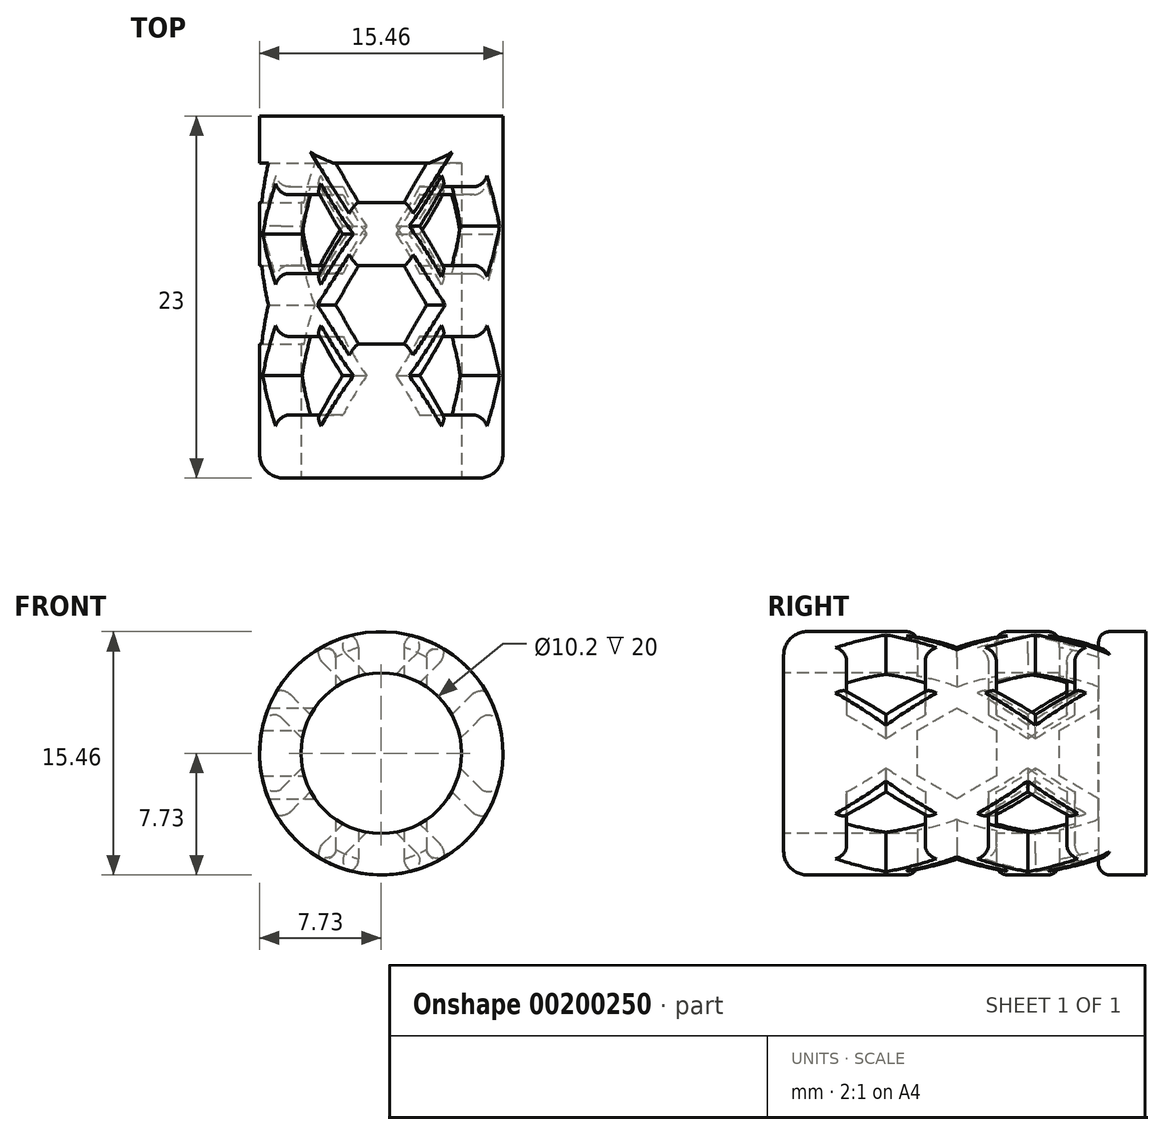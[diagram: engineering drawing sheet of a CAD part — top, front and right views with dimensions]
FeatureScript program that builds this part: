
annotation { "Feature Type Name" : "Feature", "Feature Type Description" : "" }
export const myFeature = defineFeature(function(context is Context, id is Id, definition is map)
    precondition{}
    {
        {
            var Q0;
            Q0=qCreatedBy(makeId("Front.planeOp"),FACE);
            var sketch = newSketch(context, id + "F0", { "sketchPlane" : qUnion([Q0])});
            skCircle(sketch, "E0", {"center": v(0, 0) * mm, "radius": 7.73 * mm});
            skSolve(sketch);
        }
        {
            var Q0;
            Q0=makeQuery(id+"F0.imprint","IMPRINT",FACE,{"disambiguationData":[TD([[makeQuery(id+"F0.imprint","IMPRINT",EDGE,{"derivedFrom":sQuery(id+"F0.wireOp",EDGE,"E0")}),1.0]])]});
            extrude(context, id + "F1", {"entities" : qUnion([Q0]), "oppositeDirection" : true, "depth" : 23 * mm, "offsetDistance" : 25 * mm});
        }
        {
            var Q0;
            Q0=makeQuery(id+"F1.opExtrude","CAP_FACE",FACE,{"disambiguationData":[OSD([sQuery(id+"F0.wireOp",EDGE,"E0")])],"isStart":true});
            var sketch = newSketch(context, id + "F2", { "sketchPlane" : qUnion([Q0])});
            skCircle(sketch, "E1", {"center": v(0, 0) * mm, "radius": 5.1 * mm});
            skSolve(sketch);
        }
        {
            var Q0;
            Q0=qSketchRegion(id+"F2",true);
            extrude(context, id + "F3", {"entities" : qUnion([Q0]), "operationType" : NewBodyOperationType.REMOVE, "oppositeDirection" : true, "depth" : 20 * mm, "offsetDistance" : 25 * mm});
        }
        {
            var Q0;
            Q0=qCreatedBy(makeId("Top.planeOp"),FACE);
            var sketch = newSketch(context, id + "F4", { "sketchPlane" : qUnion([Q0])});
            skLineSegment(sketch, "E2", {"start": v(0, 0) * mm, "end": v(0, 6.5) * mm, "construction": true});
            skLineSegment(sketch, "E3", {"start": v(0, 6.5) * mm, "end": v(0, 9) * mm, "construction": true});
            skCircle(sketch, "E4.cCircle", {"center": v(0, 6.5) * mm, "radius": 2.5 * mm, "construction": true});
            skLineSegment(sketch, "E4.0", {"start": v(-1.44, 9) * mm, "end": v(1.44, 9) * mm});
            skLineSegment(sketch, "E4.1", {"start": v(1.44, 9) * mm, "end": v(2.89, 6.5) * mm});
            skLineSegment(sketch, "E4.2", {"start": v(2.89, 6.5) * mm, "end": v(1.44, 4) * mm});
            skLineSegment(sketch, "E4.3", {"start": v(1.44, 4) * mm, "end": v(-1.44, 4) * mm});
            skLineSegment(sketch, "E4.4", {"start": v(-1.44, 4) * mm, "end": v(-2.89, 6.5) * mm});
            skLineSegment(sketch, "E4.5", {"start": v(-2.89, 6.5) * mm, "end": v(-1.44, 9) * mm});
            skPoint(sketch, "E4.0.midPoint", {"position": v(0, 9) * mm});
            skLineSegment(sketch, "E5.0.1.0", {"start": v(-2.89, 15.5) * mm, "end": v(-1.44, 18) * mm});
            skLineSegment(sketch, "E5.0.1.1", {"start": v(1.44, 13) * mm, "end": v(-1.44, 13) * mm});
            skLineSegment(sketch, "E5.0.1.2", {"start": v(2.89, 15.5) * mm, "end": v(1.44, 13) * mm});
            skLineSegment(sketch, "E5.0.1.3", {"start": v(1.44, 18) * mm, "end": v(2.89, 15.5) * mm});
            skLineSegment(sketch, "E5.0.1.4", {"start": v(-1.44, 18) * mm, "end": v(1.44, 18) * mm});
            skLineSegment(sketch, "E5.0.1.5", {"start": v(0, 15.5) * mm, "end": v(0, 18) * mm, "construction": true});
            skPoint(sketch, "E5.0.1.6", {"position": v(0, 18) * mm});
            skLineSegment(sketch, "E5.0.1.7", {"start": v(-1.44, 13) * mm, "end": v(-2.89, 15.5) * mm});
            skCircle(sketch, "E5.0.1.8", {"center": v(0, 15.5) * mm, "radius": 2.5 * mm, "construction": true});
            skLineSegment(sketch, "E5.direction1", {"start": v(-1.44, 4) * mm, "end": v(23.56, 4) * mm, "construction": true});
            skLineSegment(sketch, "E5.direction2", {"start": v(-1.44, 4) * mm, "end": v(-1.44, 13) * mm, "construction": true});
            skSolve(sketch);
        }
        {
            var Q0;
            Q0=qSketchRegion(id+"F4",true);
            extrude(context, id + "F5", {"entities" : qUnion([Q0]), "operationType" : NewBodyOperationType.REMOVE, "endBound" : BoundingType.SYMMETRIC, "depth" : 25 * mm});
        }
        {
            var Q0;
            Q0=qCreatedBy(makeId("Right.planeOp"),FACE);
            var sketch = newSketch(context, id + "F6", { "sketchPlane" : qUnion([Q0])});
            skLineSegment(sketch, "E6", {"start": v(0, 0) * mm, "end": v(6.5, 0) * mm, "construction": true});
            skLineSegment(sketch, "E7", {"start": v(6.5, 0) * mm, "end": v(9, 0) * mm, "construction": true});
            skCircle(sketch, "E8.cCircle", {"center": v(6.5, 0) * mm, "radius": 2.5 * mm, "construction": true});
            skLineSegment(sketch, "E8.0", {"start": v(9, 1.44) * mm, "end": v(9, -1.44) * mm});
            skLineSegment(sketch, "E8.1", {"start": v(9, -1.44) * mm, "end": v(6.5, -2.89) * mm});
            skLineSegment(sketch, "E8.2", {"start": v(6.5, -2.89) * mm, "end": v(4, -1.44) * mm});
            skLineSegment(sketch, "E8.3", {"start": v(4, -1.44) * mm, "end": v(4, 1.44) * mm});
            skLineSegment(sketch, "E8.4", {"start": v(4, 1.44) * mm, "end": v(6.5, 2.89) * mm});
            skLineSegment(sketch, "E8.5", {"start": v(6.5, 2.89) * mm, "end": v(9, 1.44) * mm});
            skPoint(sketch, "E8.0.midPoint", {"position": v(9, 0) * mm});
            skLineSegment(sketch, "E9", {"start": v(9, 0) * mm, "end": v(13.5, 0) * mm, "construction": true});
            skLineSegment(sketch, "E10", {"start": v(13.5, 0) * mm, "end": v(16, 0) * mm, "construction": true});
            skCircle(sketch, "E11.cCircle", {"center": v(16, 0) * mm, "radius": 2.5 * mm, "construction": true});
            skLineSegment(sketch, "E11.0", {"start": v(13.5, -1.44) * mm, "end": v(13.5, 1.44) * mm});
            skLineSegment(sketch, "E11.1", {"start": v(13.5, 1.44) * mm, "end": v(16, 2.89) * mm});
            skLineSegment(sketch, "E11.2", {"start": v(16, 2.89) * mm, "end": v(18.5, 1.44) * mm});
            skLineSegment(sketch, "E11.3", {"start": v(18.5, 1.44) * mm, "end": v(18.5, -1.44) * mm});
            skLineSegment(sketch, "E11.4", {"start": v(18.5, -1.44) * mm, "end": v(16, -2.89) * mm});
            skLineSegment(sketch, "E11.5", {"start": v(16, -2.89) * mm, "end": v(13.5, -1.44) * mm});
            skPoint(sketch, "E11.0.midPoint", {"position": v(13.5, 0) * mm});
            skSolve(sketch);
        }
        {
            var Q0;
            Q0=qSketchRegion(id+"F6",true);
            extrude(context, id + "F7", {"entities" : qUnion([Q0]), "operationType" : NewBodyOperationType.REMOVE, "endBound" : BoundingType.SYMMETRIC, "oppositeDirection" : true, "depth" : 25 * mm});
        }
        {
            var Q0;
            Q0=makeQuery(id+"F1.opExtrude","SWEPT_BODY",BODY,{"disambiguationData":[OSD([sQuery(id+"F0.wireOp",EDGE,"E0")])]});
            var Q1;
            Q1=makeQuery(id+"F1.opExtrude","SWEPT_FACE",FACE,{"disambiguationData":[OSD([sQuery(id+"F0.wireOp",EDGE,"E0")])]});
            transform(context, id + "F8", {"entities" : qUnion([Q0]), "transformType" : TransformType.ROTATION, "transformAxis" : qUnion([Q1]), "angle" : 45 * degree, "makeCopy" : false});
        }
        {
            var Q0;
            Q0=qCreatedBy(makeId("Top.planeOp"),FACE);
            var sketch = newSketch(context, id + "F9", { "sketchPlane" : qUnion([Q0])});
            skLineSegment(sketch, "E12", {"start": v(0, 0) * mm, "end": v(0, 11) * mm, "construction": true});
            skLineSegment(sketch, "E13", {"start": v(0, 11) * mm, "end": v(0, 13.5) * mm, "construction": true});
            skCircle(sketch, "E14.cCircle", {"center": v(0, 11) * mm, "radius": 2.5 * mm, "construction": true});
            skLineSegment(sketch, "E14.0", {"start": v(-1.44, 13.5) * mm, "end": v(1.44, 13.5) * mm});
            skLineSegment(sketch, "E14.1", {"start": v(1.44, 13.5) * mm, "end": v(2.89, 11) * mm});
            skLineSegment(sketch, "E14.2", {"start": v(2.89, 11) * mm, "end": v(1.44, 8.5) * mm});
            skLineSegment(sketch, "E14.3", {"start": v(1.44, 8.5) * mm, "end": v(-1.44, 8.5) * mm});
            skLineSegment(sketch, "E14.4", {"start": v(-1.44, 8.5) * mm, "end": v(-2.89, 11) * mm});
            skLineSegment(sketch, "E14.5", {"start": v(-2.89, 11) * mm, "end": v(-1.44, 13.5) * mm});
            skPoint(sketch, "E14.0.midPoint", {"position": v(0, 13.5) * mm});
            skLineSegment(sketch, "E15.0.1.0", {"start": v(0, 20) * mm, "end": v(0, 22.5) * mm, "construction": true});
            skPoint(sketch, "E15.0.1.1", {"position": v(0, 22.5) * mm});
            skLineSegment(sketch, "E15.0.1.2", {"start": v(1.44, 17.5) * mm, "end": v(-1.44, 17.5) * mm});
            skLineSegment(sketch, "E15.0.1.3", {"start": v(2.89, 20) * mm, "end": v(1.44, 17.5) * mm});
            skLineSegment(sketch, "E15.0.1.6", {"start": v(-1.44, 17.5) * mm, "end": v(-2.89, 20) * mm});
            skCircle(sketch, "E15.0.1.8", {"center": v(0, 20) * mm, "radius": 2.5 * mm, "construction": true});
            skLineSegment(sketch, "E15.direction1", {"start": v(-1.44, 8.5) * mm, "end": v(23.56, 8.5) * mm, "construction": true});
            skLineSegment(sketch, "E15.direction2", {"start": v(-1.44, 8.5) * mm, "end": v(-1.44, 17.5) * mm, "construction": true});
            skLineSegment(sketch, "E16", {"start": v(0, 119) * mm, "end": v(0, 128) * mm, "construction": true});
            skCircle(sketch, "E17.cCircle", {"center": v(0, 128) * mm, "radius": 2.5 * mm, "construction": true});
            skLineSegment(sketch, "E17.3", {"start": v(1.44, 125.5) * mm, "end": v(-1.44, 125.5) * mm});
            skPoint(sketch, "E17.0.midPoint", {"position": v(0, 130.5) * mm});
            skLineSegment(sketch, "E18", {"start": v(0, 126.5) * mm, "end": v(0, 125.5) * mm, "construction": true});
            skLineSegment(sketch, "E19", {"start": v(0, 126.5) * mm, "end": v(2, 126.5) * mm});
            skLineSegment(sketch, "E20", {"start": v(0, 126.5) * mm, "end": v(-2, 126.5) * mm});
            skLineSegment(sketch, "E21", {"start": v(-2, 126.5) * mm, "end": v(-1.44, 125.5) * mm});
            skLineSegment(sketch, "E22", {"start": v(1.44, 125.5) * mm, "end": v(2, 126.5) * mm});
            skLineSegment(sketch, "E23", {"start": v(0, 11) * mm, "end": v(0, 2) * mm, "construction": true});
            skPoint(sketch, "E24.0.midPoint", {"position": v(0, -0.5) * mm});
            skLineSegment(sketch, "E25", {"start": v(2.89, 20) * mm, "end": v(-2.89, 20) * mm});
            skSolve(sketch);
        }
        {
            var Q0;
            Q0=qSketchRegion(id+"F9",true);
            extrude(context, id + "F10", {"entities" : qUnion([Q0]), "operationType" : NewBodyOperationType.REMOVE, "endBound" : BoundingType.SYMMETRIC, "depth" : 25 * mm});
        }
        {
            var Q0;
            Q0=qCreatedBy(makeId("Right.planeOp"),FACE);
            var sketch = newSketch(context, id + "F11", { "sketchPlane" : qUnion([Q0])});
            skLineSegment(sketch, "E26", {"start": v(0, 0) * mm, "end": v(11, 0) * mm, "construction": true});
            skLineSegment(sketch, "E27", {"start": v(13.5, 0) * mm, "end": v(11, 0) * mm, "construction": true});
            skCircle(sketch, "E28.cCircle", {"center": v(11, 0) * mm, "radius": 2.5 * mm, "construction": true});
            skLineSegment(sketch, "E28.0", {"start": v(13.5, 1.44) * mm, "end": v(13.5, -1.44) * mm});
            skLineSegment(sketch, "E28.1", {"start": v(13.5, -1.44) * mm, "end": v(11, -2.89) * mm});
            skLineSegment(sketch, "E28.2", {"start": v(11, -2.89) * mm, "end": v(8.5, -1.44) * mm});
            skLineSegment(sketch, "E28.3", {"start": v(8.5, -1.44) * mm, "end": v(8.5, 1.44) * mm});
            skLineSegment(sketch, "E28.4", {"start": v(8.5, 1.44) * mm, "end": v(11, 2.89) * mm});
            skLineSegment(sketch, "E28.5", {"start": v(11, 2.89) * mm, "end": v(13.5, 1.44) * mm});
            skPoint(sketch, "E28.0.midPoint", {"position": v(13.5, 0) * mm});
            skLineSegment(sketch, "E29", {"start": v(13.5, 0) * mm, "end": v(20, 0) * mm, "construction": true});
            skLineSegment(sketch, "E30", {"start": v(20, 0) * mm, "end": v(22.5, 0) * mm, "construction": true});
            skCircle(sketch, "E31.cCircle", {"center": v(20, 0) * mm, "radius": 2.5 * mm, "construction": true});
            skLineSegment(sketch, "E31.2", {"start": v(20, -2.89) * mm, "end": v(17.5, -1.44) * mm});
            skLineSegment(sketch, "E31.3", {"start": v(17.5, -1.44) * mm, "end": v(17.5, 1.44) * mm});
            skLineSegment(sketch, "E31.4", {"start": v(17.5, 1.44) * mm, "end": v(20, 2.89) * mm});
            skPoint(sketch, "E31.0.midPoint", {"position": v(22.5, 0) * mm});
            skLineSegment(sketch, "E32", {"start": v(2, 0) * mm, "end": v(11, 0) * mm, "construction": true});
            skPoint(sketch, "E33.0.midPoint", {"position": v(-0.5, 0) * mm});
            skLineSegment(sketch, "E34", {"start": v(20, 2.89) * mm, "end": v(20, -2.89) * mm});
            skSolve(sketch);
        }
        {
            var Q0;
            Q0=qSketchRegion(id+"F11",true);
            extrude(context, id + "F12", {"entities" : qUnion([Q0]), "operationType" : NewBodyOperationType.REMOVE, "oppositeDirection" : true, "depth" : 25 * mm});
        }
        {
            var Q0;
            Q0=makeQuery(id+"F1.opExtrude","CAP_EDGE",EDGE,{"disambiguationData":[OSD([sQuery(id+"F0.wireOp",EDGE,"E0")])],"isStart":true});
            fillet(context, id + "F13", {"entities" : qUnion([Q0]), "radius" : 1.5 * mm, "tangentPropagation" : true, "allowEdgeOverflow" : false});
        }
        {
            var Q0;
            Q0=makeQuery(id+"F5.boolean.opBoolean","INTERSECT",EDGE,{"disambiguationData":[OD(0.0)],"derivedFrom":[makeQuery(id+"F1.opExtrude","SWEPT_FACE",FACE,{"disambiguationData":[OSD([sQuery(id+"F0.wireOp",EDGE,"E0")])]}),makeQuery(id+"F5.opExtrude","SWEPT_FACE",FACE,{"disambiguationData":[OSD([sQuery(id+"F4.wireOp",EDGE,"b579cf08-57c8-4be4-a64a-6a7c8f7f1ba5")])]})]});
            var Q1;
            Q1=makeQuery(id+"F5.boolean.opBoolean","INTERSECT",EDGE,{"disambiguationData":[OD(0.0)],"derivedFrom":[makeQuery(id+"F1.opExtrude","SWEPT_FACE",FACE,{"disambiguationData":[OSD([sQuery(id+"F0.wireOp",EDGE,"E0")])]}),makeQuery(id+"F5.opExtrude","SWEPT_FACE",FACE,{"disambiguationData":[OSD([sQuery(id+"F4.wireOp",EDGE,"bcb0f5b9-98e4-4035-bb5b-1a8c92403a19")])]})]});
            var Q2;
            Q2=makeQuery(id+"F5.boolean.opBoolean","INTERSECT",EDGE,{"disambiguationData":[OD(0.0)],"derivedFrom":[makeQuery(id+"F1.opExtrude","SWEPT_FACE",FACE,{"disambiguationData":[OSD([sQuery(id+"F0.wireOp",EDGE,"E0")])]}),makeQuery(id+"F5.opExtrude","SWEPT_FACE",FACE,{"disambiguationData":[OSD([sQuery(id+"F4.wireOp",EDGE,"09477fc4-9d29-4f20-8901-aec53dcd1546")])]})]});
            var Q3;
            Q3=makeQuery(id+"F5.boolean.opBoolean","INTERSECT",EDGE,{"disambiguationData":[OD(0.0)],"derivedFrom":[makeQuery(id+"F1.opExtrude","SWEPT_FACE",FACE,{"disambiguationData":[OSD([sQuery(id+"F0.wireOp",EDGE,"E0")])]}),makeQuery(id+"F5.opExtrude","SWEPT_FACE",FACE,{"disambiguationData":[OSD([sQuery(id+"F4.wireOp",EDGE,"92af876a-0958-4a7c-97b2-f4e8acbef095")])]})]});
            var Q4;
            Q4=makeQuery(id+"F5.boolean.opBoolean","INTERSECT",EDGE,{"disambiguationData":[OD(0.0)],"derivedFrom":[makeQuery(id+"F1.opExtrude","SWEPT_FACE",FACE,{"disambiguationData":[OSD([sQuery(id+"F0.wireOp",EDGE,"E0")])]}),makeQuery(id+"F5.opExtrude","SWEPT_FACE",FACE,{"disambiguationData":[OSD([sQuery(id+"F4.wireOp",EDGE,"67b481ec-10fe-46d3-8faa-ebe6010fe4f1")])]})]});
            var Q5;
            Q5=makeQuery(id+"F5.boolean.opBoolean","INTERSECT",EDGE,{"disambiguationData":[OD(0.0)],"derivedFrom":[makeQuery(id+"F1.opExtrude","SWEPT_FACE",FACE,{"disambiguationData":[OSD([sQuery(id+"F0.wireOp",EDGE,"E0")])]}),makeQuery(id+"F5.opExtrude","SWEPT_FACE",FACE,{"disambiguationData":[OSD([sQuery(id+"F4.wireOp",EDGE,"aca02d5f-46a9-486e-88e3-eb9aae4273e8")])]})]});
            var Q6;
            Q6=makeQuery(id+"F5.boolean.opBoolean","INTERSECT",EDGE,{"disambiguationData":[OD(0.0)],"derivedFrom":[makeQuery(id+"F1.opExtrude","SWEPT_FACE",FACE,{"disambiguationData":[OSD([sQuery(id+"F0.wireOp",EDGE,"E0")])]}),makeQuery(id+"F5.opExtrude","SWEPT_FACE",FACE,{"disambiguationData":[OSD([sQuery(id+"F4.wireOp",EDGE,"76385219-3691-4f38-9da5-edf1140a4629")])]})]});
            var Q7;
            Q7=makeQuery(id+"F5.boolean.opBoolean","INTERSECT",EDGE,{"disambiguationData":[OD(0.0)],"derivedFrom":[makeQuery(id+"F1.opExtrude","SWEPT_FACE",FACE,{"disambiguationData":[OSD([sQuery(id+"F0.wireOp",EDGE,"E0")])]}),makeQuery(id+"F5.opExtrude","SWEPT_FACE",FACE,{"disambiguationData":[OSD([sQuery(id+"F4.wireOp",EDGE,"30311b2f-ed17-4601-a199-a8278ef993fb")])]})]});
            var Q8;
            Q8=makeQuery(id+"F5.boolean.opBoolean","INTERSECT",EDGE,{"disambiguationData":[OD(0.0)],"derivedFrom":[makeQuery(id+"F1.opExtrude","SWEPT_FACE",FACE,{"disambiguationData":[OSD([sQuery(id+"F0.wireOp",EDGE,"E0")])]}),makeQuery(id+"F5.opExtrude","SWEPT_FACE",FACE,{"disambiguationData":[OSD([sQuery(id+"F4.wireOp",EDGE,"ed008b68-955d-4315-9cc0-8abb2c6860b0")])]})]});
            var Q9;
            Q9=makeQuery(id+"F5.boolean.opBoolean","INTERSECT",EDGE,{"disambiguationData":[OD(0.0)],"derivedFrom":[makeQuery(id+"F1.opExtrude","SWEPT_FACE",FACE,{"disambiguationData":[OSD([sQuery(id+"F0.wireOp",EDGE,"E0")])]}),makeQuery(id+"F5.opExtrude","SWEPT_FACE",FACE,{"disambiguationData":[OSD([sQuery(id+"F4.wireOp",EDGE,"efc5e5b1-0746-45f0-90e3-bd883f3492f4")])]})]});
            var Q10;
            Q10=makeQuery(id+"F5.boolean.opBoolean","INTERSECT",EDGE,{"disambiguationData":[OD(0.0)],"derivedFrom":[makeQuery(id+"F1.opExtrude","SWEPT_FACE",FACE,{"disambiguationData":[OSD([sQuery(id+"F0.wireOp",EDGE,"E0")])]}),makeQuery(id+"F5.opExtrude","SWEPT_FACE",FACE,{"disambiguationData":[OSD([sQuery(id+"F4.wireOp",EDGE,"562b9cc4-530f-4157-bc84-2c37910fa221")])]})]});
            var Q11;
            Q11=makeQuery(id+"F5.boolean.opBoolean","INTERSECT",EDGE,{"disambiguationData":[OD(0.0)],"derivedFrom":[makeQuery(id+"F1.opExtrude","SWEPT_FACE",FACE,{"disambiguationData":[OSD([sQuery(id+"F0.wireOp",EDGE,"E0")])]}),makeQuery(id+"F5.opExtrude","SWEPT_FACE",FACE,{"disambiguationData":[OSD([sQuery(id+"F4.wireOp",EDGE,"ab9f0dd0-8a88-45b5-9e6c-47f07906d12f")])]})]});
            var Q12;
            Q12=makeQuery(id+"F5.boolean.opBoolean","INTERSECT",EDGE,{"disambiguationData":[OD(0.0)],"derivedFrom":[makeQuery(id+"F1.opExtrude","SWEPT_FACE",FACE,{"disambiguationData":[OSD([sQuery(id+"F0.wireOp",EDGE,"E0")])]}),makeQuery(id+"F5.opExtrude","SWEPT_FACE",FACE,{"disambiguationData":[OSD([sQuery(id+"F4.wireOp",EDGE,"5e54ec67-0438-4ccb-ab1e-fb0c5627ff7a")])]})]});
            var Q13;
            Q13=makeQuery(id+"F5.boolean.opBoolean","INTERSECT",EDGE,{"disambiguationData":[OD(0.0)],"derivedFrom":[makeQuery(id+"F1.opExtrude","SWEPT_FACE",FACE,{"disambiguationData":[OSD([sQuery(id+"F0.wireOp",EDGE,"E0")])]}),makeQuery(id+"F5.opExtrude","SWEPT_FACE",FACE,{"disambiguationData":[OSD([sQuery(id+"F4.wireOp",EDGE,"1da9000e-137c-457e-9dd6-58b65176467c")])]})]});
            var Q14;
            Q14=makeQuery(id+"F5.boolean.opBoolean","INTERSECT",EDGE,{"disambiguationData":[OD(0.0)],"derivedFrom":[makeQuery(id+"F1.opExtrude","SWEPT_FACE",FACE,{"disambiguationData":[OSD([sQuery(id+"F0.wireOp",EDGE,"E0")])]}),makeQuery(id+"F5.opExtrude","SWEPT_FACE",FACE,{"disambiguationData":[OSD([sQuery(id+"F4.wireOp",EDGE,"15ec9440-3994-4756-befc-73e6937f9073")])]})]});
            var Q15;
            Q15=makeQuery(id+"F5.boolean.opBoolean","INTERSECT",EDGE,{"disambiguationData":[OD(0.0)],"derivedFrom":[makeQuery(id+"F1.opExtrude","SWEPT_FACE",FACE,{"disambiguationData":[OSD([sQuery(id+"F0.wireOp",EDGE,"E0")])]}),makeQuery(id+"F5.opExtrude","SWEPT_FACE",FACE,{"disambiguationData":[OSD([sQuery(id+"F4.wireOp",EDGE,"70ca714e-c3bb-4dc2-844f-e69955e1961d")])]})]});
            var Q16;
            Q16=makeQuery(id+"F5.boolean.opBoolean","INTERSECT",EDGE,{"disambiguationData":[OD(0.0)],"derivedFrom":[makeQuery(id+"F1.opExtrude","SWEPT_FACE",FACE,{"disambiguationData":[OSD([sQuery(id+"F0.wireOp",EDGE,"E0")])]}),makeQuery(id+"F5.opExtrude","SWEPT_FACE",FACE,{"disambiguationData":[OSD([sQuery(id+"F4.wireOp",EDGE,"b9a5c8a8-e1c1-4ccb-a6a4-30bc00998619")])]})]});
            var Q17;
            Q17=makeQuery(id+"F5.boolean.opBoolean","INTERSECT",EDGE,{"disambiguationData":[OD(0.0)],"derivedFrom":[makeQuery(id+"F1.opExtrude","SWEPT_FACE",FACE,{"disambiguationData":[OSD([sQuery(id+"F0.wireOp",EDGE,"E0")])]}),makeQuery(id+"F5.opExtrude","SWEPT_FACE",FACE,{"disambiguationData":[OSD([sQuery(id+"F4.wireOp",EDGE,"66c2d1b9-9082-457f-8158-46fefb0d0b5d")])]})]});
            var Q18;
            Q18=makeQuery(id+"F5.boolean.opBoolean","INTERSECT",EDGE,{"disambiguationData":[OD(0.0)],"derivedFrom":[makeQuery(id+"F1.opExtrude","SWEPT_FACE",FACE,{"disambiguationData":[OSD([sQuery(id+"F0.wireOp",EDGE,"E0")])]}),makeQuery(id+"F5.opExtrude","SWEPT_FACE",FACE,{"disambiguationData":[OSD([sQuery(id+"F4.wireOp",EDGE,"fd9b85d0-086e-4753-9286-7d80f3d11dd9")])]})]});
            var Q19;
            Q19=makeQuery(id+"F5.boolean.opBoolean","INTERSECT",EDGE,{"disambiguationData":[OD(0.0)],"derivedFrom":[makeQuery(id+"F1.opExtrude","SWEPT_FACE",FACE,{"disambiguationData":[OSD([sQuery(id+"F0.wireOp",EDGE,"E0")])]}),makeQuery(id+"F5.opExtrude","SWEPT_FACE",FACE,{"disambiguationData":[OSD([sQuery(id+"F4.wireOp",EDGE,"82180203-eaff-47f3-b606-d8d7c32d142f")])]})]});
            var Q20;
            Q20=makeQuery(id+"F5.boolean.opBoolean","INTERSECT",EDGE,{"disambiguationData":[OD(0.0)],"derivedFrom":[makeQuery(id+"F1.opExtrude","SWEPT_FACE",FACE,{"disambiguationData":[OSD([sQuery(id+"F0.wireOp",EDGE,"E0")])]}),makeQuery(id+"F5.opExtrude","SWEPT_FACE",FACE,{"disambiguationData":[OSD([sQuery(id+"F4.wireOp",EDGE,"536ab4de-4fb2-4d7d-9807-1d714ccadb66")])]})]});
            var Q21;
            Q21=makeQuery(id+"F5.boolean.opBoolean","INTERSECT",EDGE,{"disambiguationData":[OD(0.0)],"derivedFrom":[makeQuery(id+"F1.opExtrude","SWEPT_FACE",FACE,{"disambiguationData":[OSD([sQuery(id+"F0.wireOp",EDGE,"E0")])]}),makeQuery(id+"F5.opExtrude","SWEPT_FACE",FACE,{"disambiguationData":[OSD([sQuery(id+"F4.wireOp",EDGE,"c5cda94b-8dbb-4131-8629-d94229ce36f8")])]})]});
            var Q22;
            Q22=makeQuery(id+"F5.boolean.opBoolean","INTERSECT",EDGE,{"disambiguationData":[OD(0.0)],"derivedFrom":[makeQuery(id+"F1.opExtrude","SWEPT_FACE",FACE,{"disambiguationData":[OSD([sQuery(id+"F0.wireOp",EDGE,"E0")])]}),makeQuery(id+"F5.opExtrude","SWEPT_FACE",FACE,{"disambiguationData":[OSD([sQuery(id+"F4.wireOp",EDGE,"b8538754-f3f1-4cf7-bfe9-078eb6985bef")])]})]});
            var Q23;
            Q23=makeQuery(id+"F5.boolean.opBoolean","INTERSECT",EDGE,{"disambiguationData":[OD(0.0)],"derivedFrom":[makeQuery(id+"F1.opExtrude","SWEPT_FACE",FACE,{"disambiguationData":[OSD([sQuery(id+"F0.wireOp",EDGE,"E0")])]}),makeQuery(id+"F5.opExtrude","SWEPT_FACE",FACE,{"disambiguationData":[OSD([sQuery(id+"F4.wireOp",EDGE,"9e1b2bd2-a8a3-4caa-b598-0f2db5d1325d")])]})]});
            var Q24;
            Q24=makeQuery(id+"F5.boolean.opBoolean","INTERSECT",EDGE,{"disambiguationData":[OD(0.0)],"derivedFrom":[makeQuery(id+"F1.opExtrude","SWEPT_FACE",FACE,{"disambiguationData":[OSD([sQuery(id+"F0.wireOp",EDGE,"E0")])]}),makeQuery(id+"F5.opExtrude","SWEPT_FACE",FACE,{"disambiguationData":[OSD([sQuery(id+"F4.wireOp",EDGE,"c0d87fc6-e010-4d73-961e-dfed47c8a1b3")])]})]});
            var Q25;
            Q25=makeQuery(id+"F5.boolean.opBoolean","INTERSECT",EDGE,{"disambiguationData":[OD(0.0)],"derivedFrom":[makeQuery(id+"F1.opExtrude","SWEPT_FACE",FACE,{"disambiguationData":[OSD([sQuery(id+"F0.wireOp",EDGE,"E0")])]}),makeQuery(id+"F5.opExtrude","SWEPT_FACE",FACE,{"disambiguationData":[OSD([sQuery(id+"F4.wireOp",EDGE,"14d064f9-5360-4d18-9d9e-82328bf9daba")])]})]});
            var Q26;
            Q26=makeQuery(id+"F5.boolean.opBoolean","INTERSECT",EDGE,{"disambiguationData":[OD(0.0)],"derivedFrom":[makeQuery(id+"F1.opExtrude","SWEPT_FACE",FACE,{"disambiguationData":[OSD([sQuery(id+"F0.wireOp",EDGE,"E0")])]}),makeQuery(id+"F5.opExtrude","SWEPT_FACE",FACE,{"disambiguationData":[OSD([sQuery(id+"F4.wireOp",EDGE,"b60fa973-c727-4668-bfa0-a1e16f7a99aa")])]})]});
            var Q27;
            Q27=makeQuery(id+"F5.boolean.opBoolean","INTERSECT",EDGE,{"disambiguationData":[OD(0.0)],"derivedFrom":[makeQuery(id+"F1.opExtrude","SWEPT_FACE",FACE,{"disambiguationData":[OSD([sQuery(id+"F0.wireOp",EDGE,"E0")])]}),makeQuery(id+"F5.opExtrude","SWEPT_FACE",FACE,{"disambiguationData":[OSD([sQuery(id+"F4.wireOp",EDGE,"978e1622-7887-4f07-a91b-81f9d5efcfbf")])]})]});
            var Q28;
            Q28=makeQuery(id+"F5.boolean.opBoolean","INTERSECT",EDGE,{"disambiguationData":[OD(0.0)],"derivedFrom":[makeQuery(id+"F1.opExtrude","SWEPT_FACE",FACE,{"disambiguationData":[OSD([sQuery(id+"F0.wireOp",EDGE,"E0")])]}),makeQuery(id+"F5.opExtrude","SWEPT_FACE",FACE,{"disambiguationData":[OSD([sQuery(id+"F4.wireOp",EDGE,"d0a2849f-a89e-4989-ab6e-8e188e140a90")])]})]});
            var Q29;
            Q29=makeQuery(id+"F5.boolean.opBoolean","INTERSECT",EDGE,{"disambiguationData":[OD(0.0)],"derivedFrom":[makeQuery(id+"F1.opExtrude","SWEPT_FACE",FACE,{"disambiguationData":[OSD([sQuery(id+"F0.wireOp",EDGE,"E0")])]}),makeQuery(id+"F5.opExtrude","SWEPT_FACE",FACE,{"disambiguationData":[OSD([sQuery(id+"F4.wireOp",EDGE,"f55199c0-7004-4acb-b4c7-226994b61401")])]})]});
            var Q30;
            Q30=makeQuery(id+"F5.boolean.opBoolean","INTERSECT",EDGE,{"disambiguationData":[OD(0.0)],"derivedFrom":[makeQuery(id+"F1.opExtrude","SWEPT_FACE",FACE,{"disambiguationData":[OSD([sQuery(id+"F0.wireOp",EDGE,"E0")])]}),makeQuery(id+"F5.opExtrude","SWEPT_FACE",FACE,{"disambiguationData":[OSD([sQuery(id+"F4.wireOp",EDGE,"8a1b3b7c-f627-453a-8324-eadb2e6b2aa6")])]})]});
            var Q31;
            Q31=makeQuery(id+"F5.boolean.opBoolean","INTERSECT",EDGE,{"disambiguationData":[OD(0.0)],"derivedFrom":[makeQuery(id+"F1.opExtrude","SWEPT_FACE",FACE,{"disambiguationData":[OSD([sQuery(id+"F0.wireOp",EDGE,"E0")])]}),makeQuery(id+"F5.opExtrude","SWEPT_FACE",FACE,{"disambiguationData":[OSD([sQuery(id+"F4.wireOp",EDGE,"d52b0a11-5b01-40f3-ab4f-3d3d9242be96")])]})]});
            var Q32;
            Q32=makeQuery(id+"F5.boolean.opBoolean","INTERSECT",EDGE,{"disambiguationData":[OD(0.0)],"derivedFrom":[makeQuery(id+"F1.opExtrude","SWEPT_FACE",FACE,{"disambiguationData":[OSD([sQuery(id+"F0.wireOp",EDGE,"E0")])]}),makeQuery(id+"F5.opExtrude","SWEPT_FACE",FACE,{"disambiguationData":[OSD([sQuery(id+"F4.wireOp",EDGE,"4d2b9fd0-2ce7-462d-91df-97fb973a0c3b")])]})]});
            var Q33;
            Q33=makeQuery(id+"F5.boolean.opBoolean","INTERSECT",EDGE,{"disambiguationData":[OD(0.0)],"derivedFrom":[makeQuery(id+"F1.opExtrude","SWEPT_FACE",FACE,{"disambiguationData":[OSD([sQuery(id+"F0.wireOp",EDGE,"E0")])]}),makeQuery(id+"F5.opExtrude","SWEPT_FACE",FACE,{"disambiguationData":[OSD([sQuery(id+"F4.wireOp",EDGE,"cdeb415e-409f-4668-ae01-d5015ff68174")])]})]});
            var Q34;
            Q34=makeQuery(id+"F5.boolean.opBoolean","INTERSECT",EDGE,{"disambiguationData":[OD(0.0)],"derivedFrom":[makeQuery(id+"F1.opExtrude","SWEPT_FACE",FACE,{"disambiguationData":[OSD([sQuery(id+"F0.wireOp",EDGE,"E0")])]}),makeQuery(id+"F5.opExtrude","SWEPT_FACE",FACE,{"disambiguationData":[OSD([sQuery(id+"F4.wireOp",EDGE,"f6bfe6da-8190-4625-8366-2eafc9149588")])]})]});
            var Q35;
            Q35=makeQuery(id+"F5.boolean.opBoolean","INTERSECT",EDGE,{"disambiguationData":[OD(0.0)],"derivedFrom":[makeQuery(id+"F1.opExtrude","SWEPT_FACE",FACE,{"disambiguationData":[OSD([sQuery(id+"F0.wireOp",EDGE,"E0")])]}),makeQuery(id+"F5.opExtrude","SWEPT_FACE",FACE,{"disambiguationData":[OSD([sQuery(id+"F4.wireOp",EDGE,"c79ec3c5-8163-43ca-85dc-8d9b1c829184")])]})]});
            var Q36;
            Q36=makeQuery(id+"F5.boolean.opBoolean","INTERSECT",EDGE,{"disambiguationData":[OD(0.0)],"derivedFrom":[makeQuery(id+"F1.opExtrude","SWEPT_FACE",FACE,{"disambiguationData":[OSD([sQuery(id+"F0.wireOp",EDGE,"E0")])]}),makeQuery(id+"F5.opExtrude","SWEPT_FACE",FACE,{"disambiguationData":[OSD([sQuery(id+"F4.wireOp",EDGE,"a3fb4c3e-2145-4d81-81b1-06ede13a7337")])]})]});
            var Q37;
            Q37=makeQuery(id+"F5.boolean.opBoolean","INTERSECT",EDGE,{"disambiguationData":[OD(0.0)],"derivedFrom":[makeQuery(id+"F1.opExtrude","SWEPT_FACE",FACE,{"disambiguationData":[OSD([sQuery(id+"F0.wireOp",EDGE,"E0")])]}),makeQuery(id+"F5.opExtrude","SWEPT_FACE",FACE,{"disambiguationData":[OSD([sQuery(id+"F4.wireOp",EDGE,"b0c4be78-8462-4223-a050-0597d47616df")])]})]});
            var Q38;
            Q38=makeQuery(id+"F5.boolean.opBoolean","INTERSECT",EDGE,{"disambiguationData":[OD(0.0)],"derivedFrom":[makeQuery(id+"F1.opExtrude","SWEPT_FACE",FACE,{"disambiguationData":[OSD([sQuery(id+"F0.wireOp",EDGE,"E0")])]}),makeQuery(id+"F5.opExtrude","SWEPT_FACE",FACE,{"disambiguationData":[OSD([sQuery(id+"F4.wireOp",EDGE,"b63d48e1-6cba-4484-95e4-232a2befb6ff")])]})]});
            var Q39;
            Q39=makeQuery(id+"F5.boolean.opBoolean","INTERSECT",EDGE,{"disambiguationData":[OD(0.0)],"derivedFrom":[makeQuery(id+"F1.opExtrude","SWEPT_FACE",FACE,{"disambiguationData":[OSD([sQuery(id+"F0.wireOp",EDGE,"E0")])]}),makeQuery(id+"F5.opExtrude","SWEPT_FACE",FACE,{"disambiguationData":[OSD([sQuery(id+"F4.wireOp",EDGE,"afbb9b2d-3fe8-4547-9304-fccae8a72bf5")])]})]});
            var Q40;
            Q40=makeQuery(id+"F5.boolean.opBoolean","INTERSECT",EDGE,{"disambiguationData":[OD(0.0)],"derivedFrom":[makeQuery(id+"F1.opExtrude","SWEPT_FACE",FACE,{"disambiguationData":[OSD([sQuery(id+"F0.wireOp",EDGE,"E0")])]}),makeQuery(id+"F5.opExtrude","SWEPT_FACE",FACE,{"disambiguationData":[OSD([sQuery(id+"F4.wireOp",EDGE,"17e898d8-84c7-47b4-8d53-d44f4836d596")])]})]});
            var Q41;
            Q41=makeQuery(id+"F5.boolean.opBoolean","INTERSECT",EDGE,{"disambiguationData":[OD(0.0)],"derivedFrom":[makeQuery(id+"F1.opExtrude","SWEPT_FACE",FACE,{"disambiguationData":[OSD([sQuery(id+"F0.wireOp",EDGE,"E0")])]}),makeQuery(id+"F5.opExtrude","SWEPT_FACE",FACE,{"disambiguationData":[OSD([sQuery(id+"F4.wireOp",EDGE,"0321eed8-d3a5-4dab-8f9f-a696995c0651")])]})]});
            var Q42;
            Q42=makeQuery(id+"F5.boolean.opBoolean","INTERSECT",EDGE,{"disambiguationData":[OD(0.0)],"derivedFrom":[makeQuery(id+"F1.opExtrude","SWEPT_FACE",FACE,{"disambiguationData":[OSD([sQuery(id+"F0.wireOp",EDGE,"E0")])]}),makeQuery(id+"F5.opExtrude","SWEPT_FACE",FACE,{"disambiguationData":[OSD([sQuery(id+"F4.wireOp",EDGE,"c4d35b72-aeb9-430e-9e73-853e9b0c76ec")])]})]});
            var Q43;
            Q43=makeQuery(id+"F5.boolean.opBoolean","INTERSECT",EDGE,{"disambiguationData":[OD(0.0)],"derivedFrom":[makeQuery(id+"F1.opExtrude","SWEPT_FACE",FACE,{"disambiguationData":[OSD([sQuery(id+"F0.wireOp",EDGE,"E0")])]}),makeQuery(id+"F5.opExtrude","SWEPT_FACE",FACE,{"disambiguationData":[OSD([sQuery(id+"F4.wireOp",EDGE,"dc280805-f6e6-449f-9c66-de12d14a6505")])]})]});
            var Q44;
            Q44=makeQuery(id+"F5.boolean.opBoolean","INTERSECT",EDGE,{"disambiguationData":[OD(0.0)],"derivedFrom":[makeQuery(id+"F1.opExtrude","SWEPT_FACE",FACE,{"disambiguationData":[OSD([sQuery(id+"F0.wireOp",EDGE,"E0")])]}),makeQuery(id+"F5.opExtrude","SWEPT_FACE",FACE,{"disambiguationData":[OSD([sQuery(id+"F4.wireOp",EDGE,"c3060930-26c4-4b07-9e4a-7a125c9e4bcc")])]})]});
            var Q45;
            Q45=makeQuery(id+"F5.boolean.opBoolean","INTERSECT",EDGE,{"disambiguationData":[OD(0.0)],"derivedFrom":[makeQuery(id+"F1.opExtrude","SWEPT_FACE",FACE,{"disambiguationData":[OSD([sQuery(id+"F0.wireOp",EDGE,"E0")])]}),makeQuery(id+"F5.opExtrude","SWEPT_FACE",FACE,{"disambiguationData":[OSD([sQuery(id+"F4.wireOp",EDGE,"c1b4e133-c4b8-441d-9ad6-da7bbba7f6e1")])]})]});
            var Q46;
            Q46=makeQuery(id+"F5.boolean.opBoolean","INTERSECT",EDGE,{"disambiguationData":[OD(0.0)],"derivedFrom":[makeQuery(id+"F1.opExtrude","SWEPT_FACE",FACE,{"disambiguationData":[OSD([sQuery(id+"F0.wireOp",EDGE,"E0")])]}),makeQuery(id+"F5.opExtrude","SWEPT_FACE",FACE,{"disambiguationData":[OSD([sQuery(id+"F4.wireOp",EDGE,"6482df09-691d-4fcb-8b92-72aa1eb952c4")])]})]});
            var Q47;
            Q47=makeQuery(id+"F5.boolean.opBoolean","INTERSECT",EDGE,{"disambiguationData":[OD(0.0)],"derivedFrom":[makeQuery(id+"F1.opExtrude","SWEPT_FACE",FACE,{"disambiguationData":[OSD([sQuery(id+"F0.wireOp",EDGE,"E0")])]}),makeQuery(id+"F5.opExtrude","SWEPT_FACE",FACE,{"disambiguationData":[OSD([sQuery(id+"F4.wireOp",EDGE,"c69de198-cab7-4a97-91da-0287aae22bb7")])]})]});
            var Q48;
            Q48=makeQuery(id+"F5.boolean.opBoolean","INTERSECT",EDGE,{"disambiguationData":[OD(0.0)],"derivedFrom":[makeQuery(id+"F1.opExtrude","SWEPT_FACE",FACE,{"disambiguationData":[OSD([sQuery(id+"F0.wireOp",EDGE,"E0")])]}),makeQuery(id+"F5.opExtrude","SWEPT_FACE",FACE,{"disambiguationData":[OSD([sQuery(id+"F4.wireOp",EDGE,"4dd2465f-f76c-4ed8-a0a4-661656c39b6e")])]})]});
            var Q49;
            Q49=makeQuery(id+"F5.boolean.opBoolean","INTERSECT",EDGE,{"disambiguationData":[OD(0.0)],"derivedFrom":[makeQuery(id+"F1.opExtrude","SWEPT_FACE",FACE,{"disambiguationData":[OSD([sQuery(id+"F0.wireOp",EDGE,"E0")])]}),makeQuery(id+"F5.opExtrude","SWEPT_FACE",FACE,{"disambiguationData":[OSD([sQuery(id+"F4.wireOp",EDGE,"981d5c34-8f63-4288-b664-c119c34ece28")])]})]});
            var Q50;
            Q50=makeQuery(id+"F5.boolean.opBoolean","INTERSECT",EDGE,{"disambiguationData":[OD(0.0)],"derivedFrom":[makeQuery(id+"F1.opExtrude","SWEPT_FACE",FACE,{"disambiguationData":[OSD([sQuery(id+"F0.wireOp",EDGE,"E0")])]}),makeQuery(id+"F5.opExtrude","SWEPT_FACE",FACE,{"disambiguationData":[OSD([sQuery(id+"F4.wireOp",EDGE,"4bb37bd6-656b-4624-b683-e77c2f51eea1")])]})]});
            var Q51;
            Q51=makeQuery(id+"F5.boolean.opBoolean","INTERSECT",EDGE,{"disambiguationData":[OD(0.0)],"derivedFrom":[makeQuery(id+"F1.opExtrude","SWEPT_FACE",FACE,{"disambiguationData":[OSD([sQuery(id+"F0.wireOp",EDGE,"E0")])]}),makeQuery(id+"F5.opExtrude","SWEPT_FACE",FACE,{"disambiguationData":[OSD([sQuery(id+"F4.wireOp",EDGE,"a7220ec3-3de3-437a-89c6-8f6e48a94db4")])]})]});
            var Q52;
            Q52=makeQuery(id+"F5.boolean.opBoolean","INTERSECT",EDGE,{"disambiguationData":[OD(0.0)],"derivedFrom":[makeQuery(id+"F1.opExtrude","SWEPT_FACE",FACE,{"disambiguationData":[OSD([sQuery(id+"F0.wireOp",EDGE,"E0")])]}),makeQuery(id+"F5.opExtrude","SWEPT_FACE",FACE,{"disambiguationData":[OSD([sQuery(id+"F4.wireOp",EDGE,"ad6a620c-f5ab-4820-8ed8-d40d38394706")])]})]});
            var Q53;
            Q53=makeQuery(id+"F5.boolean.opBoolean","INTERSECT",EDGE,{"disambiguationData":[OD(0.0)],"derivedFrom":[makeQuery(id+"F1.opExtrude","SWEPT_FACE",FACE,{"disambiguationData":[OSD([sQuery(id+"F0.wireOp",EDGE,"E0")])]}),makeQuery(id+"F5.opExtrude","SWEPT_FACE",FACE,{"disambiguationData":[OSD([sQuery(id+"F4.wireOp",EDGE,"941b1c59-87e7-468b-8371-b89298454958")])]})]});
            var Q54;
            Q54=makeQuery(id+"F5.boolean.opBoolean","INTERSECT",EDGE,{"disambiguationData":[OD(0.0)],"derivedFrom":[makeQuery(id+"F1.opExtrude","SWEPT_FACE",FACE,{"disambiguationData":[OSD([sQuery(id+"F0.wireOp",EDGE,"E0")])]}),makeQuery(id+"F5.opExtrude","SWEPT_FACE",FACE,{"disambiguationData":[OSD([sQuery(id+"F4.wireOp",EDGE,"bef314f7-3a79-43c5-a841-5e6a101abbee")])]})]});
            var Q55;
            Q55=makeQuery(id+"F5.boolean.opBoolean","INTERSECT",EDGE,{"disambiguationData":[OD(0.0)],"derivedFrom":[makeQuery(id+"F1.opExtrude","SWEPT_FACE",FACE,{"disambiguationData":[OSD([sQuery(id+"F0.wireOp",EDGE,"E0")])]}),makeQuery(id+"F5.opExtrude","SWEPT_FACE",FACE,{"disambiguationData":[OSD([sQuery(id+"F4.wireOp",EDGE,"0648dc57-717b-43e8-adf0-6dc20ff83d95")])]})]});
            var Q56;
            Q56=makeQuery(id+"F5.boolean.opBoolean","INTERSECT",EDGE,{"disambiguationData":[OD(0.0)],"derivedFrom":[makeQuery(id+"F1.opExtrude","SWEPT_FACE",FACE,{"disambiguationData":[OSD([sQuery(id+"F0.wireOp",EDGE,"E0")])]}),makeQuery(id+"F5.opExtrude","SWEPT_FACE",FACE,{"disambiguationData":[OSD([sQuery(id+"F4.wireOp",EDGE,"6b48d1a6-d9e0-4d44-864b-96c7a48616eb")])]})]});
            var Q57;
            Q57=makeQuery(id+"F5.boolean.opBoolean","INTERSECT",EDGE,{"disambiguationData":[OD(0.0)],"derivedFrom":[makeQuery(id+"F1.opExtrude","SWEPT_FACE",FACE,{"disambiguationData":[OSD([sQuery(id+"F0.wireOp",EDGE,"E0")])]}),makeQuery(id+"F5.opExtrude","SWEPT_FACE",FACE,{"disambiguationData":[OSD([sQuery(id+"F4.wireOp",EDGE,"0cab01fc-36dc-4ee5-8aad-b0ef9c2b601d")])]})]});
            var Q58;
            Q58=makeQuery(id+"F5.boolean.opBoolean","INTERSECT",EDGE,{"disambiguationData":[OD(0.0)],"derivedFrom":[makeQuery(id+"F1.opExtrude","SWEPT_FACE",FACE,{"disambiguationData":[OSD([sQuery(id+"F0.wireOp",EDGE,"E0")])]}),makeQuery(id+"F5.opExtrude","SWEPT_FACE",FACE,{"disambiguationData":[OSD([sQuery(id+"F4.wireOp",EDGE,"07e56c10-a22d-4a71-bd1c-05f810bbc1d3")])]})]});
            var Q59;
            Q59=makeQuery(id+"F5.boolean.opBoolean","INTERSECT",EDGE,{"disambiguationData":[OD(0.0)],"derivedFrom":[makeQuery(id+"F1.opExtrude","SWEPT_FACE",FACE,{"disambiguationData":[OSD([sQuery(id+"F0.wireOp",EDGE,"E0")])]}),makeQuery(id+"F5.opExtrude","SWEPT_FACE",FACE,{"disambiguationData":[OSD([sQuery(id+"F4.wireOp",EDGE,"537901f3-e070-42e2-b15a-1a2327522176")])]})]});
            var Q60;
            Q60=makeQuery(id+"F5.boolean.opBoolean","INTERSECT",EDGE,{"disambiguationData":[OD(0.0)],"derivedFrom":[makeQuery(id+"F1.opExtrude","SWEPT_FACE",FACE,{"disambiguationData":[OSD([sQuery(id+"F0.wireOp",EDGE,"E0")])]}),makeQuery(id+"F5.opExtrude","SWEPT_FACE",FACE,{"disambiguationData":[OSD([sQuery(id+"F4.wireOp",EDGE,"570eaa13-a835-4f5c-9393-ffbc36022b64")])]})]});
            var Q61;
            Q61=makeQuery(id+"F5.boolean.opBoolean","INTERSECT",EDGE,{"disambiguationData":[OD(0.0)],"derivedFrom":[makeQuery(id+"F1.opExtrude","SWEPT_FACE",FACE,{"disambiguationData":[OSD([sQuery(id+"F0.wireOp",EDGE,"E0")])]}),makeQuery(id+"F5.opExtrude","SWEPT_FACE",FACE,{"disambiguationData":[OSD([sQuery(id+"F4.wireOp",EDGE,"5e9c52b7-e873-4326-812b-35e100de69ae")])]})]});
            var Q62;
            Q62=makeQuery(id+"F5.boolean.opBoolean","INTERSECT",EDGE,{"disambiguationData":[OD(0.0)],"derivedFrom":[makeQuery(id+"F1.opExtrude","SWEPT_FACE",FACE,{"disambiguationData":[OSD([sQuery(id+"F0.wireOp",EDGE,"E0")])]}),makeQuery(id+"F5.opExtrude","SWEPT_FACE",FACE,{"disambiguationData":[OSD([sQuery(id+"F4.wireOp",EDGE,"2f2a9835-3d8d-43e3-8360-67f6976d79c8")])]})]});
            var Q63;
            Q63=makeQuery(id+"F5.boolean.opBoolean","INTERSECT",EDGE,{"disambiguationData":[OD(0.0)],"derivedFrom":[makeQuery(id+"F1.opExtrude","SWEPT_FACE",FACE,{"disambiguationData":[OSD([sQuery(id+"F0.wireOp",EDGE,"E0")])]}),makeQuery(id+"F5.opExtrude","SWEPT_FACE",FACE,{"disambiguationData":[OSD([sQuery(id+"F4.wireOp",EDGE,"6d0ddde6-eeae-473b-8fbb-40228edda87a")])]})]});
            var Q64;
            Q64=makeQuery(id+"F5.boolean.opBoolean","INTERSECT",EDGE,{"disambiguationData":[OD(0.0)],"derivedFrom":[makeQuery(id+"F1.opExtrude","SWEPT_FACE",FACE,{"disambiguationData":[OSD([sQuery(id+"F0.wireOp",EDGE,"E0")])]}),makeQuery(id+"F5.opExtrude","SWEPT_FACE",FACE,{"disambiguationData":[OSD([sQuery(id+"F4.wireOp",EDGE,"698e3026-83e8-4a96-89d8-85748f8eba81")])]})]});
            var Q65;
            Q65=makeQuery(id+"F5.boolean.opBoolean","INTERSECT",EDGE,{"disambiguationData":[OD(0.0)],"derivedFrom":[makeQuery(id+"F1.opExtrude","SWEPT_FACE",FACE,{"disambiguationData":[OSD([sQuery(id+"F0.wireOp",EDGE,"E0")])]}),makeQuery(id+"F5.opExtrude","SWEPT_FACE",FACE,{"disambiguationData":[OSD([sQuery(id+"F4.wireOp",EDGE,"7b01ac76-4f73-4855-90dc-ab2067377e7d")])]})]});
            var Q66;
            Q66=makeQuery(id+"F5.boolean.opBoolean","INTERSECT",EDGE,{"disambiguationData":[OD(0.0)],"derivedFrom":[makeQuery(id+"F1.opExtrude","SWEPT_FACE",FACE,{"disambiguationData":[OSD([sQuery(id+"F0.wireOp",EDGE,"E0")])]}),makeQuery(id+"F5.opExtrude","SWEPT_FACE",FACE,{"disambiguationData":[OSD([sQuery(id+"F4.wireOp",EDGE,"f2f599b8-f5a2-47e9-8bc0-b292fd8eaa36")])]})]});
            var Q67;
            Q67=makeQuery(id+"F5.boolean.opBoolean","INTERSECT",EDGE,{"disambiguationData":[OD(0.0)],"derivedFrom":[makeQuery(id+"F1.opExtrude","SWEPT_FACE",FACE,{"disambiguationData":[OSD([sQuery(id+"F0.wireOp",EDGE,"E0")])]}),makeQuery(id+"F5.opExtrude","SWEPT_FACE",FACE,{"disambiguationData":[OSD([sQuery(id+"F4.wireOp",EDGE,"cd1f4ce4-2bdf-46d9-add9-aa29dd8642a7")])]})]});
            var Q68;
            Q68=makeQuery(id+"F5.boolean.opBoolean","INTERSECT",EDGE,{"disambiguationData":[OD(0.0)],"derivedFrom":[makeQuery(id+"F1.opExtrude","SWEPT_FACE",FACE,{"disambiguationData":[OSD([sQuery(id+"F0.wireOp",EDGE,"E0")])]}),makeQuery(id+"F5.opExtrude","SWEPT_FACE",FACE,{"disambiguationData":[OSD([sQuery(id+"F4.wireOp",EDGE,"37a73c55-c155-4e62-8b34-27461510b276")])]})]});
            var Q69;
            Q69=makeQuery(id+"F5.boolean.opBoolean","INTERSECT",EDGE,{"disambiguationData":[OD(0.0)],"derivedFrom":[makeQuery(id+"F1.opExtrude","SWEPT_FACE",FACE,{"disambiguationData":[OSD([sQuery(id+"F0.wireOp",EDGE,"E0")])]}),makeQuery(id+"F5.opExtrude","SWEPT_FACE",FACE,{"disambiguationData":[OSD([sQuery(id+"F4.wireOp",EDGE,"70095d75-91cd-40af-a70f-813c3114abcc")])]})]});
            var Q70;
            Q70=makeQuery(id+"F5.boolean.opBoolean","INTERSECT",EDGE,{"disambiguationData":[OD(0.0)],"derivedFrom":[makeQuery(id+"F1.opExtrude","SWEPT_FACE",FACE,{"disambiguationData":[OSD([sQuery(id+"F0.wireOp",EDGE,"E0")])]}),makeQuery(id+"F5.opExtrude","SWEPT_FACE",FACE,{"disambiguationData":[OSD([sQuery(id+"F4.wireOp",EDGE,"82706a72-63eb-40cc-839c-e0d1195260aa")])]})]});
            var Q71;
            Q71=makeQuery(id+"F5.boolean.opBoolean","INTERSECT",EDGE,{"disambiguationData":[OD(0.0)],"derivedFrom":[makeQuery(id+"F1.opExtrude","SWEPT_FACE",FACE,{"disambiguationData":[OSD([sQuery(id+"F0.wireOp",EDGE,"E0")])]}),makeQuery(id+"F5.opExtrude","SWEPT_FACE",FACE,{"disambiguationData":[OSD([sQuery(id+"F4.wireOp",EDGE,"8ba90ffa-b527-484e-b8a8-654b458372bb")])]})]});
            var Q72;
            Q72=makeQuery(id+"F5.boolean.opBoolean","INTERSECT",EDGE,{"disambiguationData":[OD(0.0)],"derivedFrom":[makeQuery(id+"F1.opExtrude","SWEPT_FACE",FACE,{"disambiguationData":[OSD([sQuery(id+"F0.wireOp",EDGE,"E0")])]}),makeQuery(id+"F5.opExtrude","SWEPT_FACE",FACE,{"disambiguationData":[OSD([sQuery(id+"F4.wireOp",EDGE,"f230033e-8e97-4c48-a61c-878d7d3044cc")])]})]});
            var Q73;
            Q73=makeQuery(id+"F5.boolean.opBoolean","INTERSECT",EDGE,{"disambiguationData":[OD(0.0)],"derivedFrom":[makeQuery(id+"F1.opExtrude","SWEPT_FACE",FACE,{"disambiguationData":[OSD([sQuery(id+"F0.wireOp",EDGE,"E0")])]}),makeQuery(id+"F5.opExtrude","SWEPT_FACE",FACE,{"disambiguationData":[OSD([sQuery(id+"F4.wireOp",EDGE,"4144a65f-7927-494c-8b6f-a1137679e0c2")])]})]});
            var Q74;
            Q74=makeQuery(id+"F5.boolean.opBoolean","INTERSECT",EDGE,{"disambiguationData":[OD(0.0)],"derivedFrom":[makeQuery(id+"F1.opExtrude","SWEPT_FACE",FACE,{"disambiguationData":[OSD([sQuery(id+"F0.wireOp",EDGE,"E0")])]}),makeQuery(id+"F5.opExtrude","SWEPT_FACE",FACE,{"disambiguationData":[OSD([sQuery(id+"F4.wireOp",EDGE,"12fd482c-4469-40d2-a6f5-f27bb2f23065")])]})]});
            var Q75;
            Q75=makeQuery(id+"F5.boolean.opBoolean","INTERSECT",EDGE,{"disambiguationData":[OD(0.0)],"derivedFrom":[makeQuery(id+"F1.opExtrude","SWEPT_FACE",FACE,{"disambiguationData":[OSD([sQuery(id+"F0.wireOp",EDGE,"E0")])]}),makeQuery(id+"F5.opExtrude","SWEPT_FACE",FACE,{"disambiguationData":[OSD([sQuery(id+"F4.wireOp",EDGE,"068a08e4-cb17-442e-8f38-57a3403c7c46")])]})]});
            var Q76;
            Q76=makeQuery(id+"F5.boolean.opBoolean","INTERSECT",EDGE,{"disambiguationData":[OD(0.0)],"derivedFrom":[makeQuery(id+"F1.opExtrude","SWEPT_FACE",FACE,{"disambiguationData":[OSD([sQuery(id+"F0.wireOp",EDGE,"E0")])]}),makeQuery(id+"F5.opExtrude","SWEPT_FACE",FACE,{"disambiguationData":[OSD([sQuery(id+"F4.wireOp",EDGE,"57a90445-0bd0-490a-9b1f-698a67fd895c")])]})]});
            var Q77;
            Q77=makeQuery(id+"F5.boolean.opBoolean","INTERSECT",EDGE,{"disambiguationData":[OD(0.0)],"derivedFrom":[makeQuery(id+"F1.opExtrude","SWEPT_FACE",FACE,{"disambiguationData":[OSD([sQuery(id+"F0.wireOp",EDGE,"E0")])]}),makeQuery(id+"F5.opExtrude","SWEPT_FACE",FACE,{"disambiguationData":[OSD([sQuery(id+"F4.wireOp",EDGE,"0cf69e63-39ca-4a42-b99a-dd0b7aa5f2af")])]})]});
            var Q78;
            Q78=makeQuery(id+"F5.boolean.opBoolean","INTERSECT",EDGE,{"disambiguationData":[OD(0.0)],"derivedFrom":[makeQuery(id+"F1.opExtrude","SWEPT_FACE",FACE,{"disambiguationData":[OSD([sQuery(id+"F0.wireOp",EDGE,"E0")])]}),makeQuery(id+"F5.opExtrude","SWEPT_FACE",FACE,{"disambiguationData":[OSD([sQuery(id+"F4.wireOp",EDGE,"f02fcaa4-8809-4191-8bb9-9daee93d77e2")])]})]});
            var Q79;
            Q79=makeQuery(id+"F5.boolean.opBoolean","INTERSECT",EDGE,{"disambiguationData":[OD(0.0)],"derivedFrom":[makeQuery(id+"F1.opExtrude","SWEPT_FACE",FACE,{"disambiguationData":[OSD([sQuery(id+"F0.wireOp",EDGE,"E0")])]}),makeQuery(id+"F5.opExtrude","SWEPT_FACE",FACE,{"disambiguationData":[OSD([sQuery(id+"F4.wireOp",EDGE,"d264c38f-4b04-4a21-be61-ebc556e8b4dc")])]})]});
            var Q80;
            Q80=makeQuery(id+"F5.boolean.opBoolean","INTERSECT",EDGE,{"disambiguationData":[OD(0.0)],"derivedFrom":[makeQuery(id+"F1.opExtrude","SWEPT_FACE",FACE,{"disambiguationData":[OSD([sQuery(id+"F0.wireOp",EDGE,"E0")])]}),makeQuery(id+"F5.opExtrude","SWEPT_FACE",FACE,{"disambiguationData":[OSD([sQuery(id+"F4.wireOp",EDGE,"bd2a5c31-cc9d-444b-baf1-6f7b9b2beccf")])]})]});
            var Q81;
            Q81=makeQuery(id+"F5.boolean.opBoolean","INTERSECT",EDGE,{"disambiguationData":[OD(0.0)],"derivedFrom":[makeQuery(id+"F1.opExtrude","SWEPT_FACE",FACE,{"disambiguationData":[OSD([sQuery(id+"F0.wireOp",EDGE,"E0")])]}),makeQuery(id+"F5.opExtrude","SWEPT_FACE",FACE,{"disambiguationData":[OSD([sQuery(id+"F4.wireOp",EDGE,"19f739e4-1ef2-45c8-9f20-bd755fe40443")])]})]});
            var Q82;
            Q82=makeQuery(id+"F5.boolean.opBoolean","INTERSECT",EDGE,{"disambiguationData":[OD(0.0)],"derivedFrom":[makeQuery(id+"F1.opExtrude","SWEPT_FACE",FACE,{"disambiguationData":[OSD([sQuery(id+"F0.wireOp",EDGE,"E0")])]}),makeQuery(id+"F5.opExtrude","SWEPT_FACE",FACE,{"disambiguationData":[OSD([sQuery(id+"F4.wireOp",EDGE,"03b36015-34d2-4950-84e9-b550512b4ec9")])]})]});
            var Q83;
            Q83=makeQuery(id+"F5.boolean.opBoolean","INTERSECT",EDGE,{"disambiguationData":[OD(0.0)],"derivedFrom":[makeQuery(id+"F1.opExtrude","SWEPT_FACE",FACE,{"disambiguationData":[OSD([sQuery(id+"F0.wireOp",EDGE,"E0")])]}),makeQuery(id+"F5.opExtrude","SWEPT_FACE",FACE,{"disambiguationData":[OSD([sQuery(id+"F4.wireOp",EDGE,"10851094-9e06-4481-a16a-60cc523c1961")])]})]});
            var Q84;
            Q84=makeQuery(id+"F7.boolean.opBoolean","INTERSECT",EDGE,{"disambiguationData":[OD(0.0)],"derivedFrom":[makeQuery(id+"F1.opExtrude","SWEPT_FACE",FACE,{"disambiguationData":[OSD([sQuery(id+"F0.wireOp",EDGE,"E0")])]}),makeQuery(id+"F7.opExtrude","SWEPT_FACE",FACE,{"disambiguationData":[OSD([sQuery(id+"F6.wireOp",EDGE,"22307501-336a-4987-af9f-3473d2358a36")])]})]});
            var Q85;
            Q85=makeQuery(id+"F7.boolean.opBoolean","INTERSECT",EDGE,{"disambiguationData":[OD(0.0)],"derivedFrom":[makeQuery(id+"F1.opExtrude","SWEPT_FACE",FACE,{"disambiguationData":[OSD([sQuery(id+"F0.wireOp",EDGE,"E0")])]}),makeQuery(id+"F7.opExtrude","SWEPT_FACE",FACE,{"disambiguationData":[OSD([sQuery(id+"F6.wireOp",EDGE,"7a5957e4-cc16-4d21-8b24-b71f9a09db7a")])]})]});
            var Q86;
            Q86=makeQuery(id+"F7.boolean.opBoolean","INTERSECT",EDGE,{"disambiguationData":[OD(0.0)],"derivedFrom":[makeQuery(id+"F1.opExtrude","SWEPT_FACE",FACE,{"disambiguationData":[OSD([sQuery(id+"F0.wireOp",EDGE,"E0")])]}),makeQuery(id+"F7.opExtrude","SWEPT_FACE",FACE,{"disambiguationData":[OSD([sQuery(id+"F6.wireOp",EDGE,"f5a73cac-6e2b-4509-98b7-614c817debd5")])]})]});
            var Q87;
            Q87=makeQuery(id+"F7.boolean.opBoolean","INTERSECT",EDGE,{"disambiguationData":[OD(0.0)],"derivedFrom":[makeQuery(id+"F1.opExtrude","SWEPT_FACE",FACE,{"disambiguationData":[OSD([sQuery(id+"F0.wireOp",EDGE,"E0")])]}),makeQuery(id+"F7.opExtrude","SWEPT_FACE",FACE,{"disambiguationData":[OSD([sQuery(id+"F6.wireOp",EDGE,"3257f0e8-a14c-4f57-a5a9-66824f5aab70")])]})]});
            var Q88;
            Q88=makeQuery(id+"F7.boolean.opBoolean","INTERSECT",EDGE,{"disambiguationData":[OD(0.0)],"derivedFrom":[makeQuery(id+"F1.opExtrude","SWEPT_FACE",FACE,{"disambiguationData":[OSD([sQuery(id+"F0.wireOp",EDGE,"E0")])]}),makeQuery(id+"F7.opExtrude","SWEPT_FACE",FACE,{"disambiguationData":[OSD([sQuery(id+"F6.wireOp",EDGE,"ee405ad0-9952-4166-b40a-09788f6ddfb5")])]})]});
            var Q89;
            Q89=makeQuery(id+"F7.boolean.opBoolean","INTERSECT",EDGE,{"disambiguationData":[OD(0.0)],"derivedFrom":[makeQuery(id+"F1.opExtrude","SWEPT_FACE",FACE,{"disambiguationData":[OSD([sQuery(id+"F0.wireOp",EDGE,"E0")])]}),makeQuery(id+"F7.opExtrude","SWEPT_FACE",FACE,{"disambiguationData":[OSD([sQuery(id+"F6.wireOp",EDGE,"2fa87e37-a699-481d-8a24-3aeddef2e244")])]})]});
            var Q90;
            Q90=makeQuery(id+"F7.boolean.opBoolean","INTERSECT",EDGE,{"disambiguationData":[OD(0.0)],"derivedFrom":[makeQuery(id+"F1.opExtrude","SWEPT_FACE",FACE,{"disambiguationData":[OSD([sQuery(id+"F0.wireOp",EDGE,"E0")])]}),makeQuery(id+"F7.opExtrude","SWEPT_FACE",FACE,{"disambiguationData":[OSD([sQuery(id+"F6.wireOp",EDGE,"4cac9c55-7efd-43a6-b3a8-6db941ce081a")])]})]});
            var Q91;
            Q91=makeQuery(id+"F7.boolean.opBoolean","INTERSECT",EDGE,{"disambiguationData":[OD(0.0)],"derivedFrom":[makeQuery(id+"F1.opExtrude","SWEPT_FACE",FACE,{"disambiguationData":[OSD([sQuery(id+"F0.wireOp",EDGE,"E0")])]}),makeQuery(id+"F7.opExtrude","SWEPT_FACE",FACE,{"disambiguationData":[OSD([sQuery(id+"F6.wireOp",EDGE,"b7c61857-15d8-4b71-81a2-4fbbf24b3784")])]})]});
            var Q92;
            Q92=makeQuery(id+"F7.boolean.opBoolean","INTERSECT",EDGE,{"disambiguationData":[OD(0.0)],"derivedFrom":[makeQuery(id+"F1.opExtrude","SWEPT_FACE",FACE,{"disambiguationData":[OSD([sQuery(id+"F0.wireOp",EDGE,"E0")])]}),makeQuery(id+"F7.opExtrude","SWEPT_FACE",FACE,{"disambiguationData":[OSD([sQuery(id+"F6.wireOp",EDGE,"48937804-74be-4d1d-a780-8159de361928")])]})]});
            var Q93;
            Q93=makeQuery(id+"F7.boolean.opBoolean","INTERSECT",EDGE,{"disambiguationData":[OD(0.0)],"derivedFrom":[makeQuery(id+"F1.opExtrude","SWEPT_FACE",FACE,{"disambiguationData":[OSD([sQuery(id+"F0.wireOp",EDGE,"E0")])]}),makeQuery(id+"F7.opExtrude","SWEPT_FACE",FACE,{"disambiguationData":[OSD([sQuery(id+"F6.wireOp",EDGE,"f4b3b797-2859-490d-b7b5-c2bfef3c68df")])]})]});
            var Q94;
            Q94=makeQuery(id+"F7.boolean.opBoolean","INTERSECT",EDGE,{"disambiguationData":[OD(0.0)],"derivedFrom":[makeQuery(id+"F1.opExtrude","SWEPT_FACE",FACE,{"disambiguationData":[OSD([sQuery(id+"F0.wireOp",EDGE,"E0")])]}),makeQuery(id+"F7.opExtrude","SWEPT_FACE",FACE,{"disambiguationData":[OSD([sQuery(id+"F6.wireOp",EDGE,"1201f4c5-c131-4895-a1f1-c302d83bce6e")])]})]});
            var Q95;
            Q95=makeQuery(id+"F7.boolean.opBoolean","INTERSECT",EDGE,{"disambiguationData":[OD(0.0)],"derivedFrom":[makeQuery(id+"F1.opExtrude","SWEPT_FACE",FACE,{"disambiguationData":[OSD([sQuery(id+"F0.wireOp",EDGE,"E0")])]}),makeQuery(id+"F7.opExtrude","SWEPT_FACE",FACE,{"disambiguationData":[OSD([sQuery(id+"F6.wireOp",EDGE,"de09daf4-2825-49fb-a621-eb4d3bd58af1")])]})]});
            var Q96;
            Q96=makeQuery(id+"F7.boolean.opBoolean","INTERSECT",EDGE,{"disambiguationData":[OD(0.0)],"derivedFrom":[makeQuery(id+"F1.opExtrude","SWEPT_FACE",FACE,{"disambiguationData":[OSD([sQuery(id+"F0.wireOp",EDGE,"E0")])]}),makeQuery(id+"F7.opExtrude","SWEPT_FACE",FACE,{"disambiguationData":[OSD([sQuery(id+"F6.wireOp",EDGE,"2a262191-3a4f-451e-b395-dc7af2397be1")])]})]});
            var Q97;
            Q97=makeQuery(id+"F7.boolean.opBoolean","INTERSECT",EDGE,{"disambiguationData":[OD(0.0)],"derivedFrom":[makeQuery(id+"F1.opExtrude","SWEPT_FACE",FACE,{"disambiguationData":[OSD([sQuery(id+"F0.wireOp",EDGE,"E0")])]}),makeQuery(id+"F7.opExtrude","SWEPT_FACE",FACE,{"disambiguationData":[OSD([sQuery(id+"F6.wireOp",EDGE,"9832b7fa-ab71-4669-b3d5-036fdeb69183")])]})]});
            var Q98;
            Q98=makeQuery(id+"F7.boolean.opBoolean","INTERSECT",EDGE,{"disambiguationData":[OD(0.0)],"derivedFrom":[makeQuery(id+"F1.opExtrude","SWEPT_FACE",FACE,{"disambiguationData":[OSD([sQuery(id+"F0.wireOp",EDGE,"E0")])]}),makeQuery(id+"F7.opExtrude","SWEPT_FACE",FACE,{"disambiguationData":[OSD([sQuery(id+"F6.wireOp",EDGE,"5a534d87-88aa-4def-9ebb-4f3525dad718")])]})]});
            var Q99;
            Q99=makeQuery(id+"F7.boolean.opBoolean","INTERSECT",EDGE,{"disambiguationData":[OD(0.0)],"derivedFrom":[makeQuery(id+"F1.opExtrude","SWEPT_FACE",FACE,{"disambiguationData":[OSD([sQuery(id+"F0.wireOp",EDGE,"E0")])]}),makeQuery(id+"F7.opExtrude","SWEPT_FACE",FACE,{"disambiguationData":[OSD([sQuery(id+"F6.wireOp",EDGE,"af5d01d9-e0bb-42d4-a9e9-53d224fa13c4")])]})]});
            var Q100;
            Q100=makeQuery(id+"F7.boolean.opBoolean","INTERSECT",EDGE,{"disambiguationData":[OD(0.0)],"derivedFrom":[makeQuery(id+"F1.opExtrude","SWEPT_FACE",FACE,{"disambiguationData":[OSD([sQuery(id+"F0.wireOp",EDGE,"E0")])]}),makeQuery(id+"F7.opExtrude","SWEPT_FACE",FACE,{"disambiguationData":[OSD([sQuery(id+"F6.wireOp",EDGE,"63af3750-506c-4288-83c5-8929affd3ff9")])]})]});
            var Q101;
            Q101=makeQuery(id+"F7.boolean.opBoolean","INTERSECT",EDGE,{"disambiguationData":[OD(0.0)],"derivedFrom":[makeQuery(id+"F1.opExtrude","SWEPT_FACE",FACE,{"disambiguationData":[OSD([sQuery(id+"F0.wireOp",EDGE,"E0")])]}),makeQuery(id+"F7.opExtrude","SWEPT_FACE",FACE,{"disambiguationData":[OSD([sQuery(id+"F6.wireOp",EDGE,"2db1c546-a54b-418f-a515-398807a46512")])]})]});
            var Q102;
            Q102=makeQuery(id+"F10.boolean.opBoolean","INTERSECT",EDGE,{"disambiguationData":[OD(0.0)],"derivedFrom":[makeQuery(id+"F1.opExtrude","SWEPT_FACE",FACE,{"disambiguationData":[OSD([sQuery(id+"F0.wireOp",EDGE,"E0")])]}),makeQuery(id+"F10.opExtrude","SWEPT_FACE",FACE,{"disambiguationData":[OSD([sQuery(id+"F9.wireOp",EDGE,"429d95a1-3c8a-48cf-b1fd-65ae80db6ffc")])]})]});
            var Q103;
            Q103=makeQuery(id+"F10.boolean.opBoolean","INTERSECT",EDGE,{"disambiguationData":[OD(0.0)],"derivedFrom":[makeQuery(id+"F1.opExtrude","SWEPT_FACE",FACE,{"disambiguationData":[OSD([sQuery(id+"F0.wireOp",EDGE,"E0")])]}),makeQuery(id+"F10.opExtrude","SWEPT_FACE",FACE,{"disambiguationData":[OSD([sQuery(id+"F9.wireOp",EDGE,"88dc3317-14d6-4f39-a813-642e505b3db3")])]})]});
            var Q104;
            Q104=makeQuery(id+"F10.boolean.opBoolean","INTERSECT",EDGE,{"disambiguationData":[OD(0.0)],"derivedFrom":[makeQuery(id+"F1.opExtrude","SWEPT_FACE",FACE,{"disambiguationData":[OSD([sQuery(id+"F0.wireOp",EDGE,"E0")])]}),makeQuery(id+"F10.opExtrude","SWEPT_FACE",FACE,{"disambiguationData":[OSD([sQuery(id+"F9.wireOp",EDGE,"c61f0de6-50a4-4502-a890-74c6c6ac1cd3")])]})]});
            var Q105;
            Q105=makeQuery(id+"F10.boolean.opBoolean","INTERSECT",EDGE,{"disambiguationData":[OD(0.0)],"derivedFrom":[makeQuery(id+"F1.opExtrude","SWEPT_FACE",FACE,{"disambiguationData":[OSD([sQuery(id+"F0.wireOp",EDGE,"E0")])]}),makeQuery(id+"F10.opExtrude","SWEPT_FACE",FACE,{"disambiguationData":[OSD([sQuery(id+"F9.wireOp",EDGE,"479dec23-3f8f-44ee-8e45-d2b113d31b07")])]})]});
            var Q106;
            Q106=makeQuery(id+"F10.boolean.opBoolean","INTERSECT",EDGE,{"disambiguationData":[OD(0.0)],"derivedFrom":[makeQuery(id+"F1.opExtrude","SWEPT_FACE",FACE,{"disambiguationData":[OSD([sQuery(id+"F0.wireOp",EDGE,"E0")])]}),makeQuery(id+"F10.opExtrude","SWEPT_FACE",FACE,{"disambiguationData":[OSD([sQuery(id+"F9.wireOp",EDGE,"fce1ec24-8c70-45cc-92f2-20edd6db3c88")])]})]});
            var Q107;
            Q107=makeQuery(id+"F10.boolean.opBoolean","INTERSECT",EDGE,{"disambiguationData":[OD(0.0)],"derivedFrom":[makeQuery(id+"F1.opExtrude","SWEPT_FACE",FACE,{"disambiguationData":[OSD([sQuery(id+"F0.wireOp",EDGE,"E0")])]}),makeQuery(id+"F10.opExtrude","SWEPT_FACE",FACE,{"disambiguationData":[OSD([sQuery(id+"F9.wireOp",EDGE,"0975aea8-55f6-417d-8d6b-6ad5a96ef988")])]})]});
            var Q108;
            Q108=makeQuery(id+"F10.boolean.opBoolean","INTERSECT",EDGE,{"disambiguationData":[OD(0.0)],"derivedFrom":[makeQuery(id+"F1.opExtrude","SWEPT_FACE",FACE,{"disambiguationData":[OSD([sQuery(id+"F0.wireOp",EDGE,"E0")])]}),makeQuery(id+"F10.opExtrude","SWEPT_FACE",FACE,{"disambiguationData":[OSD([sQuery(id+"F9.wireOp",EDGE,"e0e213fe-66f1-429b-aeb4-bda37cd8a542")])]})]});
            var Q109;
            Q109=makeQuery(id+"F10.boolean.opBoolean","INTERSECT",EDGE,{"disambiguationData":[OD(0.0)],"derivedFrom":[makeQuery(id+"F1.opExtrude","SWEPT_FACE",FACE,{"disambiguationData":[OSD([sQuery(id+"F0.wireOp",EDGE,"E0")])]}),makeQuery(id+"F10.opExtrude","SWEPT_FACE",FACE,{"disambiguationData":[OSD([sQuery(id+"F9.wireOp",EDGE,"OpU4Ypz6-Hcb8-YkKV-7chd-lZCeiZS7tYYF")])]})]});
            var Q110;
            Q110=makeQuery(id+"F10.boolean.opBoolean","INTERSECT",EDGE,{"disambiguationData":[OD(0.0)],"derivedFrom":[makeQuery(id+"F1.opExtrude","SWEPT_FACE",FACE,{"disambiguationData":[OSD([sQuery(id+"F0.wireOp",EDGE,"E0")])]}),makeQuery(id+"F10.opExtrude","SWEPT_FACE",FACE,{"disambiguationData":[OSD([sQuery(id+"F9.wireOp",EDGE,"7meaahbg-dbg3-uSPd-PEJJ-e7DtyzYx0gQt"),sQuery(id+"F9.wireOp",EDGE,"vEAYXyeL-ay2Z-WL7a-7Ha5-VfRoazVvpcCo")])]})]});
            var Q111;
            Q111=makeQuery(id+"F10.boolean.opBoolean","INTERSECT",EDGE,{"disambiguationData":[OD(0.0)],"derivedFrom":[makeQuery(id+"F1.opExtrude","SWEPT_FACE",FACE,{"disambiguationData":[OSD([sQuery(id+"F0.wireOp",EDGE,"E0")])]}),makeQuery(id+"F10.opExtrude","SWEPT_FACE",FACE,{"disambiguationData":[OSD([sQuery(id+"F9.wireOp",EDGE,"1QEsIIjE-87yi-7XXF-o0p4-XyzEA0SBXInf")])]})]});
            var Q112;
            Q112=makeQuery(id+"F10.boolean.opBoolean","INTERSECT",EDGE,{"disambiguationData":[OD(0.0)],"derivedFrom":[makeQuery(id+"F1.opExtrude","SWEPT_FACE",FACE,{"disambiguationData":[OSD([sQuery(id+"F0.wireOp",EDGE,"E0")])]}),makeQuery(id+"F10.opExtrude","SWEPT_FACE",FACE,{"disambiguationData":[OSD([sQuery(id+"F9.wireOp",EDGE,"4fa15834-391d-4db3-8b3b-82f9d2034739")])]})]});
            var Q113;
            Q113=makeQuery(id+"F10.boolean.opBoolean","INTERSECT",EDGE,{"disambiguationData":[OD(0.0)],"derivedFrom":[makeQuery(id+"F1.opExtrude","SWEPT_FACE",FACE,{"disambiguationData":[OSD([sQuery(id+"F0.wireOp",EDGE,"E0")])]}),makeQuery(id+"F10.opExtrude","SWEPT_FACE",FACE,{"disambiguationData":[OSD([sQuery(id+"F9.wireOp",EDGE,"cf1de00f-3169-4f70-98fb-b7290205bd4b")])]})]});
            var Q114;
            Q114=makeQuery(id+"F10.boolean.opBoolean","INTERSECT",EDGE,{"disambiguationData":[OD(0.0)],"derivedFrom":[makeQuery(id+"F1.opExtrude","SWEPT_FACE",FACE,{"disambiguationData":[OSD([sQuery(id+"F0.wireOp",EDGE,"E0")])]}),makeQuery(id+"F10.opExtrude","SWEPT_FACE",FACE,{"disambiguationData":[OSD([sQuery(id+"F9.wireOp",EDGE,"e82f161c-c8f9-431a-b111-592f8292c69f")])]})]});
            var Q115;
            Q115=makeQuery(id+"F10.boolean.opBoolean","INTERSECT",EDGE,{"disambiguationData":[OD(0.0)],"derivedFrom":[makeQuery(id+"F1.opExtrude","SWEPT_FACE",FACE,{"disambiguationData":[OSD([sQuery(id+"F0.wireOp",EDGE,"E0")])]}),makeQuery(id+"F10.opExtrude","SWEPT_FACE",FACE,{"disambiguationData":[OSD([sQuery(id+"F9.wireOp",EDGE,"17f8cebd-a2bc-4d80-8a13-7e07ce9ceaf0")])]})]});
            var Q116;
            Q116=makeQuery(id+"F10.boolean.opBoolean","INTERSECT",EDGE,{"disambiguationData":[OD(0.0)],"derivedFrom":[makeQuery(id+"F1.opExtrude","SWEPT_FACE",FACE,{"disambiguationData":[OSD([sQuery(id+"F0.wireOp",EDGE,"E0")])]}),makeQuery(id+"F10.opExtrude","SWEPT_FACE",FACE,{"disambiguationData":[OSD([sQuery(id+"F9.wireOp",EDGE,"4653122c-81e7-43b8-a175-0e9b4399c1dd")])]})]});
            var Q117;
            Q117=makeQuery(id+"F10.boolean.opBoolean","INTERSECT",EDGE,{"disambiguationData":[OD(0.0)],"derivedFrom":[makeQuery(id+"F1.opExtrude","SWEPT_FACE",FACE,{"disambiguationData":[OSD([sQuery(id+"F0.wireOp",EDGE,"E0")])]}),makeQuery(id+"F10.opExtrude","SWEPT_FACE",FACE,{"disambiguationData":[OSD([sQuery(id+"F9.wireOp",EDGE,"f7332d99-994a-4820-91d6-0eb80c66d826")])]})]});
            var Q118;
            Q118=makeQuery(id+"F10.boolean.opBoolean","INTERSECT",EDGE,{"disambiguationData":[OD(0.0)],"derivedFrom":[makeQuery(id+"F1.opExtrude","SWEPT_FACE",FACE,{"disambiguationData":[OSD([sQuery(id+"F0.wireOp",EDGE,"E0")])]}),makeQuery(id+"F10.opExtrude","SWEPT_FACE",FACE,{"disambiguationData":[OSD([sQuery(id+"F9.wireOp",EDGE,"917abea8-5958-4d13-b49a-d9c63b39efb4")])]})]});
            var Q119;
            Q119=makeQuery(id+"F10.boolean.opBoolean","INTERSECT",EDGE,{"disambiguationData":[OD(0.0)],"derivedFrom":[makeQuery(id+"F1.opExtrude","SWEPT_FACE",FACE,{"disambiguationData":[OSD([sQuery(id+"F0.wireOp",EDGE,"E0")])]}),makeQuery(id+"F10.opExtrude","SWEPT_FACE",FACE,{"disambiguationData":[OSD([sQuery(id+"F9.wireOp",EDGE,"5ad42132-cac8-4035-b0a1-ce6f07b595eb")])]})]});
            var Q120;
            Q120=makeQuery(id+"F10.boolean.opBoolean","INTERSECT",EDGE,{"disambiguationData":[OD(0.0)],"derivedFrom":[makeQuery(id+"F1.opExtrude","SWEPT_FACE",FACE,{"disambiguationData":[OSD([sQuery(id+"F0.wireOp",EDGE,"E0")])]}),makeQuery(id+"F10.opExtrude","SWEPT_FACE",FACE,{"disambiguationData":[OSD([sQuery(id+"F9.wireOp",EDGE,"423f58d8-1f19-46c3-b5b6-1235c5f2b6ac")])]})]});
            var Q121;
            Q121=makeQuery(id+"F10.boolean.opBoolean","INTERSECT",EDGE,{"disambiguationData":[OD(0.0)],"derivedFrom":[makeQuery(id+"F1.opExtrude","SWEPT_FACE",FACE,{"disambiguationData":[OSD([sQuery(id+"F0.wireOp",EDGE,"E0")])]}),makeQuery(id+"F10.opExtrude","SWEPT_FACE",FACE,{"disambiguationData":[OSD([sQuery(id+"F9.wireOp",EDGE,"a8de5c63-b59d-4111-aaf0-c59ceeb84539")])]})]});
            var Q122;
            Q122=makeQuery(id+"F10.boolean.opBoolean","INTERSECT",EDGE,{"disambiguationData":[OD(0.0)],"derivedFrom":[makeQuery(id+"F1.opExtrude","SWEPT_FACE",FACE,{"disambiguationData":[OSD([sQuery(id+"F0.wireOp",EDGE,"E0")])]}),makeQuery(id+"F10.opExtrude","SWEPT_FACE",FACE,{"disambiguationData":[OSD([sQuery(id+"F9.wireOp",EDGE,"43266347-99e5-4a65-87d8-d68d1b57105e")])]})]});
            var Q123;
            Q123=makeQuery(id+"F10.boolean.opBoolean","INTERSECT",EDGE,{"disambiguationData":[OD(0.0)],"derivedFrom":[makeQuery(id+"F1.opExtrude","SWEPT_FACE",FACE,{"disambiguationData":[OSD([sQuery(id+"F0.wireOp",EDGE,"E0")])]}),makeQuery(id+"F10.opExtrude","SWEPT_FACE",FACE,{"disambiguationData":[OSD([sQuery(id+"F9.wireOp",EDGE,"2193aa8a-cfb0-48d0-87fc-1cfe83a7fd52")])]})]});
            var Q124;
            Q124=makeQuery(id+"F10.boolean.opBoolean","INTERSECT",EDGE,{"disambiguationData":[OD(0.0)],"derivedFrom":[makeQuery(id+"F1.opExtrude","SWEPT_FACE",FACE,{"disambiguationData":[OSD([sQuery(id+"F0.wireOp",EDGE,"E0")])]}),makeQuery(id+"F10.opExtrude","SWEPT_FACE",FACE,{"disambiguationData":[OSD([sQuery(id+"F9.wireOp",EDGE,"589360f9-4b1b-47cd-a11b-2a67260c207c")])]})]});
            var Q125;
            Q125=makeQuery(id+"F10.boolean.opBoolean","INTERSECT",EDGE,{"disambiguationData":[OD(0.0)],"derivedFrom":[makeQuery(id+"F1.opExtrude","SWEPT_FACE",FACE,{"disambiguationData":[OSD([sQuery(id+"F0.wireOp",EDGE,"E0")])]}),makeQuery(id+"F10.opExtrude","SWEPT_FACE",FACE,{"disambiguationData":[OSD([sQuery(id+"F9.wireOp",EDGE,"d7004727-f34f-4852-a492-ed529d9aa36c")])]})]});
            var Q126;
            Q126=makeQuery(id+"F10.boolean.opBoolean","INTERSECT",EDGE,{"disambiguationData":[OD(0.0)],"derivedFrom":[makeQuery(id+"F1.opExtrude","SWEPT_FACE",FACE,{"disambiguationData":[OSD([sQuery(id+"F0.wireOp",EDGE,"E0")])]}),makeQuery(id+"F10.opExtrude","SWEPT_FACE",FACE,{"disambiguationData":[OSD([sQuery(id+"F9.wireOp",EDGE,"b6c25ba9-2617-4775-a0b3-41ef528efab6")])]})]});
            var Q127;
            Q127=makeQuery(id+"F10.boolean.opBoolean","INTERSECT",EDGE,{"disambiguationData":[OD(0.0)],"derivedFrom":[makeQuery(id+"F1.opExtrude","SWEPT_FACE",FACE,{"disambiguationData":[OSD([sQuery(id+"F0.wireOp",EDGE,"E0")])]}),makeQuery(id+"F10.opExtrude","SWEPT_FACE",FACE,{"disambiguationData":[OSD([sQuery(id+"F9.wireOp",EDGE,"0749a5eb-1656-439a-a869-05d76e53423e")])]})]});
            var Q128;
            Q128=makeQuery(id+"F10.boolean.opBoolean","INTERSECT",EDGE,{"disambiguationData":[OD(0.0)],"derivedFrom":[makeQuery(id+"F1.opExtrude","SWEPT_FACE",FACE,{"disambiguationData":[OSD([sQuery(id+"F0.wireOp",EDGE,"E0")])]}),makeQuery(id+"F10.opExtrude","SWEPT_FACE",FACE,{"disambiguationData":[OSD([sQuery(id+"F9.wireOp",EDGE,"8357bcdf-6207-4d5b-93da-fad6725d465d")])]})]});
            var Q129;
            Q129=makeQuery(id+"F10.boolean.opBoolean","INTERSECT",EDGE,{"disambiguationData":[OD(0.0)],"derivedFrom":[makeQuery(id+"F1.opExtrude","SWEPT_FACE",FACE,{"disambiguationData":[OSD([sQuery(id+"F0.wireOp",EDGE,"E0")])]}),makeQuery(id+"F10.opExtrude","SWEPT_FACE",FACE,{"disambiguationData":[OSD([sQuery(id+"F9.wireOp",EDGE,"c678ade0-3d66-4aad-85d1-643d7c5f28b6")])]})]});
            var Q130;
            Q130=makeQuery(id+"F7.boolean.opBoolean","INTERSECT",EDGE,{"disambiguationData":[OD(0.0)],"derivedFrom":[makeQuery(id+"F1.opExtrude","SWEPT_FACE",FACE,{"disambiguationData":[OSD([sQuery(id+"F0.wireOp",EDGE,"E0")])]}),makeQuery(id+"F7.opExtrude","SWEPT_FACE",FACE,{"disambiguationData":[OSD([sQuery(id+"F6.wireOp",EDGE,"31c7d22c-81f8-4662-bd11-6a8b92b7cb61")])]})]});
            var Q131;
            Q131=makeQuery(id+"F7.boolean.opBoolean","INTERSECT",EDGE,{"disambiguationData":[OD(0.0)],"derivedFrom":[makeQuery(id+"F1.opExtrude","SWEPT_FACE",FACE,{"disambiguationData":[OSD([sQuery(id+"F0.wireOp",EDGE,"E0")])]}),makeQuery(id+"F7.opExtrude","SWEPT_FACE",FACE,{"disambiguationData":[OSD([sQuery(id+"F6.wireOp",EDGE,"9760f720-9e2d-42e7-b9e9-8ad347021829")])]})]});
            var Q132;
            Q132=makeQuery(id+"F7.boolean.opBoolean","INTERSECT",EDGE,{"disambiguationData":[OD(0.0)],"derivedFrom":[makeQuery(id+"F1.opExtrude","SWEPT_FACE",FACE,{"disambiguationData":[OSD([sQuery(id+"F0.wireOp",EDGE,"E0")])]}),makeQuery(id+"F7.opExtrude","SWEPT_FACE",FACE,{"disambiguationData":[OSD([sQuery(id+"F6.wireOp",EDGE,"f669afdf-d7ad-41c0-aa00-2f38db0ae71b")])]})]});
            var Q133;
            Q133=makeQuery(id+"F7.boolean.opBoolean","INTERSECT",EDGE,{"disambiguationData":[OD(0.0)],"derivedFrom":[makeQuery(id+"F1.opExtrude","SWEPT_FACE",FACE,{"disambiguationData":[OSD([sQuery(id+"F0.wireOp",EDGE,"E0")])]}),makeQuery(id+"F7.opExtrude","SWEPT_FACE",FACE,{"disambiguationData":[OSD([sQuery(id+"F6.wireOp",EDGE,"27ce2371-831d-4e51-9e08-e601952e9ea9")])]})]});
            var Q134;
            Q134=makeQuery(id+"F7.boolean.opBoolean","INTERSECT",EDGE,{"disambiguationData":[OD(0.0)],"derivedFrom":[makeQuery(id+"F1.opExtrude","SWEPT_FACE",FACE,{"disambiguationData":[OSD([sQuery(id+"F0.wireOp",EDGE,"E0")])]}),makeQuery(id+"F7.opExtrude","SWEPT_FACE",FACE,{"disambiguationData":[OSD([sQuery(id+"F6.wireOp",EDGE,"e27b1b56-f1a0-4449-8924-ff9f4a1ebb5a")])]})]});
            var Q135;
            Q135=makeQuery(id+"F10.boolean.opBoolean","INTERSECT",EDGE,{"disambiguationData":[OD(0.0)],"derivedFrom":[makeQuery(id+"F1.opExtrude","SWEPT_FACE",FACE,{"disambiguationData":[OSD([sQuery(id+"F0.wireOp",EDGE,"E0")])]}),makeQuery(id+"F10.opExtrude","SWEPT_FACE",FACE,{"disambiguationData":[OSD([sQuery(id+"F9.wireOp",EDGE,"bc574ee6-e8d7-4402-b7bf-a31d76de5201")])]})]});
            var Q136;
            Q136=makeQuery(id+"F10.boolean.opBoolean","INTERSECT",EDGE,{"disambiguationData":[OD(0.0)],"derivedFrom":[makeQuery(id+"F1.opExtrude","SWEPT_FACE",FACE,{"disambiguationData":[OSD([sQuery(id+"F0.wireOp",EDGE,"E0")])]}),makeQuery(id+"F10.opExtrude","SWEPT_FACE",FACE,{"disambiguationData":[OSD([sQuery(id+"F9.wireOp",EDGE,"34f3141e-2481-4cad-a724-18fe9355e9ac")])]})]});
            var Q137;
            Q137=makeQuery(id+"F10.boolean.opBoolean","INTERSECT",EDGE,{"disambiguationData":[OD(0.0)],"derivedFrom":[makeQuery(id+"F1.opExtrude","SWEPT_FACE",FACE,{"disambiguationData":[OSD([sQuery(id+"F0.wireOp",EDGE,"E0")])]}),makeQuery(id+"F10.opExtrude","SWEPT_FACE",FACE,{"disambiguationData":[OSD([sQuery(id+"F9.wireOp",EDGE,"6dc2a6c8-a69d-41e3-9ee2-05e60369f11b")])]})]});
            var Q138;
            Q138=makeQuery(id+"F10.boolean.opBoolean","INTERSECT",EDGE,{"disambiguationData":[OD(0.0)],"derivedFrom":[makeQuery(id+"F1.opExtrude","SWEPT_FACE",FACE,{"disambiguationData":[OSD([sQuery(id+"F0.wireOp",EDGE,"E0")])]}),makeQuery(id+"F10.opExtrude","SWEPT_FACE",FACE,{"disambiguationData":[OSD([sQuery(id+"F9.wireOp",EDGE,"2db869a3-9406-4888-bcbb-00bb43a69eba")])]})]});
            var Q139;
            Q139=makeQuery(id+"F10.boolean.opBoolean","INTERSECT",EDGE,{"disambiguationData":[OD(0.0)],"derivedFrom":[makeQuery(id+"F1.opExtrude","SWEPT_FACE",FACE,{"disambiguationData":[OSD([sQuery(id+"F0.wireOp",EDGE,"E0")])]}),makeQuery(id+"F10.opExtrude","SWEPT_FACE",FACE,{"disambiguationData":[OSD([sQuery(id+"F9.wireOp",EDGE,"7b437f7c-4576-4f11-8c60-76c3eb11ba37")])]})]});
            var Q140;
            Q140=makeQuery(id+"F10.boolean.opBoolean","INTERSECT",EDGE,{"disambiguationData":[OD(0.0)],"derivedFrom":[makeQuery(id+"F1.opExtrude","SWEPT_FACE",FACE,{"disambiguationData":[OSD([sQuery(id+"F0.wireOp",EDGE,"E0")])]}),makeQuery(id+"F10.opExtrude","SWEPT_FACE",FACE,{"disambiguationData":[OSD([sQuery(id+"F9.wireOp",EDGE,"7bb27c30-01e1-4c30-9b62-d81abe0e1569")])]})]});
            var Q141;
            Q141=makeQuery(id+"F7.boolean.opBoolean","INTERSECT",EDGE,{"disambiguationData":[OD(0.0)],"derivedFrom":[makeQuery(id+"F1.opExtrude","SWEPT_FACE",FACE,{"disambiguationData":[OSD([sQuery(id+"F0.wireOp",EDGE,"E0")])]}),makeQuery(id+"F7.opExtrude","SWEPT_FACE",FACE,{"disambiguationData":[OSD([sQuery(id+"F6.wireOp",EDGE,"93935017-728a-4f1c-903b-dfa4ee534358")])]})]});
            var Q142;
            Q142=makeQuery(id+"F7.boolean.opBoolean","INTERSECT",EDGE,{"disambiguationData":[OD(0.0)],"derivedFrom":[makeQuery(id+"F1.opExtrude","SWEPT_FACE",FACE,{"disambiguationData":[OSD([sQuery(id+"F0.wireOp",EDGE,"E0")])]}),makeQuery(id+"F7.opExtrude","SWEPT_FACE",FACE,{"disambiguationData":[OSD([sQuery(id+"F6.wireOp",EDGE,"1be80a28-2c43-4fd4-89f8-f32c44110b3f")])]})]});
            var Q143;
            Q143=makeQuery(id+"F7.boolean.opBoolean","INTERSECT",EDGE,{"disambiguationData":[OD(0.0)],"derivedFrom":[makeQuery(id+"F1.opExtrude","SWEPT_FACE",FACE,{"disambiguationData":[OSD([sQuery(id+"F0.wireOp",EDGE,"E0")])]}),makeQuery(id+"F7.opExtrude","SWEPT_FACE",FACE,{"disambiguationData":[OSD([sQuery(id+"F6.wireOp",EDGE,"bd02c535-79a8-436b-9978-bd3653fcbfbf")])]})]});
            var Q144;
            Q144=makeQuery(id+"F7.boolean.opBoolean","INTERSECT",EDGE,{"disambiguationData":[OD(0.0)],"derivedFrom":[makeQuery(id+"F1.opExtrude","SWEPT_FACE",FACE,{"disambiguationData":[OSD([sQuery(id+"F0.wireOp",EDGE,"E0")])]}),makeQuery(id+"F7.opExtrude","SWEPT_FACE",FACE,{"disambiguationData":[OSD([sQuery(id+"F6.wireOp",EDGE,"8923652c-60ee-40cc-b4c6-e39304594786")])]})]});
            var Q145;
            Q145=makeQuery(id+"F7.boolean.opBoolean","INTERSECT",EDGE,{"disambiguationData":[OD(0.0)],"derivedFrom":[makeQuery(id+"F1.opExtrude","SWEPT_FACE",FACE,{"disambiguationData":[OSD([sQuery(id+"F0.wireOp",EDGE,"E0")])]}),makeQuery(id+"F7.opExtrude","SWEPT_FACE",FACE,{"disambiguationData":[OSD([sQuery(id+"F6.wireOp",EDGE,"a1de85a8-8a62-40c6-b726-1736eda7a2da")])]})]});
            var Q146;
            Q146=makeQuery(id+"F7.boolean.opBoolean","INTERSECT",EDGE,{"disambiguationData":[OD(0.0)],"derivedFrom":[makeQuery(id+"F1.opExtrude","SWEPT_FACE",FACE,{"disambiguationData":[OSD([sQuery(id+"F0.wireOp",EDGE,"E0")])]}),makeQuery(id+"F7.opExtrude","SWEPT_FACE",FACE,{"disambiguationData":[OSD([sQuery(id+"F6.wireOp",EDGE,"5c94e7fe-7667-4b5c-a899-a170bc688a63")])]})]});
            var Q147;
            Q147=makeQuery(id+"F10.boolean.opBoolean","INTERSECT",EDGE,{"disambiguationData":[OD(0.0)],"derivedFrom":[makeQuery(id+"F1.opExtrude","SWEPT_FACE",FACE,{"disambiguationData":[OSD([sQuery(id+"F0.wireOp",EDGE,"E0")])]}),makeQuery(id+"F10.opExtrude","SWEPT_FACE",FACE,{"disambiguationData":[OSD([sQuery(id+"F9.wireOp",EDGE,"ad162529-5cfe-4944-83b4-e317f5486a3e")])]})]});
            var Q148;
            Q148=makeQuery(id+"F10.boolean.opBoolean","INTERSECT",EDGE,{"disambiguationData":[OD(0.0)],"derivedFrom":[makeQuery(id+"F1.opExtrude","SWEPT_FACE",FACE,{"disambiguationData":[OSD([sQuery(id+"F0.wireOp",EDGE,"E0")])]}),makeQuery(id+"F10.opExtrude","SWEPT_FACE",FACE,{"disambiguationData":[OSD([sQuery(id+"F9.wireOp",EDGE,"68b86c13-7ece-4168-b183-e17e549264ea")])]})]});
            var Q149;
            Q149=makeQuery(id+"F10.boolean.opBoolean","INTERSECT",EDGE,{"disambiguationData":[OD(0.0)],"derivedFrom":[makeQuery(id+"F1.opExtrude","SWEPT_FACE",FACE,{"disambiguationData":[OSD([sQuery(id+"F0.wireOp",EDGE,"E0")])]}),makeQuery(id+"F10.opExtrude","SWEPT_FACE",FACE,{"disambiguationData":[OSD([sQuery(id+"F9.wireOp",EDGE,"b2bf0872-2c35-4f65-a834-23150e7e820b")])]})]});
            var Q150;
            Q150=makeQuery(id+"F10.boolean.opBoolean","INTERSECT",EDGE,{"disambiguationData":[OD(0.0)],"derivedFrom":[makeQuery(id+"F1.opExtrude","SWEPT_FACE",FACE,{"disambiguationData":[OSD([sQuery(id+"F0.wireOp",EDGE,"E0")])]}),makeQuery(id+"F10.opExtrude","SWEPT_FACE",FACE,{"disambiguationData":[OSD([sQuery(id+"F9.wireOp",EDGE,"8715a638-6380-49e4-8166-a35da90eea4d")])]})]});
            var Q151;
            Q151=makeQuery(id+"F10.boolean.opBoolean","INTERSECT",EDGE,{"disambiguationData":[OD(0.0)],"derivedFrom":[makeQuery(id+"F1.opExtrude","SWEPT_FACE",FACE,{"disambiguationData":[OSD([sQuery(id+"F0.wireOp",EDGE,"E0")])]}),makeQuery(id+"F10.opExtrude","SWEPT_FACE",FACE,{"disambiguationData":[OSD([sQuery(id+"F9.wireOp",EDGE,"1193cbdb-8a08-404e-b46e-3bccfaa25342")])]})]});
            var Q152;
            Q152=makeQuery(id+"F10.boolean.opBoolean","INTERSECT",EDGE,{"disambiguationData":[OD(0.0)],"derivedFrom":[makeQuery(id+"F1.opExtrude","SWEPT_FACE",FACE,{"disambiguationData":[OSD([sQuery(id+"F0.wireOp",EDGE,"E0")])]}),makeQuery(id+"F10.opExtrude","SWEPT_FACE",FACE,{"disambiguationData":[OSD([sQuery(id+"F9.wireOp",EDGE,"9310307e-7862-42e2-8ad8-274fad6d12ca")])]})]});
            var Q153;
            Q153=makeQuery(id+"F7.boolean.opBoolean","INTERSECT",EDGE,{"disambiguationData":[OD(0.0)],"derivedFrom":[makeQuery(id+"F1.opExtrude","SWEPT_FACE",FACE,{"disambiguationData":[OSD([sQuery(id+"F0.wireOp",EDGE,"E0")])]}),makeQuery(id+"F7.opExtrude","SWEPT_FACE",FACE,{"disambiguationData":[OSD([sQuery(id+"F6.wireOp",EDGE,"a7bcfd16-c37a-45c4-b358-1ae0edba8923")])]})]});
            var Q154;
            Q154=makeQuery(id+"F7.boolean.opBoolean","INTERSECT",EDGE,{"disambiguationData":[OD(0.0)],"derivedFrom":[makeQuery(id+"F1.opExtrude","SWEPT_FACE",FACE,{"disambiguationData":[OSD([sQuery(id+"F0.wireOp",EDGE,"E0")])]}),makeQuery(id+"F7.opExtrude","SWEPT_FACE",FACE,{"disambiguationData":[OSD([sQuery(id+"F6.wireOp",EDGE,"ccd121b1-441a-4014-95ef-4c36e07d2233")])]})]});
            var Q155;
            Q155=makeQuery(id+"F7.boolean.opBoolean","INTERSECT",EDGE,{"disambiguationData":[OD(0.0)],"derivedFrom":[makeQuery(id+"F1.opExtrude","SWEPT_FACE",FACE,{"disambiguationData":[OSD([sQuery(id+"F0.wireOp",EDGE,"E0")])]}),makeQuery(id+"F7.opExtrude","SWEPT_FACE",FACE,{"disambiguationData":[OSD([sQuery(id+"F6.wireOp",EDGE,"1a29ebeb-8835-42a1-b92c-50c246a9d529")])]})]});
            var Q156;
            Q156=makeQuery(id+"F7.boolean.opBoolean","INTERSECT",EDGE,{"disambiguationData":[OD(0.0)],"derivedFrom":[makeQuery(id+"F1.opExtrude","SWEPT_FACE",FACE,{"disambiguationData":[OSD([sQuery(id+"F0.wireOp",EDGE,"E0")])]}),makeQuery(id+"F7.opExtrude","SWEPT_FACE",FACE,{"disambiguationData":[OSD([sQuery(id+"F6.wireOp",EDGE,"b31f20a5-7ea0-4ac5-bdea-8d9f319a5f5b")])]})]});
            var Q157;
            Q157=makeQuery(id+"F7.boolean.opBoolean","INTERSECT",EDGE,{"disambiguationData":[OD(0.0)],"derivedFrom":[makeQuery(id+"F1.opExtrude","SWEPT_FACE",FACE,{"disambiguationData":[OSD([sQuery(id+"F0.wireOp",EDGE,"E0")])]}),makeQuery(id+"F7.opExtrude","SWEPT_FACE",FACE,{"disambiguationData":[OSD([sQuery(id+"F6.wireOp",EDGE,"066ffb92-3af2-4bb7-b7a5-d42d1a48a872")])]})]});
            var Q158;
            Q158=makeQuery(id+"F7.boolean.opBoolean","INTERSECT",EDGE,{"disambiguationData":[OD(0.0)],"derivedFrom":[makeQuery(id+"F1.opExtrude","SWEPT_FACE",FACE,{"disambiguationData":[OSD([sQuery(id+"F0.wireOp",EDGE,"E0")])]}),makeQuery(id+"F7.opExtrude","SWEPT_FACE",FACE,{"disambiguationData":[OSD([sQuery(id+"F6.wireOp",EDGE,"ced44ab8-ddc7-4aad-977b-2de9040397a9")])]})]});
            var Q159;
            Q159=makeQuery(id+"F10.boolean.opBoolean","INTERSECT",EDGE,{"disambiguationData":[OD(0.0)],"derivedFrom":[makeQuery(id+"F1.opExtrude","SWEPT_FACE",FACE,{"disambiguationData":[OSD([sQuery(id+"F0.wireOp",EDGE,"E0")])]}),makeQuery(id+"F10.opExtrude","SWEPT_FACE",FACE,{"disambiguationData":[OSD([sQuery(id+"F9.wireOp",EDGE,"2ac3ecf1-5bac-41c2-b359-9419124c2cbe")])]})]});
            var Q160;
            Q160=makeQuery(id+"F10.boolean.opBoolean","INTERSECT",EDGE,{"disambiguationData":[OD(0.0)],"derivedFrom":[makeQuery(id+"F1.opExtrude","SWEPT_FACE",FACE,{"disambiguationData":[OSD([sQuery(id+"F0.wireOp",EDGE,"E0")])]}),makeQuery(id+"F10.opExtrude","SWEPT_FACE",FACE,{"disambiguationData":[OSD([sQuery(id+"F9.wireOp",EDGE,"bb57b571-6d28-4bdc-bb85-3a8de86b828f")])]})]});
            var Q161;
            Q161=makeQuery(id+"F10.boolean.opBoolean","INTERSECT",EDGE,{"disambiguationData":[OD(0.0)],"derivedFrom":[makeQuery(id+"F1.opExtrude","SWEPT_FACE",FACE,{"disambiguationData":[OSD([sQuery(id+"F0.wireOp",EDGE,"E0")])]}),makeQuery(id+"F10.opExtrude","SWEPT_FACE",FACE,{"disambiguationData":[OSD([sQuery(id+"F9.wireOp",EDGE,"01df38a3-00a2-4b1c-aa54-0799b5c0ab2b")])]})]});
            var Q162;
            Q162=makeQuery(id+"F10.boolean.opBoolean","INTERSECT",EDGE,{"disambiguationData":[OD(0.0)],"derivedFrom":[makeQuery(id+"F1.opExtrude","SWEPT_FACE",FACE,{"disambiguationData":[OSD([sQuery(id+"F0.wireOp",EDGE,"E0")])]}),makeQuery(id+"F10.opExtrude","SWEPT_FACE",FACE,{"disambiguationData":[OSD([sQuery(id+"F9.wireOp",EDGE,"8d6d2ff5-cd1a-4c01-981c-d6a7ec693cea")])]})]});
            var Q163;
            Q163=makeQuery(id+"F10.boolean.opBoolean","INTERSECT",EDGE,{"disambiguationData":[OD(0.0)],"derivedFrom":[makeQuery(id+"F1.opExtrude","SWEPT_FACE",FACE,{"disambiguationData":[OSD([sQuery(id+"F0.wireOp",EDGE,"E0")])]}),makeQuery(id+"F10.opExtrude","SWEPT_FACE",FACE,{"disambiguationData":[OSD([sQuery(id+"F9.wireOp",EDGE,"2a376053-e003-4ce5-91a1-66395999f384")])]})]});
            var Q164;
            Q164=makeQuery(id+"F10.boolean.opBoolean","INTERSECT",EDGE,{"disambiguationData":[OD(0.0)],"derivedFrom":[makeQuery(id+"F1.opExtrude","SWEPT_FACE",FACE,{"disambiguationData":[OSD([sQuery(id+"F0.wireOp",EDGE,"E0")])]}),makeQuery(id+"F10.opExtrude","SWEPT_FACE",FACE,{"disambiguationData":[OSD([sQuery(id+"F9.wireOp",EDGE,"3ae87d72-d5e9-4fd7-8bad-e14353bbd74b")])]})]});
            var Q165;
            Q165=makeQuery(id+"F10.boolean.opBoolean","INTERSECT",EDGE,{"disambiguationData":[OD(0.0)],"derivedFrom":[makeQuery(id+"F1.opExtrude","SWEPT_FACE",FACE,{"disambiguationData":[OSD([sQuery(id+"F0.wireOp",EDGE,"E0")])]}),makeQuery(id+"F10.opExtrude","SWEPT_FACE",FACE,{"disambiguationData":[OSD([sQuery(id+"F9.wireOp",EDGE,"8d6d2ff5-cd1a-4c01-981c-d6a7ec693cea")])]})]});
            var Q166;
            Q166=makeQuery(id+"F10.boolean.opBoolean","INTERSECT",EDGE,{"disambiguationData":[OD(0.0)],"derivedFrom":[makeQuery(id+"F1.opExtrude","SWEPT_FACE",FACE,{"disambiguationData":[OSD([sQuery(id+"F0.wireOp",EDGE,"E0")])]}),makeQuery(id+"F10.opExtrude","SWEPT_FACE",FACE,{"disambiguationData":[OSD([sQuery(id+"F9.wireOp",EDGE,"be914a45-ffb7-4e2b-a3ec-587ed71103c0")])]})]});
            var Q167;
            Q167=makeQuery(id+"F10.boolean.opBoolean","INTERSECT",EDGE,{"disambiguationData":[OD(0.0)],"derivedFrom":[makeQuery(id+"F1.opExtrude","SWEPT_FACE",FACE,{"disambiguationData":[OSD([sQuery(id+"F0.wireOp",EDGE,"E0")])]}),makeQuery(id+"F10.opExtrude","SWEPT_FACE",FACE,{"disambiguationData":[OSD([sQuery(id+"F9.wireOp",EDGE,"3ffd9d2e-510e-4de6-8091-eb6a432f9cc3")])]})]});
            var Q168;
            Q168=makeQuery(id+"F10.boolean.opBoolean","INTERSECT",EDGE,{"disambiguationData":[OD(0.0)],"derivedFrom":[makeQuery(id+"F1.opExtrude","SWEPT_FACE",FACE,{"disambiguationData":[OSD([sQuery(id+"F0.wireOp",EDGE,"E0")])]}),makeQuery(id+"F10.opExtrude","SWEPT_FACE",FACE,{"disambiguationData":[OSD([sQuery(id+"F9.wireOp",EDGE,"bd4633cb-a1a0-4c2a-b75b-ae6ce3798ed8")])]})]});
            var Q169;
            Q169=makeQuery(id+"F10.boolean.opBoolean","INTERSECT",EDGE,{"disambiguationData":[OD(0.0)],"derivedFrom":[makeQuery(id+"F1.opExtrude","SWEPT_FACE",FACE,{"disambiguationData":[OSD([sQuery(id+"F0.wireOp",EDGE,"E0")])]}),makeQuery(id+"F10.opExtrude","SWEPT_FACE",FACE,{"disambiguationData":[OSD([sQuery(id+"F9.wireOp",EDGE,"117fbaf9-7363-4f4d-8f80-632232ace110")])]})]});
            var Q170;
            Q170=makeQuery(id+"F10.boolean.opBoolean","INTERSECT",EDGE,{"disambiguationData":[OD(0.0)],"derivedFrom":[makeQuery(id+"F1.opExtrude","SWEPT_FACE",FACE,{"disambiguationData":[OSD([sQuery(id+"F0.wireOp",EDGE,"E0")])]}),makeQuery(id+"F10.opExtrude","SWEPT_FACE",FACE,{"disambiguationData":[OSD([sQuery(id+"F9.wireOp",EDGE,"a88a4bda-f792-4dab-aaff-bd76e840daaf")])]})]});
            var Q171;
            Q171=makeQuery(id+"F10.boolean.opBoolean","INTERSECT",EDGE,{"disambiguationData":[OD(0.0)],"derivedFrom":[makeQuery(id+"F1.opExtrude","SWEPT_FACE",FACE,{"disambiguationData":[OSD([sQuery(id+"F0.wireOp",EDGE,"E0")])]}),makeQuery(id+"F10.opExtrude","SWEPT_FACE",FACE,{"disambiguationData":[OSD([sQuery(id+"F9.wireOp",EDGE,"4e834629-6a74-4855-ade5-f6e74bb3a83c")])]})]});
            var Q172;
            Q172=makeQuery(id+"F7.boolean.opBoolean","INTERSECT",EDGE,{"disambiguationData":[OD(0.0)],"derivedFrom":[makeQuery(id+"F1.opExtrude","SWEPT_FACE",FACE,{"disambiguationData":[OSD([sQuery(id+"F0.wireOp",EDGE,"E0")])]}),makeQuery(id+"F7.opExtrude","SWEPT_FACE",FACE,{"disambiguationData":[OSD([sQuery(id+"F6.wireOp",EDGE,"6589fb1d-312b-4644-b9fc-294650b0a4aa")])]})]});
            var Q173;
            Q173=makeQuery(id+"F7.boolean.opBoolean","INTERSECT",EDGE,{"disambiguationData":[OD(0.0)],"derivedFrom":[makeQuery(id+"F1.opExtrude","SWEPT_FACE",FACE,{"disambiguationData":[OSD([sQuery(id+"F0.wireOp",EDGE,"E0")])]}),makeQuery(id+"F7.opExtrude","SWEPT_FACE",FACE,{"disambiguationData":[OSD([sQuery(id+"F6.wireOp",EDGE,"5f897133-5c0d-465f-b427-282926e35fab")])]})]});
            var Q174;
            Q174=makeQuery(id+"F7.boolean.opBoolean","INTERSECT",EDGE,{"disambiguationData":[OD(0.0)],"derivedFrom":[makeQuery(id+"F1.opExtrude","SWEPT_FACE",FACE,{"disambiguationData":[OSD([sQuery(id+"F0.wireOp",EDGE,"E0")])]}),makeQuery(id+"F7.opExtrude","SWEPT_FACE",FACE,{"disambiguationData":[OSD([sQuery(id+"F6.wireOp",EDGE,"7a775aec-8bcc-46c7-9e27-2acd780fd80b")])]})]});
            var Q175;
            Q175=makeQuery(id+"F7.boolean.opBoolean","INTERSECT",EDGE,{"disambiguationData":[OD(0.0)],"derivedFrom":[makeQuery(id+"F1.opExtrude","SWEPT_FACE",FACE,{"disambiguationData":[OSD([sQuery(id+"F0.wireOp",EDGE,"E0")])]}),makeQuery(id+"F7.opExtrude","SWEPT_FACE",FACE,{"disambiguationData":[OSD([sQuery(id+"F6.wireOp",EDGE,"2559da72-e7a5-4982-a9d1-a98772cbbb5a")])]})]});
            var Q176;
            Q176=makeQuery(id+"F7.boolean.opBoolean","INTERSECT",EDGE,{"disambiguationData":[OD(0.0)],"derivedFrom":[makeQuery(id+"F1.opExtrude","SWEPT_FACE",FACE,{"disambiguationData":[OSD([sQuery(id+"F0.wireOp",EDGE,"E0")])]}),makeQuery(id+"F7.opExtrude","SWEPT_FACE",FACE,{"disambiguationData":[OSD([sQuery(id+"F6.wireOp",EDGE,"42a4befa-22b1-49a7-8f1c-9fc5c3368c5a")])]})]});
            var Q177;
            Q177=makeQuery(id+"F7.boolean.opBoolean","INTERSECT",EDGE,{"disambiguationData":[OD(0.0)],"derivedFrom":[makeQuery(id+"F1.opExtrude","SWEPT_FACE",FACE,{"disambiguationData":[OSD([sQuery(id+"F0.wireOp",EDGE,"E0")])]}),makeQuery(id+"F7.opExtrude","SWEPT_FACE",FACE,{"disambiguationData":[OSD([sQuery(id+"F6.wireOp",EDGE,"3dd659d4-b549-4a72-82e9-7f461cba10e9")])]})]});
            var Q178;
            Q178=makeQuery(id+"F7.boolean.opBoolean","INTERSECT",EDGE,{"disambiguationData":[OD(0.0)],"derivedFrom":[makeQuery(id+"F1.opExtrude","SWEPT_FACE",FACE,{"disambiguationData":[OSD([sQuery(id+"F0.wireOp",EDGE,"E0")])]}),makeQuery(id+"F7.opExtrude","SWEPT_FACE",FACE,{"disambiguationData":[OSD([sQuery(id+"F6.wireOp",EDGE,"ac3f06c8-d89a-4fdc-8656-42fb609f7cb2")])]})]});
            var Q179;
            Q179=makeQuery(id+"F7.boolean.opBoolean","INTERSECT",EDGE,{"disambiguationData":[OD(0.0)],"derivedFrom":[makeQuery(id+"F1.opExtrude","SWEPT_FACE",FACE,{"disambiguationData":[OSD([sQuery(id+"F0.wireOp",EDGE,"E0")])]}),makeQuery(id+"F7.opExtrude","SWEPT_FACE",FACE,{"disambiguationData":[OSD([sQuery(id+"F6.wireOp",EDGE,"20dcadda-9b8f-4667-a020-87fb84a874f5")])]})]});
            var Q180;
            Q180=makeQuery(id+"F7.boolean.opBoolean","INTERSECT",EDGE,{"disambiguationData":[OD(0.0)],"derivedFrom":[makeQuery(id+"F1.opExtrude","SWEPT_FACE",FACE,{"disambiguationData":[OSD([sQuery(id+"F0.wireOp",EDGE,"E0")])]}),makeQuery(id+"F7.opExtrude","SWEPT_FACE",FACE,{"disambiguationData":[OSD([sQuery(id+"F6.wireOp",EDGE,"0a54e51b-04a4-4c72-8fdd-f2044cd41bb6")])]})]});
            var Q181;
            Q181=makeQuery(id+"F7.boolean.opBoolean","INTERSECT",EDGE,{"disambiguationData":[OD(0.0)],"derivedFrom":[makeQuery(id+"F1.opExtrude","SWEPT_FACE",FACE,{"disambiguationData":[OSD([sQuery(id+"F0.wireOp",EDGE,"E0")])]}),makeQuery(id+"F7.opExtrude","SWEPT_FACE",FACE,{"disambiguationData":[OSD([sQuery(id+"F6.wireOp",EDGE,"5279c50d-e3c7-40df-a6ae-2a829e30a2e4")])]})]});
            var Q182;
            Q182=makeQuery(id+"F7.boolean.opBoolean","INTERSECT",EDGE,{"disambiguationData":[OD(0.0)],"derivedFrom":[makeQuery(id+"F1.opExtrude","SWEPT_FACE",FACE,{"disambiguationData":[OSD([sQuery(id+"F0.wireOp",EDGE,"E0")])]}),makeQuery(id+"F7.opExtrude","SWEPT_FACE",FACE,{"disambiguationData":[OSD([sQuery(id+"F6.wireOp",EDGE,"c00e0242-21cc-46da-ab10-4ac23868c1ae")])]})]});
            var Q183;
            Q183=makeQuery(id+"F7.boolean.opBoolean","INTERSECT",EDGE,{"disambiguationData":[OD(0.0)],"derivedFrom":[makeQuery(id+"F1.opExtrude","SWEPT_FACE",FACE,{"disambiguationData":[OSD([sQuery(id+"F0.wireOp",EDGE,"E0")])]}),makeQuery(id+"F7.opExtrude","SWEPT_FACE",FACE,{"disambiguationData":[OSD([sQuery(id+"F6.wireOp",EDGE,"b2934774-308d-449c-932f-3a1098ac2e13")])]})]});
            var Q184;
            Q184=makeQuery(id+"F7.boolean.opBoolean","INTERSECT",EDGE,{"disambiguationData":[OD(0.0)],"derivedFrom":[makeQuery(id+"F1.opExtrude","SWEPT_FACE",FACE,{"disambiguationData":[OSD([sQuery(id+"F0.wireOp",EDGE,"E0")])]}),makeQuery(id+"F7.opExtrude","SWEPT_FACE",FACE,{"disambiguationData":[OSD([sQuery(id+"F6.wireOp",EDGE,"080e9595-97ee-4677-8bd6-bafa410fbacd")])]})]});
            var Q185;
            Q185=makeQuery(id+"F7.boolean.opBoolean","INTERSECT",EDGE,{"disambiguationData":[OD(0.0)],"derivedFrom":[makeQuery(id+"F1.opExtrude","SWEPT_FACE",FACE,{"disambiguationData":[OSD([sQuery(id+"F0.wireOp",EDGE,"E0")])]}),makeQuery(id+"F7.opExtrude","SWEPT_FACE",FACE,{"disambiguationData":[OSD([sQuery(id+"F6.wireOp",EDGE,"dadb567b-1386-430c-9f3a-5fc8d100a7a2")])]})]});
            var Q186;
            Q186=makeQuery(id+"F7.boolean.opBoolean","INTERSECT",EDGE,{"disambiguationData":[OD(0.0)],"derivedFrom":[makeQuery(id+"F1.opExtrude","SWEPT_FACE",FACE,{"disambiguationData":[OSD([sQuery(id+"F0.wireOp",EDGE,"E0")])]}),makeQuery(id+"F7.opExtrude","SWEPT_FACE",FACE,{"disambiguationData":[OSD([sQuery(id+"F6.wireOp",EDGE,"b9266994-6da7-4218-b9b6-dc69dad9fbb6")])]})]});
            var Q187;
            Q187=makeQuery(id+"F7.boolean.opBoolean","INTERSECT",EDGE,{"disambiguationData":[OD(0.0)],"derivedFrom":[makeQuery(id+"F1.opExtrude","SWEPT_FACE",FACE,{"disambiguationData":[OSD([sQuery(id+"F0.wireOp",EDGE,"E0")])]}),makeQuery(id+"F7.opExtrude","SWEPT_FACE",FACE,{"disambiguationData":[OSD([sQuery(id+"F6.wireOp",EDGE,"9dd98ae6-2e30-47a1-ba76-83a55859fa92")])]})]});
            var Q188;
            Q188=makeQuery(id+"F7.boolean.opBoolean","INTERSECT",EDGE,{"disambiguationData":[OD(0.0)],"derivedFrom":[makeQuery(id+"F1.opExtrude","SWEPT_FACE",FACE,{"disambiguationData":[OSD([sQuery(id+"F0.wireOp",EDGE,"E0")])]}),makeQuery(id+"F7.opExtrude","SWEPT_FACE",FACE,{"disambiguationData":[OSD([sQuery(id+"F6.wireOp",EDGE,"e0db4643-829f-48a9-8eff-a25beb6ab781")])]})]});
            var Q189;
            Q189=makeQuery(id+"F7.boolean.opBoolean","INTERSECT",EDGE,{"disambiguationData":[OD(0.0)],"derivedFrom":[makeQuery(id+"F1.opExtrude","SWEPT_FACE",FACE,{"disambiguationData":[OSD([sQuery(id+"F0.wireOp",EDGE,"E0")])]}),makeQuery(id+"F7.opExtrude","SWEPT_FACE",FACE,{"disambiguationData":[OSD([sQuery(id+"F6.wireOp",EDGE,"f1bd9ad3-5cd4-4e3a-b3b8-e332278da6fa")])]})]});
            var Q190;
            Q190=makeQuery(id+"F10.boolean.opBoolean","INTERSECT",EDGE,{"disambiguationData":[OD(0.0)],"derivedFrom":[makeQuery(id+"F1.opExtrude","SWEPT_FACE",FACE,{"disambiguationData":[OSD([sQuery(id+"F0.wireOp",EDGE,"E0")])]}),makeQuery(id+"F10.opExtrude","SWEPT_FACE",FACE,{"disambiguationData":[OSD([sQuery(id+"F9.wireOp",EDGE,"cb8d6cfe-6865-4672-8e74-b6eabd104ceb")])]})]});
            var Q191;
            Q191=makeQuery(id+"F10.boolean.opBoolean","INTERSECT",EDGE,{"disambiguationData":[OD(0.0)],"derivedFrom":[makeQuery(id+"F1.opExtrude","SWEPT_FACE",FACE,{"disambiguationData":[OSD([sQuery(id+"F0.wireOp",EDGE,"E0")])]}),makeQuery(id+"F10.opExtrude","SWEPT_FACE",FACE,{"disambiguationData":[OSD([sQuery(id+"F9.wireOp",EDGE,"669bf558-646c-496e-bf26-3749fa86c7e1")])]})]});
            var Q192;
            Q192=makeQuery(id+"F10.boolean.opBoolean","INTERSECT",EDGE,{"disambiguationData":[OD(0.0)],"derivedFrom":[makeQuery(id+"F1.opExtrude","SWEPT_FACE",FACE,{"disambiguationData":[OSD([sQuery(id+"F0.wireOp",EDGE,"E0")])]}),makeQuery(id+"F10.opExtrude","SWEPT_FACE",FACE,{"disambiguationData":[OSD([sQuery(id+"F9.wireOp",EDGE,"0a28de13-28e8-4f33-8bdd-1a0962719dc5")])]})]});
            var Q193;
            Q193=makeQuery(id+"F10.boolean.opBoolean","INTERSECT",EDGE,{"disambiguationData":[OD(0.0)],"derivedFrom":[makeQuery(id+"F1.opExtrude","SWEPT_FACE",FACE,{"disambiguationData":[OSD([sQuery(id+"F0.wireOp",EDGE,"E0")])]}),makeQuery(id+"F10.opExtrude","SWEPT_FACE",FACE,{"disambiguationData":[OSD([sQuery(id+"F9.wireOp",EDGE,"3b8b2b28-c0e3-4522-9afb-7c7d64f31835")])]})]});
            var Q194;
            Q194=makeQuery(id+"F10.boolean.opBoolean","INTERSECT",EDGE,{"disambiguationData":[OD(0.0)],"derivedFrom":[makeQuery(id+"F1.opExtrude","SWEPT_FACE",FACE,{"disambiguationData":[OSD([sQuery(id+"F0.wireOp",EDGE,"E0")])]}),makeQuery(id+"F10.opExtrude","SWEPT_FACE",FACE,{"disambiguationData":[OSD([sQuery(id+"F9.wireOp",EDGE,"b5321248-a158-4813-ba77-dbdb8d777a1d")])]})]});
            var Q195;
            Q195=makeQuery(id+"F10.boolean.opBoolean","INTERSECT",EDGE,{"disambiguationData":[OD(0.0)],"derivedFrom":[makeQuery(id+"F1.opExtrude","SWEPT_FACE",FACE,{"disambiguationData":[OSD([sQuery(id+"F0.wireOp",EDGE,"E0")])]}),makeQuery(id+"F10.opExtrude","SWEPT_FACE",FACE,{"disambiguationData":[OSD([sQuery(id+"F9.wireOp",EDGE,"e5c3d3fb-08e1-497d-ac67-a5b448ee73d7")])]})]});
            var Q196;
            Q196=makeQuery(id+"F7.boolean.opBoolean","INTERSECT",EDGE,{"disambiguationData":[OD(0.0)],"derivedFrom":[makeQuery(id+"F1.opExtrude","SWEPT_FACE",FACE,{"disambiguationData":[OSD([sQuery(id+"F0.wireOp",EDGE,"E0")])]}),makeQuery(id+"F7.opExtrude","SWEPT_FACE",FACE,{"disambiguationData":[OSD([sQuery(id+"F6.wireOp",EDGE,"a546d2dc-2605-408c-b24e-faa2d271309e")])]})]});
            var Q197;
            Q197=makeQuery(id+"F7.boolean.opBoolean","INTERSECT",EDGE,{"disambiguationData":[OD(0.0)],"derivedFrom":[makeQuery(id+"F1.opExtrude","SWEPT_FACE",FACE,{"disambiguationData":[OSD([sQuery(id+"F0.wireOp",EDGE,"E0")])]}),makeQuery(id+"F7.opExtrude","SWEPT_FACE",FACE,{"disambiguationData":[OSD([sQuery(id+"F6.wireOp",EDGE,"83d52e6d-92a4-4648-8b46-e9a9552c27ba")])]})]});
            var Q198;
            Q198=makeQuery(id+"F7.boolean.opBoolean","INTERSECT",EDGE,{"disambiguationData":[OD(0.0)],"derivedFrom":[makeQuery(id+"F1.opExtrude","SWEPT_FACE",FACE,{"disambiguationData":[OSD([sQuery(id+"F0.wireOp",EDGE,"E0")])]}),makeQuery(id+"F7.opExtrude","SWEPT_FACE",FACE,{"disambiguationData":[OSD([sQuery(id+"F6.wireOp",EDGE,"3a394f99-872c-4196-87e6-3b072fe8ed46")])]})]});
            var Q199;
            Q199=makeQuery(id+"F7.boolean.opBoolean","INTERSECT",EDGE,{"disambiguationData":[OD(0.0)],"derivedFrom":[makeQuery(id+"F1.opExtrude","SWEPT_FACE",FACE,{"disambiguationData":[OSD([sQuery(id+"F0.wireOp",EDGE,"E0")])]}),makeQuery(id+"F7.opExtrude","SWEPT_FACE",FACE,{"disambiguationData":[OSD([sQuery(id+"F6.wireOp",EDGE,"dacff5a3-6968-4a67-9e75-63fe3a24236e")])]})]});
            var Q200;
            Q200=makeQuery(id+"F7.boolean.opBoolean","INTERSECT",EDGE,{"disambiguationData":[OD(0.0)],"derivedFrom":[makeQuery(id+"F1.opExtrude","SWEPT_FACE",FACE,{"disambiguationData":[OSD([sQuery(id+"F0.wireOp",EDGE,"E0")])]}),makeQuery(id+"F7.opExtrude","SWEPT_FACE",FACE,{"disambiguationData":[OSD([sQuery(id+"F6.wireOp",EDGE,"4bd018d2-9826-418d-bf88-deb3f47e7d26")])]})]});
            var Q201;
            Q201=makeQuery(id+"F7.boolean.opBoolean","INTERSECT",EDGE,{"disambiguationData":[OD(0.0)],"derivedFrom":[makeQuery(id+"F1.opExtrude","SWEPT_FACE",FACE,{"disambiguationData":[OSD([sQuery(id+"F0.wireOp",EDGE,"E0")])]}),makeQuery(id+"F7.opExtrude","SWEPT_FACE",FACE,{"disambiguationData":[OSD([sQuery(id+"F6.wireOp",EDGE,"688fe3da-c086-43d2-9b33-13069743b833")])]})]});
            var Q202;
            Q202=makeQuery(id+"F10.boolean.opBoolean","INTERSECT",EDGE,{"disambiguationData":[OD(0.0)],"derivedFrom":[makeQuery(id+"F1.opExtrude","SWEPT_FACE",FACE,{"disambiguationData":[OSD([sQuery(id+"F0.wireOp",EDGE,"E0")])]}),makeQuery(id+"F10.opExtrude","SWEPT_FACE",FACE,{"disambiguationData":[OSD([sQuery(id+"F9.wireOp",EDGE,"7b52eed1-5e93-4795-8e62-8c7c827c961c")])]})]});
            var Q203;
            Q203=makeQuery(id+"F10.boolean.opBoolean","INTERSECT",EDGE,{"disambiguationData":[OD(0.0)],"derivedFrom":[makeQuery(id+"F1.opExtrude","SWEPT_FACE",FACE,{"disambiguationData":[OSD([sQuery(id+"F0.wireOp",EDGE,"E0")])]}),makeQuery(id+"F10.opExtrude","SWEPT_FACE",FACE,{"disambiguationData":[OSD([sQuery(id+"F9.wireOp",EDGE,"121e2676-15f0-40c4-bdde-db49c7b0ce91")])]})]});
            var Q204;
            Q204=makeQuery(id+"F10.boolean.opBoolean","INTERSECT",EDGE,{"disambiguationData":[OD(0.0)],"derivedFrom":[makeQuery(id+"F1.opExtrude","SWEPT_FACE",FACE,{"disambiguationData":[OSD([sQuery(id+"F0.wireOp",EDGE,"E0")])]}),makeQuery(id+"F10.opExtrude","SWEPT_FACE",FACE,{"disambiguationData":[OSD([sQuery(id+"F9.wireOp",EDGE,"6c8742e6-57ac-4896-b350-d79696f56fd6")])]})]});
            var Q205;
            Q205=makeQuery(id+"F10.boolean.opBoolean","INTERSECT",EDGE,{"disambiguationData":[OD(0.0)],"derivedFrom":[makeQuery(id+"F1.opExtrude","SWEPT_FACE",FACE,{"disambiguationData":[OSD([sQuery(id+"F0.wireOp",EDGE,"E0")])]}),makeQuery(id+"F10.opExtrude","SWEPT_FACE",FACE,{"disambiguationData":[OSD([sQuery(id+"F9.wireOp",EDGE,"abb82f81-c2b7-42e4-b461-f70187babd0f")])]})]});
            var Q206;
            Q206=makeQuery(id+"F10.boolean.opBoolean","INTERSECT",EDGE,{"disambiguationData":[OD(0.0)],"derivedFrom":[makeQuery(id+"F1.opExtrude","SWEPT_FACE",FACE,{"disambiguationData":[OSD([sQuery(id+"F0.wireOp",EDGE,"E0")])]}),makeQuery(id+"F10.opExtrude","SWEPT_FACE",FACE,{"disambiguationData":[OSD([sQuery(id+"F9.wireOp",EDGE,"60341486-7ff5-44b2-945d-25077e210a42")])]})]});
            var Q207;
            Q207=makeQuery(id+"F10.boolean.opBoolean","INTERSECT",EDGE,{"disambiguationData":[OD(0.0)],"derivedFrom":[makeQuery(id+"F1.opExtrude","SWEPT_FACE",FACE,{"disambiguationData":[OSD([sQuery(id+"F0.wireOp",EDGE,"E0")])]}),makeQuery(id+"F10.opExtrude","SWEPT_FACE",FACE,{"disambiguationData":[OSD([sQuery(id+"F9.wireOp",EDGE,"22d36337-f6bf-46cf-8a45-76c05130d686")])]})]});
            var Q208;
            Q208=makeQuery(id+"F10.boolean.opBoolean","INTERSECT",EDGE,{"disambiguationData":[OD(0.0)],"derivedFrom":[makeQuery(id+"F1.opExtrude","SWEPT_FACE",FACE,{"disambiguationData":[OSD([sQuery(id+"F0.wireOp",EDGE,"E0")])]}),makeQuery(id+"F10.opExtrude","SWEPT_FACE",FACE,{"disambiguationData":[OSD([sQuery(id+"F9.wireOp",EDGE,"5e611113-fa52-45c0-bc99-d49581cd234e")])]})]});
            var Q209;
            Q209=makeQuery(id+"F10.boolean.opBoolean","INTERSECT",EDGE,{"disambiguationData":[OD(0.0)],"derivedFrom":[makeQuery(id+"F1.opExtrude","SWEPT_FACE",FACE,{"disambiguationData":[OSD([sQuery(id+"F0.wireOp",EDGE,"E0")])]}),makeQuery(id+"F10.opExtrude","SWEPT_FACE",FACE,{"disambiguationData":[OSD([sQuery(id+"F9.wireOp",EDGE,"1215eb1f-7712-420f-9f37-3d618c989f06")])]})]});
            var Q210;
            Q210=makeQuery(id+"F10.boolean.opBoolean","INTERSECT",EDGE,{"disambiguationData":[OD(0.0)],"derivedFrom":[makeQuery(id+"F1.opExtrude","SWEPT_FACE",FACE,{"disambiguationData":[OSD([sQuery(id+"F0.wireOp",EDGE,"E0")])]}),makeQuery(id+"F10.opExtrude","SWEPT_FACE",FACE,{"disambiguationData":[OSD([sQuery(id+"F9.wireOp",EDGE,"f9cdae2c-dfee-4b7b-8cfa-af8311c95cb8")])]})]});
            var Q211;
            Q211=makeQuery(id+"F10.boolean.opBoolean","INTERSECT",EDGE,{"disambiguationData":[OD(0.0)],"derivedFrom":[makeQuery(id+"F1.opExtrude","SWEPT_FACE",FACE,{"disambiguationData":[OSD([sQuery(id+"F0.wireOp",EDGE,"E0")])]}),makeQuery(id+"F10.opExtrude","SWEPT_FACE",FACE,{"disambiguationData":[OSD([sQuery(id+"F9.wireOp",EDGE,"9c5e5121-c6ac-4869-af42-ed4733e390cc")])]})]});
            var Q212;
            Q212=makeQuery(id+"F10.boolean.opBoolean","INTERSECT",EDGE,{"disambiguationData":[OD(0.0)],"derivedFrom":[makeQuery(id+"F1.opExtrude","SWEPT_FACE",FACE,{"disambiguationData":[OSD([sQuery(id+"F0.wireOp",EDGE,"E0")])]}),makeQuery(id+"F10.opExtrude","SWEPT_FACE",FACE,{"disambiguationData":[OSD([sQuery(id+"F9.wireOp",EDGE,"1c791c94-9947-4f29-8c52-677e286b93e0")])]})]});
            var Q213;
            Q213=makeQuery(id+"F10.boolean.opBoolean","INTERSECT",EDGE,{"disambiguationData":[OD(0.0)],"derivedFrom":[makeQuery(id+"F1.opExtrude","SWEPT_FACE",FACE,{"disambiguationData":[OSD([sQuery(id+"F0.wireOp",EDGE,"E0")])]}),makeQuery(id+"F10.opExtrude","SWEPT_FACE",FACE,{"disambiguationData":[OSD([sQuery(id+"F9.wireOp",EDGE,"b11a55d2-776c-4cc8-9330-3b53156f9da6")])]})]});
            var Q214;
            Q214=makeQuery(id+"F7.boolean.opBoolean","INTERSECT",EDGE,{"disambiguationData":[OD(0.0)],"derivedFrom":[makeQuery(id+"F1.opExtrude","SWEPT_FACE",FACE,{"disambiguationData":[OSD([sQuery(id+"F0.wireOp",EDGE,"E0")])]}),makeQuery(id+"F7.opExtrude","SWEPT_FACE",FACE,{"disambiguationData":[OSD([sQuery(id+"F6.wireOp",EDGE,"81ec299c-6d5d-4c24-8a4f-7c4c23e1b546")])]})]});
            var Q215;
            Q215=makeQuery(id+"F7.boolean.opBoolean","INTERSECT",EDGE,{"disambiguationData":[OD(0.0)],"derivedFrom":[makeQuery(id+"F1.opExtrude","SWEPT_FACE",FACE,{"disambiguationData":[OSD([sQuery(id+"F0.wireOp",EDGE,"E0")])]}),makeQuery(id+"F7.opExtrude","SWEPT_FACE",FACE,{"disambiguationData":[OSD([sQuery(id+"F6.wireOp",EDGE,"82e6de43-fa50-4c70-abab-f4b9416176ad")])]})]});
            var Q216;
            Q216=makeQuery(id+"F7.boolean.opBoolean","INTERSECT",EDGE,{"disambiguationData":[OD(0.0)],"derivedFrom":[makeQuery(id+"F1.opExtrude","SWEPT_FACE",FACE,{"disambiguationData":[OSD([sQuery(id+"F0.wireOp",EDGE,"E0")])]}),makeQuery(id+"F7.opExtrude","SWEPT_FACE",FACE,{"disambiguationData":[OSD([sQuery(id+"F6.wireOp",EDGE,"7f228a5c-a083-4118-82ee-67a40d784e87")])]})]});
            var Q217;
            Q217=makeQuery(id+"F7.boolean.opBoolean","INTERSECT",EDGE,{"disambiguationData":[OD(0.0)],"derivedFrom":[makeQuery(id+"F1.opExtrude","SWEPT_FACE",FACE,{"disambiguationData":[OSD([sQuery(id+"F0.wireOp",EDGE,"E0")])]}),makeQuery(id+"F7.opExtrude","SWEPT_FACE",FACE,{"disambiguationData":[OSD([sQuery(id+"F6.wireOp",EDGE,"07bcde23-f94c-47bd-99ba-0344f469b981")])]})]});
            var Q218;
            Q218=makeQuery(id+"F7.boolean.opBoolean","INTERSECT",EDGE,{"disambiguationData":[OD(0.0)],"derivedFrom":[makeQuery(id+"F1.opExtrude","SWEPT_FACE",FACE,{"disambiguationData":[OSD([sQuery(id+"F0.wireOp",EDGE,"E0")])]}),makeQuery(id+"F7.opExtrude","SWEPT_FACE",FACE,{"disambiguationData":[OSD([sQuery(id+"F6.wireOp",EDGE,"2b333a8c-11cd-4584-9d3f-b39d69e47acf")])]})]});
            var Q219;
            Q219=makeQuery(id+"F7.boolean.opBoolean","INTERSECT",EDGE,{"disambiguationData":[OD(0.0)],"derivedFrom":[makeQuery(id+"F1.opExtrude","SWEPT_FACE",FACE,{"disambiguationData":[OSD([sQuery(id+"F0.wireOp",EDGE,"E0")])]}),makeQuery(id+"F7.opExtrude","SWEPT_FACE",FACE,{"disambiguationData":[OSD([sQuery(id+"F6.wireOp",EDGE,"f91ae07e-f7fe-47d5-8632-f1a35ba81e8f")])]})]});
            var Q220;
            Q220=makeQuery(id+"F10.boolean.opBoolean","INTERSECT",EDGE,{"disambiguationData":[OD(0.0)],"derivedFrom":[makeQuery(id+"F1.opExtrude","SWEPT_FACE",FACE,{"disambiguationData":[OSD([sQuery(id+"F0.wireOp",EDGE,"E0")])]}),makeQuery(id+"F10.opExtrude","SWEPT_FACE",FACE,{"disambiguationData":[OSD([sQuery(id+"F9.wireOp",EDGE,"6096a3ce-5044-48b5-a349-b3a0c47d5e99")])]})]});
            var Q221;
            Q221=makeQuery(id+"F10.boolean.opBoolean","INTERSECT",EDGE,{"disambiguationData":[OD(0.0)],"derivedFrom":[makeQuery(id+"F1.opExtrude","SWEPT_FACE",FACE,{"disambiguationData":[OSD([sQuery(id+"F0.wireOp",EDGE,"E0")])]}),makeQuery(id+"F10.opExtrude","SWEPT_FACE",FACE,{"disambiguationData":[OSD([sQuery(id+"F9.wireOp",EDGE,"9a94c099-41bb-40ba-894c-4f3c7a0eafbb")])]})]});
            var Q222;
            Q222=makeQuery(id+"F10.boolean.opBoolean","INTERSECT",EDGE,{"disambiguationData":[OD(0.0)],"derivedFrom":[makeQuery(id+"F1.opExtrude","SWEPT_FACE",FACE,{"disambiguationData":[OSD([sQuery(id+"F0.wireOp",EDGE,"E0")])]}),makeQuery(id+"F10.opExtrude","SWEPT_FACE",FACE,{"disambiguationData":[OSD([sQuery(id+"F9.wireOp",EDGE,"2796c508-b6ce-4770-b208-7c59b8d85fbc")])]})]});
            var Q223;
            Q223=makeQuery(id+"F10.boolean.opBoolean","INTERSECT",EDGE,{"disambiguationData":[OD(0.0)],"derivedFrom":[makeQuery(id+"F1.opExtrude","SWEPT_FACE",FACE,{"disambiguationData":[OSD([sQuery(id+"F0.wireOp",EDGE,"E0")])]}),makeQuery(id+"F10.opExtrude","SWEPT_FACE",FACE,{"disambiguationData":[OSD([sQuery(id+"F9.wireOp",EDGE,"2e52e4ba-a856-43cc-8b69-bc95ae584be1")])]})]});
            var Q224;
            Q224=makeQuery(id+"F10.boolean.opBoolean","INTERSECT",EDGE,{"disambiguationData":[OD(0.0)],"derivedFrom":[makeQuery(id+"F1.opExtrude","SWEPT_FACE",FACE,{"disambiguationData":[OSD([sQuery(id+"F0.wireOp",EDGE,"E0")])]}),makeQuery(id+"F10.opExtrude","SWEPT_FACE",FACE,{"disambiguationData":[OSD([sQuery(id+"F9.wireOp",EDGE,"d68f23c5-fa44-4f68-a5e1-914856eae846")])]})]});
            var Q225;
            Q225=makeQuery(id+"F10.boolean.opBoolean","INTERSECT",EDGE,{"disambiguationData":[OD(0.0)],"derivedFrom":[makeQuery(id+"F1.opExtrude","SWEPT_FACE",FACE,{"disambiguationData":[OSD([sQuery(id+"F0.wireOp",EDGE,"E0")])]}),makeQuery(id+"F10.opExtrude","SWEPT_FACE",FACE,{"disambiguationData":[OSD([sQuery(id+"F9.wireOp",EDGE,"3921cf77-2c7d-4081-b0dc-8dd1674662ff")])]})]});
            var Q226;
            Q226=makeQuery(id+"F7.boolean.opBoolean","INTERSECT",EDGE,{"disambiguationData":[OD(0.0)],"derivedFrom":[makeQuery(id+"F1.opExtrude","SWEPT_FACE",FACE,{"disambiguationData":[OSD([sQuery(id+"F0.wireOp",EDGE,"E0")])]}),makeQuery(id+"F7.opExtrude","SWEPT_FACE",FACE,{"disambiguationData":[OSD([sQuery(id+"F6.wireOp",EDGE,"1f1a9126-4da4-4afe-b3b0-61ea06e02878")])]})]});
            var Q227;
            Q227=makeQuery(id+"F7.boolean.opBoolean","INTERSECT",EDGE,{"disambiguationData":[OD(0.0)],"derivedFrom":[makeQuery(id+"F1.opExtrude","SWEPT_FACE",FACE,{"disambiguationData":[OSD([sQuery(id+"F0.wireOp",EDGE,"E0")])]}),makeQuery(id+"F7.opExtrude","SWEPT_FACE",FACE,{"disambiguationData":[OSD([sQuery(id+"F6.wireOp",EDGE,"fd6a0418-0a5b-4901-b5a5-5e60565ddb8d")])]})]});
            var Q228;
            Q228=makeQuery(id+"F7.boolean.opBoolean","INTERSECT",EDGE,{"disambiguationData":[OD(0.0)],"derivedFrom":[makeQuery(id+"F1.opExtrude","SWEPT_FACE",FACE,{"disambiguationData":[OSD([sQuery(id+"F0.wireOp",EDGE,"E0")])]}),makeQuery(id+"F7.opExtrude","SWEPT_FACE",FACE,{"disambiguationData":[OSD([sQuery(id+"F6.wireOp",EDGE,"88fd7354-daea-4d87-87de-3f4d9154d1db")])]})]});
            var Q229;
            Q229=makeQuery(id+"F7.boolean.opBoolean","INTERSECT",EDGE,{"disambiguationData":[OD(0.0)],"derivedFrom":[makeQuery(id+"F1.opExtrude","SWEPT_FACE",FACE,{"disambiguationData":[OSD([sQuery(id+"F0.wireOp",EDGE,"E0")])]}),makeQuery(id+"F7.opExtrude","SWEPT_FACE",FACE,{"disambiguationData":[OSD([sQuery(id+"F6.wireOp",EDGE,"e686fd54-ae98-4f09-90c8-07cd4bd11a16")])]})]});
            var Q230;
            Q230=makeQuery(id+"F7.boolean.opBoolean","INTERSECT",EDGE,{"disambiguationData":[OD(0.0)],"derivedFrom":[makeQuery(id+"F1.opExtrude","SWEPT_FACE",FACE,{"disambiguationData":[OSD([sQuery(id+"F0.wireOp",EDGE,"E0")])]}),makeQuery(id+"F7.opExtrude","SWEPT_FACE",FACE,{"disambiguationData":[OSD([sQuery(id+"F6.wireOp",EDGE,"08b58334-56ca-40a0-8f56-63621d04fc0f")])]})]});
            var Q231;
            Q231=makeQuery(id+"F7.boolean.opBoolean","INTERSECT",EDGE,{"disambiguationData":[OD(0.0)],"derivedFrom":[makeQuery(id+"F1.opExtrude","SWEPT_FACE",FACE,{"disambiguationData":[OSD([sQuery(id+"F0.wireOp",EDGE,"E0")])]}),makeQuery(id+"F7.opExtrude","SWEPT_FACE",FACE,{"disambiguationData":[OSD([sQuery(id+"F6.wireOp",EDGE,"cd7f04d2-3622-47ae-9a04-707a5ea18902")])]})]});
            var Q232;
            Q232=makeQuery(id+"F10.boolean.opBoolean","INTERSECT",EDGE,{"disambiguationData":[OD(0.0)],"derivedFrom":[makeQuery(id+"F1.opExtrude","SWEPT_FACE",FACE,{"disambiguationData":[OSD([sQuery(id+"F0.wireOp",EDGE,"E0")])]}),makeQuery(id+"F10.opExtrude","SWEPT_FACE",FACE,{"disambiguationData":[OSD([sQuery(id+"F9.wireOp",EDGE,"d83faa9b-d45e-407d-93d1-fc8e5d4eca17")])]})]});
            var Q233;
            Q233=makeQuery(id+"F10.boolean.opBoolean","INTERSECT",EDGE,{"disambiguationData":[OD(0.0)],"derivedFrom":[makeQuery(id+"F1.opExtrude","SWEPT_FACE",FACE,{"disambiguationData":[OSD([sQuery(id+"F0.wireOp",EDGE,"E0")])]}),makeQuery(id+"F10.opExtrude","SWEPT_FACE",FACE,{"disambiguationData":[OSD([sQuery(id+"F9.wireOp",EDGE,"0bb9bc1b-8636-4d55-a596-8fb459d88000")])]})]});
            var Q234;
            Q234=makeQuery(id+"F10.boolean.opBoolean","INTERSECT",EDGE,{"disambiguationData":[OD(0.0)],"derivedFrom":[makeQuery(id+"F1.opExtrude","SWEPT_FACE",FACE,{"disambiguationData":[OSD([sQuery(id+"F0.wireOp",EDGE,"E0")])]}),makeQuery(id+"F10.opExtrude","SWEPT_FACE",FACE,{"disambiguationData":[OSD([sQuery(id+"F9.wireOp",EDGE,"de8f1f6c-7dc9-478c-a1e7-a0d904edc68b")])]})]});
            var Q235;
            Q235=makeQuery(id+"F10.boolean.opBoolean","INTERSECT",EDGE,{"disambiguationData":[OD(0.0)],"derivedFrom":[makeQuery(id+"F1.opExtrude","SWEPT_FACE",FACE,{"disambiguationData":[OSD([sQuery(id+"F0.wireOp",EDGE,"E0")])]}),makeQuery(id+"F10.opExtrude","SWEPT_FACE",FACE,{"disambiguationData":[OSD([sQuery(id+"F9.wireOp",EDGE,"4b50f863-6222-4670-ab38-0f94a0e4d076")])]})]});
            var Q236;
            Q236=makeQuery(id+"F10.boolean.opBoolean","INTERSECT",EDGE,{"disambiguationData":[OD(0.0)],"derivedFrom":[makeQuery(id+"F1.opExtrude","SWEPT_FACE",FACE,{"disambiguationData":[OSD([sQuery(id+"F0.wireOp",EDGE,"E0")])]}),makeQuery(id+"F10.opExtrude","SWEPT_FACE",FACE,{"disambiguationData":[OSD([sQuery(id+"F9.wireOp",EDGE,"f2b9081a-a049-4a09-bb62-bcd79e53e865")])]})]});
            var Q237;
            Q237=makeQuery(id+"F10.boolean.opBoolean","INTERSECT",EDGE,{"disambiguationData":[OD(0.0)],"derivedFrom":[makeQuery(id+"F1.opExtrude","SWEPT_FACE",FACE,{"disambiguationData":[OSD([sQuery(id+"F0.wireOp",EDGE,"E0")])]}),makeQuery(id+"F10.opExtrude","SWEPT_FACE",FACE,{"disambiguationData":[OSD([sQuery(id+"F9.wireOp",EDGE,"6a67a89a-99b4-4420-acea-3905a5a2b65e")])]})]});
            var Q238;
            Q238=makeQuery(id+"F7.boolean.opBoolean","INTERSECT",EDGE,{"disambiguationData":[OD(0.0)],"derivedFrom":[makeQuery(id+"F1.opExtrude","SWEPT_FACE",FACE,{"disambiguationData":[OSD([sQuery(id+"F0.wireOp",EDGE,"E0")])]}),makeQuery(id+"F7.opExtrude","SWEPT_FACE",FACE,{"disambiguationData":[OSD([sQuery(id+"F6.wireOp",EDGE,"90d9cdbb-a078-4297-bb66-39e745c2c8dc")])]})]});
            var Q239;
            Q239=makeQuery(id+"F7.boolean.opBoolean","INTERSECT",EDGE,{"disambiguationData":[OD(0.0)],"derivedFrom":[makeQuery(id+"F1.opExtrude","SWEPT_FACE",FACE,{"disambiguationData":[OSD([sQuery(id+"F0.wireOp",EDGE,"E0")])]}),makeQuery(id+"F7.opExtrude","SWEPT_FACE",FACE,{"disambiguationData":[OSD([sQuery(id+"F6.wireOp",EDGE,"869f0f0d-0ab4-4e92-8b7b-8667710e2349")])]})]});
            var Q240;
            Q240=makeQuery(id+"F7.boolean.opBoolean","INTERSECT",EDGE,{"disambiguationData":[OD(0.0)],"derivedFrom":[makeQuery(id+"F1.opExtrude","SWEPT_FACE",FACE,{"disambiguationData":[OSD([sQuery(id+"F0.wireOp",EDGE,"E0")])]}),makeQuery(id+"F7.opExtrude","SWEPT_FACE",FACE,{"disambiguationData":[OSD([sQuery(id+"F6.wireOp",EDGE,"14efab8d-e5b4-4b99-a3b8-db90cb956341")])]})]});
            var Q241;
            Q241=makeQuery(id+"F7.boolean.opBoolean","INTERSECT",EDGE,{"disambiguationData":[OD(0.0)],"derivedFrom":[makeQuery(id+"F1.opExtrude","SWEPT_FACE",FACE,{"disambiguationData":[OSD([sQuery(id+"F0.wireOp",EDGE,"E0")])]}),makeQuery(id+"F7.opExtrude","SWEPT_FACE",FACE,{"disambiguationData":[OSD([sQuery(id+"F6.wireOp",EDGE,"a2e2d135-410d-43f5-bfc8-0a9909259d6e")])]})]});
            var Q242;
            Q242=makeQuery(id+"F7.boolean.opBoolean","INTERSECT",EDGE,{"disambiguationData":[OD(0.0)],"derivedFrom":[makeQuery(id+"F1.opExtrude","SWEPT_FACE",FACE,{"disambiguationData":[OSD([sQuery(id+"F0.wireOp",EDGE,"E0")])]}),makeQuery(id+"F7.opExtrude","SWEPT_FACE",FACE,{"disambiguationData":[OSD([sQuery(id+"F6.wireOp",EDGE,"6f801692-b756-4057-a928-afc3f0341116")])]})]});
            var Q243;
            Q243=makeQuery(id+"F7.boolean.opBoolean","INTERSECT",EDGE,{"disambiguationData":[OD(0.0)],"derivedFrom":[makeQuery(id+"F1.opExtrude","SWEPT_FACE",FACE,{"disambiguationData":[OSD([sQuery(id+"F0.wireOp",EDGE,"E0")])]}),makeQuery(id+"F7.opExtrude","SWEPT_FACE",FACE,{"disambiguationData":[OSD([sQuery(id+"F6.wireOp",EDGE,"305cdedf-1ec9-4fee-9b59-03e7a0ef637e")])]})]});
            var Q244;
            Q244=makeQuery(id+"F7.boolean.opBoolean","INTERSECT",EDGE,{"disambiguationData":[OD(0.0)],"derivedFrom":[makeQuery(id+"F1.opExtrude","SWEPT_FACE",FACE,{"disambiguationData":[OSD([sQuery(id+"F0.wireOp",EDGE,"E0")])]}),makeQuery(id+"F7.opExtrude","SWEPT_FACE",FACE,{"disambiguationData":[OSD([sQuery(id+"F6.wireOp",EDGE,"14efab8d-e5b4-4b99-a3b8-db90cb956341")])]})]});
            var Q245;
            Q245=makeQuery(id+"F7.boolean.opBoolean","INTERSECT",EDGE,{"disambiguationData":[OD(0.0)],"derivedFrom":[makeQuery(id+"F1.opExtrude","SWEPT_FACE",FACE,{"disambiguationData":[OSD([sQuery(id+"F0.wireOp",EDGE,"E0")])]}),makeQuery(id+"F7.opExtrude","SWEPT_FACE",FACE,{"disambiguationData":[OSD([sQuery(id+"F6.wireOp",EDGE,"65326cb1-3073-4610-b18b-feae14be5c13")])]})]});
            var Q246;
            Q246=makeQuery(id+"F7.boolean.opBoolean","INTERSECT",EDGE,{"disambiguationData":[OD(0.0)],"derivedFrom":[makeQuery(id+"F1.opExtrude","SWEPT_FACE",FACE,{"disambiguationData":[OSD([sQuery(id+"F0.wireOp",EDGE,"E0")])]}),makeQuery(id+"F7.opExtrude","SWEPT_FACE",FACE,{"disambiguationData":[OSD([sQuery(id+"F6.wireOp",EDGE,"f8088e12-c72b-4b3d-90fb-837d882fcbba")])]})]});
            var Q247;
            Q247=makeQuery(id+"F7.boolean.opBoolean","INTERSECT",EDGE,{"disambiguationData":[OD(0.0)],"derivedFrom":[makeQuery(id+"F1.opExtrude","SWEPT_FACE",FACE,{"disambiguationData":[OSD([sQuery(id+"F0.wireOp",EDGE,"E0")])]}),makeQuery(id+"F7.opExtrude","SWEPT_FACE",FACE,{"disambiguationData":[OSD([sQuery(id+"F6.wireOp",EDGE,"3024085b-1277-45ff-89f3-f8cc26ec2f35")])]})]});
            var Q248;
            Q248=makeQuery(id+"F7.boolean.opBoolean","INTERSECT",EDGE,{"disambiguationData":[OD(0.0)],"derivedFrom":[makeQuery(id+"F1.opExtrude","SWEPT_FACE",FACE,{"disambiguationData":[OSD([sQuery(id+"F0.wireOp",EDGE,"E0")])]}),makeQuery(id+"F7.opExtrude","SWEPT_FACE",FACE,{"disambiguationData":[OSD([sQuery(id+"F6.wireOp",EDGE,"00d8fb87-0f4c-424d-839c-7e7ec4f3fd4c")])]})]});
            var Q249;
            Q249=makeQuery(id+"F7.boolean.opBoolean","INTERSECT",EDGE,{"disambiguationData":[OD(0.0)],"derivedFrom":[makeQuery(id+"F1.opExtrude","SWEPT_FACE",FACE,{"disambiguationData":[OSD([sQuery(id+"F0.wireOp",EDGE,"E0")])]}),makeQuery(id+"F7.opExtrude","SWEPT_FACE",FACE,{"disambiguationData":[OSD([sQuery(id+"F6.wireOp",EDGE,"75183ba1-81fe-4bd2-98a4-39212aa8f21d")])]})]});
            var Q250;
            Q250=makeQuery(id+"F7.boolean.opBoolean","INTERSECT",EDGE,{"disambiguationData":[OD(0.0)],"derivedFrom":[makeQuery(id+"F1.opExtrude","SWEPT_FACE",FACE,{"disambiguationData":[OSD([sQuery(id+"F0.wireOp",EDGE,"E0")])]}),makeQuery(id+"F7.opExtrude","SWEPT_FACE",FACE,{"disambiguationData":[OSD([sQuery(id+"F6.wireOp",EDGE,"a0acb2da-2927-4627-867c-5d33e32ae2f5")])]})]});
            var Q251;
            Q251=makeQuery(id+"F10.boolean.opBoolean","INTERSECT",EDGE,{"disambiguationData":[OD(0.0)],"derivedFrom":[makeQuery(id+"F1.opExtrude","SWEPT_FACE",FACE,{"disambiguationData":[OSD([sQuery(id+"F0.wireOp",EDGE,"E0")])]}),makeQuery(id+"F10.opExtrude","SWEPT_FACE",FACE,{"disambiguationData":[OSD([sQuery(id+"F9.wireOp",EDGE,"043d117d-676f-48b6-932c-ed189ea02d01")])]})]});
            var Q252;
            Q252=makeQuery(id+"F10.boolean.opBoolean","INTERSECT",EDGE,{"disambiguationData":[OD(0.0)],"derivedFrom":[makeQuery(id+"F1.opExtrude","SWEPT_FACE",FACE,{"disambiguationData":[OSD([sQuery(id+"F0.wireOp",EDGE,"E0")])]}),makeQuery(id+"F10.opExtrude","SWEPT_FACE",FACE,{"disambiguationData":[OSD([sQuery(id+"F9.wireOp",EDGE,"I1SNvpHa-ovKs-9DXm-2cYc-TDOwp1cF8JiJ")])]})]});
            var Q253;
            Q253=makeQuery(id+"F10.boolean.opBoolean","INTERSECT",EDGE,{"disambiguationData":[OD(0.0)],"derivedFrom":[makeQuery(id+"F1.opExtrude","SWEPT_FACE",FACE,{"disambiguationData":[OSD([sQuery(id+"F0.wireOp",EDGE,"E0")])]}),makeQuery(id+"F10.opExtrude","SWEPT_FACE",FACE,{"disambiguationData":[OSD([sQuery(id+"F9.wireOp",EDGE,"ThbpAlgf-J1ZK-8EEi-tm60-MKaAh34L7w5e"),sQuery(id+"F9.wireOp",EDGE,"h7cyK7oW-8o4M-WHfY-pIGo-xKwypN2QV7Za")])]})]});
            var Q254;
            Q254=makeQuery(id+"F10.boolean.opBoolean","INTERSECT",EDGE,{"disambiguationData":[OD(0.0)],"derivedFrom":[makeQuery(id+"F1.opExtrude","SWEPT_FACE",FACE,{"disambiguationData":[OSD([sQuery(id+"F0.wireOp",EDGE,"E0")])]}),makeQuery(id+"F10.opExtrude","SWEPT_FACE",FACE,{"disambiguationData":[OSD([sQuery(id+"F9.wireOp",EDGE,"YlMJEoje-hVPp-NrIK-c2S6-AKWunBmpYVRp")])]})]});
            var Q255;
            Q255=makeQuery(id+"F12.boolean.opBoolean","INTERSECT",EDGE,{"derivedFrom":[makeQuery(id+"F1.opExtrude","SWEPT_FACE",FACE,{"disambiguationData":[OSD([sQuery(id+"F0.wireOp",EDGE,"E0")])]}),makeQuery(id+"F12.opExtrude","SWEPT_FACE",FACE,{"disambiguationData":[OSD([sQuery(id+"F11.wireOp",EDGE,"ea7ba490-2a23-4636-bf66-31f082130ce2"),sQuery(id+"F11.wireOp",EDGE,"7865739c-c3e9-4b94-9baf-c32e4e0c586f")])]})]});
            var Q256;
            Q256=makeQuery(id+"F12.boolean.opBoolean","INTERSECT",EDGE,{"derivedFrom":[makeQuery(id+"F1.opExtrude","SWEPT_FACE",FACE,{"disambiguationData":[OSD([sQuery(id+"F0.wireOp",EDGE,"E0")])]}),makeQuery(id+"F12.opExtrude","SWEPT_FACE",FACE,{"disambiguationData":[OSD([sQuery(id+"F11.wireOp",EDGE,"34c2dada-d6a9-419e-92ec-ab1ef5f216ab")])]})]});
            var Q257;
            Q257=makeQuery(id+"F12.boolean.opBoolean","INTERSECT",EDGE,{"derivedFrom":[makeQuery(id+"F1.opExtrude","SWEPT_FACE",FACE,{"disambiguationData":[OSD([sQuery(id+"F0.wireOp",EDGE,"E0")])]}),makeQuery(id+"F12.opExtrude","SWEPT_FACE",FACE,{"disambiguationData":[OSD([sQuery(id+"F11.wireOp",EDGE,"db216c74-79ea-496e-b24d-2c971d5c719f")])]})]});
            var Q258;
            Q258=makeQuery(id+"F12.boolean.opBoolean","INTERSECT",EDGE,{"derivedFrom":[makeQuery(id+"F1.opExtrude","SWEPT_FACE",FACE,{"disambiguationData":[OSD([sQuery(id+"F0.wireOp",EDGE,"E0")])]}),makeQuery(id+"F12.opExtrude","SWEPT_FACE",FACE,{"disambiguationData":[OSD([sQuery(id+"F11.wireOp",EDGE,"2cbe05a2-fc25-4f97-b96c-8479a1089892")])]})]});
            var Q259;
            Q259=makeQuery(id+"F5.boolean.opBoolean","INTERSECT",EDGE,{"disambiguationData":[OD(1.0)],"derivedFrom":[makeQuery(id+"F1.opExtrude","SWEPT_FACE",FACE,{"disambiguationData":[OSD([sQuery(id+"F0.wireOp",EDGE,"E0")])]}),makeQuery(id+"F5.opExtrude","SWEPT_FACE",FACE,{"disambiguationData":[OSD([sQuery(id+"F4.wireOp",EDGE,"57a90445-0bd0-490a-9b1f-698a67fd895c")])]})]});
            var Q260;
            Q260=makeQuery(id+"F5.boolean.opBoolean","INTERSECT",EDGE,{"disambiguationData":[OD(1.0)],"derivedFrom":[makeQuery(id+"F1.opExtrude","SWEPT_FACE",FACE,{"disambiguationData":[OSD([sQuery(id+"F0.wireOp",EDGE,"E0")])]}),makeQuery(id+"F5.opExtrude","SWEPT_FACE",FACE,{"disambiguationData":[OSD([sQuery(id+"F4.wireOp",EDGE,"0cf69e63-39ca-4a42-b99a-dd0b7aa5f2af")])]})]});
            var Q261;
            Q261=makeQuery(id+"F5.boolean.opBoolean","INTERSECT",EDGE,{"disambiguationData":[OD(1.0)],"derivedFrom":[makeQuery(id+"F1.opExtrude","SWEPT_FACE",FACE,{"disambiguationData":[OSD([sQuery(id+"F0.wireOp",EDGE,"E0")])]}),makeQuery(id+"F5.opExtrude","SWEPT_FACE",FACE,{"disambiguationData":[OSD([sQuery(id+"F4.wireOp",EDGE,"f230033e-8e97-4c48-a61c-878d7d3044cc")])]})]});
            var Q262;
            Q262=makeQuery(id+"F5.boolean.opBoolean","INTERSECT",EDGE,{"disambiguationData":[OD(1.0)],"derivedFrom":[makeQuery(id+"F1.opExtrude","SWEPT_FACE",FACE,{"disambiguationData":[OSD([sQuery(id+"F0.wireOp",EDGE,"E0")])]}),makeQuery(id+"F5.opExtrude","SWEPT_FACE",FACE,{"disambiguationData":[OSD([sQuery(id+"F4.wireOp",EDGE,"4144a65f-7927-494c-8b6f-a1137679e0c2")])]})]});
            var Q263;
            Q263=makeQuery(id+"F5.boolean.opBoolean","INTERSECT",EDGE,{"disambiguationData":[OD(1.0)],"derivedFrom":[makeQuery(id+"F1.opExtrude","SWEPT_FACE",FACE,{"disambiguationData":[OSD([sQuery(id+"F0.wireOp",EDGE,"E0")])]}),makeQuery(id+"F5.opExtrude","SWEPT_FACE",FACE,{"disambiguationData":[OSD([sQuery(id+"F4.wireOp",EDGE,"12fd482c-4469-40d2-a6f5-f27bb2f23065")])]})]});
            var Q264;
            Q264=makeQuery(id+"F5.boolean.opBoolean","INTERSECT",EDGE,{"disambiguationData":[OD(1.0)],"derivedFrom":[makeQuery(id+"F1.opExtrude","SWEPT_FACE",FACE,{"disambiguationData":[OSD([sQuery(id+"F0.wireOp",EDGE,"E0")])]}),makeQuery(id+"F5.opExtrude","SWEPT_FACE",FACE,{"disambiguationData":[OSD([sQuery(id+"F4.wireOp",EDGE,"068a08e4-cb17-442e-8f38-57a3403c7c46")])]})]});
            var Q265;
            Q265=makeQuery(id+"F12.boolean.opBoolean","INTERSECT",EDGE,{"derivedFrom":[makeQuery(id+"F1.opExtrude","SWEPT_FACE",FACE,{"disambiguationData":[OSD([sQuery(id+"F0.wireOp",EDGE,"E0")])]}),makeQuery(id+"F12.opExtrude","SWEPT_FACE",FACE,{"disambiguationData":[OSD([sQuery(id+"F11.wireOp",EDGE,"67c183d3-1d7e-42da-bf2e-3ae0fa41da7f")])]})]});
            var Q266;
            Q266=makeQuery(id+"F12.boolean.opBoolean","INTERSECT",EDGE,{"derivedFrom":[makeQuery(id+"F1.opExtrude","SWEPT_FACE",FACE,{"disambiguationData":[OSD([sQuery(id+"F0.wireOp",EDGE,"E0")])]}),makeQuery(id+"F12.opExtrude","SWEPT_FACE",FACE,{"disambiguationData":[OSD([sQuery(id+"F11.wireOp",EDGE,"b03eed20-ebc4-4b92-b3f9-1f2c04b3648d")])]})]});
            var Q267;
            Q267=makeQuery(id+"F12.boolean.opBoolean","INTERSECT",EDGE,{"derivedFrom":[makeQuery(id+"F1.opExtrude","SWEPT_FACE",FACE,{"disambiguationData":[OSD([sQuery(id+"F0.wireOp",EDGE,"E0")])]}),makeQuery(id+"F12.opExtrude","SWEPT_FACE",FACE,{"disambiguationData":[OSD([sQuery(id+"F11.wireOp",EDGE,"8758c10c-265c-4590-a45d-ef684658fe9d")])]})]});
            var Q268;
            Q268=makeQuery(id+"F12.boolean.opBoolean","INTERSECT",EDGE,{"derivedFrom":[makeQuery(id+"F1.opExtrude","SWEPT_FACE",FACE,{"disambiguationData":[OSD([sQuery(id+"F0.wireOp",EDGE,"E0")])]}),makeQuery(id+"F12.opExtrude","SWEPT_FACE",FACE,{"disambiguationData":[OSD([sQuery(id+"F11.wireOp",EDGE,"f5ab9e36-810e-4fb2-ab21-dc782ddc3775")])]})]});
            var Q269;
            Q269=makeQuery(id+"F12.boolean.opBoolean","INTERSECT",EDGE,{"derivedFrom":[makeQuery(id+"F1.opExtrude","SWEPT_FACE",FACE,{"disambiguationData":[OSD([sQuery(id+"F0.wireOp",EDGE,"E0")])]}),makeQuery(id+"F12.opExtrude","SWEPT_FACE",FACE,{"disambiguationData":[OSD([sQuery(id+"F11.wireOp",EDGE,"3bce39cf-3fba-4d9c-932c-c4ba27150efd")])]})]});
            var Q270;
            Q270=makeQuery(id+"F12.boolean.opBoolean","INTERSECT",EDGE,{"derivedFrom":[makeQuery(id+"F1.opExtrude","SWEPT_FACE",FACE,{"disambiguationData":[OSD([sQuery(id+"F0.wireOp",EDGE,"E0")])]}),makeQuery(id+"F12.opExtrude","SWEPT_FACE",FACE,{"disambiguationData":[OSD([sQuery(id+"F11.wireOp",EDGE,"cf1fa2b7-3847-4b1a-8fbb-cf5b8043f2ce")])]})]});
            var Q271;
            Q271=makeQuery(id+"F12.boolean.opBoolean","INTERSECT",EDGE,{"derivedFrom":[makeQuery(id+"F1.opExtrude","SWEPT_FACE",FACE,{"disambiguationData":[OSD([sQuery(id+"F0.wireOp",EDGE,"E0")])]}),makeQuery(id+"F12.opExtrude","SWEPT_FACE",FACE,{"disambiguationData":[OSD([sQuery(id+"F11.wireOp",EDGE,"8758c10c-265c-4590-a45d-ef684658fe9d")])]})]});
            var Q272;
            Q272=makeQuery(id+"F12.boolean.opBoolean","INTERSECT",EDGE,{"derivedFrom":[makeQuery(id+"F1.opExtrude","SWEPT_FACE",FACE,{"disambiguationData":[OSD([sQuery(id+"F0.wireOp",EDGE,"E0")])]}),makeQuery(id+"F12.opExtrude","SWEPT_FACE",FACE,{"disambiguationData":[OSD([sQuery(id+"F11.wireOp",EDGE,"fa630e0c-4c21-4da5-be15-fd4a47fe4884")])]})]});
            var Q273;
            Q273=makeQuery(id+"F12.boolean.opBoolean","INTERSECT",EDGE,{"derivedFrom":[makeQuery(id+"F1.opExtrude","SWEPT_FACE",FACE,{"disambiguationData":[OSD([sQuery(id+"F0.wireOp",EDGE,"E0")])]}),makeQuery(id+"F12.opExtrude","SWEPT_FACE",FACE,{"disambiguationData":[OSD([sQuery(id+"F11.wireOp",EDGE,"b6a6a7a6-ca24-45d9-8187-9d395d61f82d")])]})]});
            var Q274;
            Q274=makeQuery(id+"F12.boolean.opBoolean","INTERSECT",EDGE,{"derivedFrom":[makeQuery(id+"F1.opExtrude","SWEPT_FACE",FACE,{"disambiguationData":[OSD([sQuery(id+"F0.wireOp",EDGE,"E0")])]}),makeQuery(id+"F12.opExtrude","SWEPT_FACE",FACE,{"disambiguationData":[OSD([sQuery(id+"F11.wireOp",EDGE,"e8bf7530-191c-453a-80a5-56862e84f5e5")])]})]});
            var Q275;
            Q275=makeQuery(id+"F12.boolean.opBoolean","INTERSECT",EDGE,{"derivedFrom":[makeQuery(id+"F1.opExtrude","SWEPT_FACE",FACE,{"disambiguationData":[OSD([sQuery(id+"F0.wireOp",EDGE,"E0")])]}),makeQuery(id+"F12.opExtrude","SWEPT_FACE",FACE,{"disambiguationData":[OSD([sQuery(id+"F11.wireOp",EDGE,"b703aa34-a04e-4aae-bb17-b9baaf51e667")])]})]});
            var Q276;
            Q276=makeQuery(id+"F12.boolean.opBoolean","INTERSECT",EDGE,{"derivedFrom":[makeQuery(id+"F1.opExtrude","SWEPT_FACE",FACE,{"disambiguationData":[OSD([sQuery(id+"F0.wireOp",EDGE,"E0")])]}),makeQuery(id+"F12.opExtrude","SWEPT_FACE",FACE,{"disambiguationData":[OSD([sQuery(id+"F11.wireOp",EDGE,"dfae5c97-7dd7-4fff-be0f-4a5376e00253")])]})]});
            var Q277;
            Q277=makeQuery(id+"F12.boolean.opBoolean","INTERSECT",EDGE,{"derivedFrom":[makeQuery(id+"F1.opExtrude","SWEPT_FACE",FACE,{"disambiguationData":[OSD([sQuery(id+"F0.wireOp",EDGE,"E0")])]}),makeQuery(id+"F12.opExtrude","SWEPT_FACE",FACE,{"disambiguationData":[OSD([sQuery(id+"F11.wireOp",EDGE,"adbe43ba-a4ba-4f23-8ac4-e92d10ea3226")])]})]});
            var Q278;
            Q278=makeQuery(id+"F12.boolean.opBoolean","INTERSECT",EDGE,{"derivedFrom":[makeQuery(id+"F1.opExtrude","SWEPT_FACE",FACE,{"disambiguationData":[OSD([sQuery(id+"F0.wireOp",EDGE,"E0")])]}),makeQuery(id+"F12.opExtrude","SWEPT_FACE",FACE,{"disambiguationData":[OSD([sQuery(id+"F11.wireOp",EDGE,"9feed077-ff96-4066-aaeb-50173201c3fb")])]})]});
            var Q279;
            Q279=makeQuery(id+"F12.boolean.opBoolean","INTERSECT",EDGE,{"derivedFrom":[makeQuery(id+"F1.opExtrude","SWEPT_FACE",FACE,{"disambiguationData":[OSD([sQuery(id+"F0.wireOp",EDGE,"E0")])]}),makeQuery(id+"F12.opExtrude","SWEPT_FACE",FACE,{"disambiguationData":[OSD([sQuery(id+"F11.wireOp",EDGE,"7fb09006-04e6-4153-a925-a5b02efa07b1")])]})]});
            var Q280;
            Q280=makeQuery(id+"F12.boolean.opBoolean","INTERSECT",EDGE,{"derivedFrom":[makeQuery(id+"F1.opExtrude","SWEPT_FACE",FACE,{"disambiguationData":[OSD([sQuery(id+"F0.wireOp",EDGE,"E0")])]}),makeQuery(id+"F12.opExtrude","SWEPT_FACE",FACE,{"disambiguationData":[OSD([sQuery(id+"F11.wireOp",EDGE,"0eb8d5e7-ee9a-4d98-a7d9-7c3a4b78cebe")])]})]});
            var Q281;
            Q281=makeQuery(id+"F12.boolean.opBoolean","INTERSECT",EDGE,{"derivedFrom":[makeQuery(id+"F1.opExtrude","SWEPT_FACE",FACE,{"disambiguationData":[OSD([sQuery(id+"F0.wireOp",EDGE,"E0")])]}),makeQuery(id+"F12.opExtrude","SWEPT_FACE",FACE,{"disambiguationData":[OSD([sQuery(id+"F11.wireOp",EDGE,"7b78b5aa-67af-4fde-b4af-6a032dea360b")])]})]});
            var Q282;
            Q282=makeQuery(id+"F12.boolean.opBoolean","INTERSECT",EDGE,{"derivedFrom":[makeQuery(id+"F1.opExtrude","SWEPT_FACE",FACE,{"disambiguationData":[OSD([sQuery(id+"F0.wireOp",EDGE,"E0")])]}),makeQuery(id+"F12.opExtrude","SWEPT_FACE",FACE,{"disambiguationData":[OSD([sQuery(id+"F11.wireOp",EDGE,"7c64193d-17ad-41bb-b9d3-a3518e0933f7")])]})]});
            var Q283;
            Q283=makeQuery(id+"F12.boolean.opBoolean","INTERSECT",EDGE,{"derivedFrom":[makeQuery(id+"F1.opExtrude","SWEPT_FACE",FACE,{"disambiguationData":[OSD([sQuery(id+"F0.wireOp",EDGE,"E0")])]}),makeQuery(id+"F12.opExtrude","SWEPT_FACE",FACE,{"disambiguationData":[OSD([sQuery(id+"F11.wireOp",EDGE,"91067103-e956-4587-aab7-dd29d1236ccd")])]})]});
            var Q284;
            Q284=makeQuery(id+"F12.boolean.opBoolean","INTERSECT",EDGE,{"derivedFrom":[makeQuery(id+"F1.opExtrude","SWEPT_FACE",FACE,{"disambiguationData":[OSD([sQuery(id+"F0.wireOp",EDGE,"E0")])]}),makeQuery(id+"F12.opExtrude","SWEPT_FACE",FACE,{"disambiguationData":[OSD([sQuery(id+"F11.wireOp",EDGE,"fc0b8eb2-9f5c-4d82-8077-afb5bb214ae3")])]})]});
            var Q285;
            Q285=makeQuery(id+"F12.boolean.opBoolean","INTERSECT",EDGE,{"derivedFrom":[makeQuery(id+"F1.opExtrude","SWEPT_FACE",FACE,{"disambiguationData":[OSD([sQuery(id+"F0.wireOp",EDGE,"E0")])]}),makeQuery(id+"F12.opExtrude","SWEPT_FACE",FACE,{"disambiguationData":[OSD([sQuery(id+"F11.wireOp",EDGE,"e95ff990-42a6-4aed-a23e-eecf14f33a02")])]})]});
            var Q286;
            Q286=makeQuery(id+"F12.boolean.opBoolean","INTERSECT",EDGE,{"derivedFrom":[makeQuery(id+"F1.opExtrude","SWEPT_FACE",FACE,{"disambiguationData":[OSD([sQuery(id+"F0.wireOp",EDGE,"E0")])]}),makeQuery(id+"F12.opExtrude","SWEPT_FACE",FACE,{"disambiguationData":[OSD([sQuery(id+"F11.wireOp",EDGE,"3114f84d-6bbb-4589-be9f-9912665327ea")])]})]});
            var Q287;
            Q287=makeQuery(id+"F12.boolean.opBoolean","INTERSECT",EDGE,{"derivedFrom":[makeQuery(id+"F1.opExtrude","SWEPT_FACE",FACE,{"disambiguationData":[OSD([sQuery(id+"F0.wireOp",EDGE,"E0")])]}),makeQuery(id+"F12.opExtrude","SWEPT_FACE",FACE,{"disambiguationData":[OSD([sQuery(id+"F11.wireOp",EDGE,"f2340e13-a843-4688-b504-44fa6c1fe9ea")])]})]});
            var Q288;
            Q288=makeQuery(id+"F12.boolean.opBoolean","INTERSECT",EDGE,{"derivedFrom":[makeQuery(id+"F1.opExtrude","SWEPT_FACE",FACE,{"disambiguationData":[OSD([sQuery(id+"F0.wireOp",EDGE,"E0")])]}),makeQuery(id+"F12.opExtrude","SWEPT_FACE",FACE,{"disambiguationData":[OSD([sQuery(id+"F11.wireOp",EDGE,"d5fa8afd-5d24-4741-81ec-8e0d84c4d4eb")])]})]});
            var Q289;
            Q289=makeQuery(id+"F12.boolean.opBoolean","INTERSECT",EDGE,{"derivedFrom":[makeQuery(id+"F1.opExtrude","SWEPT_FACE",FACE,{"disambiguationData":[OSD([sQuery(id+"F0.wireOp",EDGE,"E0")])]}),makeQuery(id+"F12.opExtrude","SWEPT_FACE",FACE,{"disambiguationData":[OSD([sQuery(id+"F11.wireOp",EDGE,"327d9c5f-6637-4679-a359-34eeb01f4f77")])]})]});
            var Q290;
            Q290=makeQuery(id+"F12.boolean.opBoolean","INTERSECT",EDGE,{"derivedFrom":[makeQuery(id+"F1.opExtrude","SWEPT_FACE",FACE,{"disambiguationData":[OSD([sQuery(id+"F0.wireOp",EDGE,"E0")])]}),makeQuery(id+"F12.opExtrude","SWEPT_FACE",FACE,{"disambiguationData":[OSD([sQuery(id+"F11.wireOp",EDGE,"6b576242-fc7a-4995-9b13-030333e3f8fe")])]})]});
            var Q291;
            Q291=makeQuery(id+"F12.boolean.opBoolean","INTERSECT",EDGE,{"derivedFrom":[makeQuery(id+"F1.opExtrude","SWEPT_FACE",FACE,{"disambiguationData":[OSD([sQuery(id+"F0.wireOp",EDGE,"E0")])]}),makeQuery(id+"F12.opExtrude","SWEPT_FACE",FACE,{"disambiguationData":[OSD([sQuery(id+"F11.wireOp",EDGE,"17310e35-f0b1-47c9-b996-b18cdb21126f")])]})]});
            var Q292;
            Q292=makeQuery(id+"F12.boolean.opBoolean","INTERSECT",EDGE,{"derivedFrom":[makeQuery(id+"F1.opExtrude","SWEPT_FACE",FACE,{"disambiguationData":[OSD([sQuery(id+"F0.wireOp",EDGE,"E0")])]}),makeQuery(id+"F12.opExtrude","SWEPT_FACE",FACE,{"disambiguationData":[OSD([sQuery(id+"F11.wireOp",EDGE,"1bea7e44-a00f-4ef5-bca6-2bec41b80301")])]})]});
            var Q293;
            Q293=makeQuery(id+"F12.boolean.opBoolean","INTERSECT",EDGE,{"derivedFrom":[makeQuery(id+"F1.opExtrude","SWEPT_FACE",FACE,{"disambiguationData":[OSD([sQuery(id+"F0.wireOp",EDGE,"E0")])]}),makeQuery(id+"F12.opExtrude","SWEPT_FACE",FACE,{"disambiguationData":[OSD([sQuery(id+"F11.wireOp",EDGE,"200c0ae8-db39-47c0-8c74-e07b8066f8af")])]})]});
            var Q294;
            Q294=makeQuery(id+"F12.boolean.opBoolean","INTERSECT",EDGE,{"derivedFrom":[makeQuery(id+"F1.opExtrude","SWEPT_FACE",FACE,{"disambiguationData":[OSD([sQuery(id+"F0.wireOp",EDGE,"E0")])]}),makeQuery(id+"F12.opExtrude","SWEPT_FACE",FACE,{"disambiguationData":[OSD([sQuery(id+"F11.wireOp",EDGE,"e97e0156-3522-47dd-9f51-3a33e541eac2")])]})]});
            var Q295;
            Q295=makeQuery(id+"F12.boolean.opBoolean","INTERSECT",EDGE,{"derivedFrom":[makeQuery(id+"F1.opExtrude","SWEPT_FACE",FACE,{"disambiguationData":[OSD([sQuery(id+"F0.wireOp",EDGE,"E0")])]}),makeQuery(id+"F12.opExtrude","SWEPT_FACE",FACE,{"disambiguationData":[OSD([sQuery(id+"F11.wireOp",EDGE,"adce909b-9e2c-4011-806a-5ba738e49197")])]})]});
            var Q296;
            Q296=makeQuery(id+"F12.boolean.opBoolean","INTERSECT",EDGE,{"derivedFrom":[makeQuery(id+"F1.opExtrude","SWEPT_FACE",FACE,{"disambiguationData":[OSD([sQuery(id+"F0.wireOp",EDGE,"E0")])]}),makeQuery(id+"F12.opExtrude","SWEPT_FACE",FACE,{"disambiguationData":[OSD([sQuery(id+"F11.wireOp",EDGE,"cd0ca915-f2ce-4b21-a4ef-a866892009df")])]})]});
            var Q297;
            Q297=makeQuery(id+"F12.boolean.opBoolean","INTERSECT",EDGE,{"derivedFrom":[makeQuery(id+"F1.opExtrude","SWEPT_FACE",FACE,{"disambiguationData":[OSD([sQuery(id+"F0.wireOp",EDGE,"E0")])]}),makeQuery(id+"F12.opExtrude","SWEPT_FACE",FACE,{"disambiguationData":[OSD([sQuery(id+"F11.wireOp",EDGE,"566c1776-e442-4c1a-8a27-e67b73d4de07")])]})]});
            var Q298;
            Q298=makeQuery(id+"F12.boolean.opBoolean","INTERSECT",EDGE,{"derivedFrom":[makeQuery(id+"F1.opExtrude","SWEPT_FACE",FACE,{"disambiguationData":[OSD([sQuery(id+"F0.wireOp",EDGE,"E0")])]}),makeQuery(id+"F12.opExtrude","SWEPT_FACE",FACE,{"disambiguationData":[OSD([sQuery(id+"F11.wireOp",EDGE,"b2e68df8-0d34-48a2-85ed-ba0c7cba7b83")])]})]});
            var Q299;
            Q299=makeQuery(id+"F12.boolean.opBoolean","INTERSECT",EDGE,{"derivedFrom":[makeQuery(id+"F1.opExtrude","SWEPT_FACE",FACE,{"disambiguationData":[OSD([sQuery(id+"F0.wireOp",EDGE,"E0")])]}),makeQuery(id+"F12.opExtrude","SWEPT_FACE",FACE,{"disambiguationData":[OSD([sQuery(id+"F11.wireOp",EDGE,"a95edd79-1df3-4cd4-b19e-80dde6a9dddc")])]})]});
            var Q300;
            Q300=makeQuery(id+"F12.boolean.opBoolean","INTERSECT",EDGE,{"derivedFrom":[makeQuery(id+"F1.opExtrude","SWEPT_FACE",FACE,{"disambiguationData":[OSD([sQuery(id+"F0.wireOp",EDGE,"E0")])]}),makeQuery(id+"F12.opExtrude","SWEPT_FACE",FACE,{"disambiguationData":[OSD([sQuery(id+"F11.wireOp",EDGE,"7bac7bb8-7502-49c0-8bc5-64d494245f90")])]})]});
            var Q301;
            Q301=makeQuery(id+"F12.boolean.opBoolean","INTERSECT",EDGE,{"derivedFrom":[makeQuery(id+"F1.opExtrude","SWEPT_FACE",FACE,{"disambiguationData":[OSD([sQuery(id+"F0.wireOp",EDGE,"E0")])]}),makeQuery(id+"F12.opExtrude","SWEPT_FACE",FACE,{"disambiguationData":[OSD([sQuery(id+"F11.wireOp",EDGE,"0a6e00ce-b892-4f90-b503-7d4f459e09b7")])]})]});
            var Q302;
            Q302=makeQuery(id+"F12.boolean.opBoolean","INTERSECT",EDGE,{"derivedFrom":[makeQuery(id+"F1.opExtrude","SWEPT_FACE",FACE,{"disambiguationData":[OSD([sQuery(id+"F0.wireOp",EDGE,"E0")])]}),makeQuery(id+"F12.opExtrude","SWEPT_FACE",FACE,{"disambiguationData":[OSD([sQuery(id+"F11.wireOp",EDGE,"1c4190f5-12c8-4d12-a8ea-2983d30e1d65")])]})]});
            var Q303;
            Q303=makeQuery(id+"F12.boolean.opBoolean","INTERSECT",EDGE,{"derivedFrom":[makeQuery(id+"F1.opExtrude","SWEPT_FACE",FACE,{"disambiguationData":[OSD([sQuery(id+"F0.wireOp",EDGE,"E0")])]}),makeQuery(id+"F12.opExtrude","SWEPT_FACE",FACE,{"disambiguationData":[OSD([sQuery(id+"F11.wireOp",EDGE,"8c0447c6-60ba-4edd-8488-664759495711")])]})]});
            var Q304;
            Q304=makeQuery(id+"F12.boolean.opBoolean","INTERSECT",EDGE,{"derivedFrom":[makeQuery(id+"F1.opExtrude","SWEPT_FACE",FACE,{"disambiguationData":[OSD([sQuery(id+"F0.wireOp",EDGE,"E0")])]}),makeQuery(id+"F12.opExtrude","SWEPT_FACE",FACE,{"disambiguationData":[OSD([sQuery(id+"F11.wireOp",EDGE,"5dfe9654-666d-4f3e-bb59-82f642316b6d")])]})]});
            var Q305;
            Q305=makeQuery(id+"F12.boolean.opBoolean","INTERSECT",EDGE,{"derivedFrom":[makeQuery(id+"F1.opExtrude","SWEPT_FACE",FACE,{"disambiguationData":[OSD([sQuery(id+"F0.wireOp",EDGE,"E0")])]}),makeQuery(id+"F12.opExtrude","SWEPT_FACE",FACE,{"disambiguationData":[OSD([sQuery(id+"F11.wireOp",EDGE,"841d8487-d472-43f1-bdbd-e7ff6b45cd41")])]})]});
            var Q306;
            Q306=makeQuery(id+"F12.boolean.opBoolean","INTERSECT",EDGE,{"derivedFrom":[makeQuery(id+"F1.opExtrude","SWEPT_FACE",FACE,{"disambiguationData":[OSD([sQuery(id+"F0.wireOp",EDGE,"E0")])]}),makeQuery(id+"F12.opExtrude","SWEPT_FACE",FACE,{"disambiguationData":[OSD([sQuery(id+"F11.wireOp",EDGE,"6e0252a6-974a-4586-a4a8-83f366333a88")])]})]});
            var Q307;
            Q307=makeQuery(id+"F12.boolean.opBoolean","INTERSECT",EDGE,{"derivedFrom":[makeQuery(id+"F1.opExtrude","SWEPT_FACE",FACE,{"disambiguationData":[OSD([sQuery(id+"F0.wireOp",EDGE,"E0")])]}),makeQuery(id+"F12.opExtrude","SWEPT_FACE",FACE,{"disambiguationData":[OSD([sQuery(id+"F11.wireOp",EDGE,"30b1511e-e2ca-4772-9673-cf06763b7aad")])]})]});
            var Q308;
            Q308=makeQuery(id+"F12.boolean.opBoolean","INTERSECT",EDGE,{"derivedFrom":[makeQuery(id+"F1.opExtrude","SWEPT_FACE",FACE,{"disambiguationData":[OSD([sQuery(id+"F0.wireOp",EDGE,"E0")])]}),makeQuery(id+"F12.opExtrude","SWEPT_FACE",FACE,{"disambiguationData":[OSD([sQuery(id+"F11.wireOp",EDGE,"6ca8cd86-5e60-4f71-aece-58a5cefb0301")])]})]});
            var Q309;
            Q309=makeQuery(id+"F12.boolean.opBoolean","INTERSECT",EDGE,{"derivedFrom":[makeQuery(id+"F1.opExtrude","SWEPT_FACE",FACE,{"disambiguationData":[OSD([sQuery(id+"F0.wireOp",EDGE,"E0")])]}),makeQuery(id+"F12.opExtrude","SWEPT_FACE",FACE,{"disambiguationData":[OSD([sQuery(id+"F11.wireOp",EDGE,"66b1be52-5d7b-488e-ab88-be7fc1489788")])]})]});
            var Q310;
            Q310=makeQuery(id+"F12.boolean.opBoolean","INTERSECT",EDGE,{"derivedFrom":[makeQuery(id+"F1.opExtrude","SWEPT_FACE",FACE,{"disambiguationData":[OSD([sQuery(id+"F0.wireOp",EDGE,"E0")])]}),makeQuery(id+"F12.opExtrude","SWEPT_FACE",FACE,{"disambiguationData":[OSD([sQuery(id+"F11.wireOp",EDGE,"a826e480-ba9d-454b-a154-b724fcca502a")])]})]});
            var Q311;
            Q311=makeQuery(id+"F12.boolean.opBoolean","INTERSECT",EDGE,{"derivedFrom":[makeQuery(id+"F1.opExtrude","SWEPT_FACE",FACE,{"disambiguationData":[OSD([sQuery(id+"F0.wireOp",EDGE,"E0")])]}),makeQuery(id+"F12.opExtrude","SWEPT_FACE",FACE,{"disambiguationData":[OSD([sQuery(id+"F11.wireOp",EDGE,"07a74ef0-9ede-4776-8ebf-e754756c114a")])]})]});
            var Q312;
            Q312=makeQuery(id+"F12.boolean.opBoolean","INTERSECT",EDGE,{"derivedFrom":[makeQuery(id+"F1.opExtrude","SWEPT_FACE",FACE,{"disambiguationData":[OSD([sQuery(id+"F0.wireOp",EDGE,"E0")])]}),makeQuery(id+"F12.opExtrude","SWEPT_FACE",FACE,{"disambiguationData":[OSD([sQuery(id+"F11.wireOp",EDGE,"092ed403-3d4f-4c15-960d-c10ef8789eb5")])]})]});
            var Q313;
            Q313=makeQuery(id+"F12.boolean.opBoolean","INTERSECT",EDGE,{"derivedFrom":[makeQuery(id+"F1.opExtrude","SWEPT_FACE",FACE,{"disambiguationData":[OSD([sQuery(id+"F0.wireOp",EDGE,"E0")])]}),makeQuery(id+"F12.opExtrude","SWEPT_FACE",FACE,{"disambiguationData":[OSD([sQuery(id+"F11.wireOp",EDGE,"acb8dcbc-daed-461c-af8b-853c71a07eac")])]})]});
            var Q314;
            Q314=makeQuery(id+"F12.boolean.opBoolean","INTERSECT",EDGE,{"derivedFrom":[makeQuery(id+"F1.opExtrude","SWEPT_FACE",FACE,{"disambiguationData":[OSD([sQuery(id+"F0.wireOp",EDGE,"E0")])]}),makeQuery(id+"F12.opExtrude","SWEPT_FACE",FACE,{"disambiguationData":[OSD([sQuery(id+"F11.wireOp",EDGE,"76158571-8428-4aec-bd47-33adf174f2a4")])]})]});
            var Q315;
            Q315=makeQuery(id+"F12.boolean.opBoolean","INTERSECT",EDGE,{"derivedFrom":[makeQuery(id+"F1.opExtrude","SWEPT_FACE",FACE,{"disambiguationData":[OSD([sQuery(id+"F0.wireOp",EDGE,"E0")])]}),makeQuery(id+"F12.opExtrude","SWEPT_FACE",FACE,{"disambiguationData":[OSD([sQuery(id+"F11.wireOp",EDGE,"2e92792f-4c7e-4468-9ae2-ab93ba844d4b")])]})]});
            var Q316;
            Q316=makeQuery(id+"F12.boolean.opBoolean","INTERSECT",EDGE,{"derivedFrom":[makeQuery(id+"F1.opExtrude","SWEPT_FACE",FACE,{"disambiguationData":[OSD([sQuery(id+"F0.wireOp",EDGE,"E0")])]}),makeQuery(id+"F12.opExtrude","SWEPT_FACE",FACE,{"disambiguationData":[OSD([sQuery(id+"F11.wireOp",EDGE,"b0197f1f-3212-4fe7-853f-974a1a9ee185")])]})]});
            var Q317;
            Q317=makeQuery(id+"F12.boolean.opBoolean","INTERSECT",EDGE,{"derivedFrom":[makeQuery(id+"F1.opExtrude","SWEPT_FACE",FACE,{"disambiguationData":[OSD([sQuery(id+"F0.wireOp",EDGE,"E0")])]}),makeQuery(id+"F12.opExtrude","SWEPT_FACE",FACE,{"disambiguationData":[OSD([sQuery(id+"F11.wireOp",EDGE,"faa93db1-9b94-4bc8-a4df-a69461af7118")])]})]});
            var Q318;
            Q318=makeQuery(id+"F12.boolean.opBoolean","INTERSECT",EDGE,{"derivedFrom":[makeQuery(id+"F1.opExtrude","SWEPT_FACE",FACE,{"disambiguationData":[OSD([sQuery(id+"F0.wireOp",EDGE,"E0")])]}),makeQuery(id+"F12.opExtrude","SWEPT_FACE",FACE,{"disambiguationData":[OSD([sQuery(id+"F11.wireOp",EDGE,"bf553eab-f362-4974-a638-a7733928a928")])]})]});
            var Q319;
            Q319=makeQuery(id+"F12.boolean.opBoolean","INTERSECT",EDGE,{"derivedFrom":[makeQuery(id+"F1.opExtrude","SWEPT_FACE",FACE,{"disambiguationData":[OSD([sQuery(id+"F0.wireOp",EDGE,"E0")])]}),makeQuery(id+"F12.opExtrude","SWEPT_FACE",FACE,{"disambiguationData":[OSD([sQuery(id+"F11.wireOp",EDGE,"80697549-b82d-4dee-9442-59f5951ca8b8")])]})]});
            var Q320;
            Q320=makeQuery(id+"F12.boolean.opBoolean","INTERSECT",EDGE,{"derivedFrom":[makeQuery(id+"F1.opExtrude","SWEPT_FACE",FACE,{"disambiguationData":[OSD([sQuery(id+"F0.wireOp",EDGE,"E0")])]}),makeQuery(id+"F12.opExtrude","SWEPT_FACE",FACE,{"disambiguationData":[OSD([sQuery(id+"F11.wireOp",EDGE,"0e8c3faf-8d29-4084-8698-73abd46cf39c")])]})]});
            var Q321;
            Q321=makeQuery(id+"F12.boolean.opBoolean","INTERSECT",EDGE,{"derivedFrom":[makeQuery(id+"F1.opExtrude","SWEPT_FACE",FACE,{"disambiguationData":[OSD([sQuery(id+"F0.wireOp",EDGE,"E0")])]}),makeQuery(id+"F12.opExtrude","SWEPT_FACE",FACE,{"disambiguationData":[OSD([sQuery(id+"F11.wireOp",EDGE,"2d858d98-3365-4601-99b5-01ed8230ce64")])]})]});
            var Q322;
            Q322=makeQuery(id+"F12.boolean.opBoolean","INTERSECT",EDGE,{"derivedFrom":[makeQuery(id+"F1.opExtrude","SWEPT_FACE",FACE,{"disambiguationData":[OSD([sQuery(id+"F0.wireOp",EDGE,"E0")])]}),makeQuery(id+"F12.opExtrude","SWEPT_FACE",FACE,{"disambiguationData":[OSD([sQuery(id+"F11.wireOp",EDGE,"6bbfbd9f-83cf-4e5a-8c48-5f02fa0a9c69")])]})]});
            var Q323;
            Q323=makeQuery(id+"F12.boolean.opBoolean","INTERSECT",EDGE,{"derivedFrom":[makeQuery(id+"F1.opExtrude","SWEPT_FACE",FACE,{"disambiguationData":[OSD([sQuery(id+"F0.wireOp",EDGE,"E0")])]}),makeQuery(id+"F12.opExtrude","SWEPT_FACE",FACE,{"disambiguationData":[OSD([sQuery(id+"F11.wireOp",EDGE,"8a950ba1-a090-4c8d-82b9-cd5225b2b9e3")])]})]});
            var Q324;
            Q324=makeQuery(id+"F12.boolean.opBoolean","INTERSECT",EDGE,{"derivedFrom":[makeQuery(id+"F1.opExtrude","SWEPT_FACE",FACE,{"disambiguationData":[OSD([sQuery(id+"F0.wireOp",EDGE,"E0")])]}),makeQuery(id+"F12.opExtrude","SWEPT_FACE",FACE,{"disambiguationData":[OSD([sQuery(id+"F11.wireOp",EDGE,"de11c3ef-7a1d-4805-b947-306e5608d462")])]})]});
            var Q325;
            Q325=makeQuery(id+"F12.boolean.opBoolean","INTERSECT",EDGE,{"derivedFrom":[makeQuery(id+"F1.opExtrude","SWEPT_FACE",FACE,{"disambiguationData":[OSD([sQuery(id+"F0.wireOp",EDGE,"E0")])]}),makeQuery(id+"F12.opExtrude","SWEPT_FACE",FACE,{"disambiguationData":[OSD([sQuery(id+"F11.wireOp",EDGE,"5fc31a4b-0bb3-428e-9063-e62cabce7d17")])]})]});
            var Q326;
            Q326=makeQuery(id+"F12.boolean.opBoolean","INTERSECT",EDGE,{"derivedFrom":[makeQuery(id+"F1.opExtrude","SWEPT_FACE",FACE,{"disambiguationData":[OSD([sQuery(id+"F0.wireOp",EDGE,"E0")])]}),makeQuery(id+"F12.opExtrude","SWEPT_FACE",FACE,{"disambiguationData":[OSD([sQuery(id+"F11.wireOp",EDGE,"2fde0330-21a3-47f8-95e4-c6b2125bc28d")])]})]});
            var Q327;
            Q327=makeQuery(id+"F12.boolean.opBoolean","INTERSECT",EDGE,{"derivedFrom":[makeQuery(id+"F1.opExtrude","SWEPT_FACE",FACE,{"disambiguationData":[OSD([sQuery(id+"F0.wireOp",EDGE,"E0")])]}),makeQuery(id+"F12.opExtrude","SWEPT_FACE",FACE,{"disambiguationData":[OSD([sQuery(id+"F11.wireOp",EDGE,"39ea25aa-dc9d-413d-aca9-5b751d16431b")])]})]});
            var Q328;
            Q328=makeQuery(id+"F12.boolean.opBoolean","INTERSECT",EDGE,{"derivedFrom":[makeQuery(id+"F1.opExtrude","SWEPT_FACE",FACE,{"disambiguationData":[OSD([sQuery(id+"F0.wireOp",EDGE,"E0")])]}),makeQuery(id+"F12.opExtrude","SWEPT_FACE",FACE,{"disambiguationData":[OSD([sQuery(id+"F11.wireOp",EDGE,"45a08d57-ac6c-4e91-8221-61a5d03ef4d8")])]})]});
            var Q329;
            Q329=makeQuery(id+"F12.boolean.opBoolean","INTERSECT",EDGE,{"derivedFrom":[makeQuery(id+"F1.opExtrude","SWEPT_FACE",FACE,{"disambiguationData":[OSD([sQuery(id+"F0.wireOp",EDGE,"E0")])]}),makeQuery(id+"F12.opExtrude","SWEPT_FACE",FACE,{"disambiguationData":[OSD([sQuery(id+"F11.wireOp",EDGE,"ae00799b-1def-4a87-a375-c2745601d105")])]})]});
            var Q330;
            Q330=makeQuery(id+"F12.boolean.opBoolean","INTERSECT",EDGE,{"derivedFrom":[makeQuery(id+"F1.opExtrude","SWEPT_FACE",FACE,{"disambiguationData":[OSD([sQuery(id+"F0.wireOp",EDGE,"E0")])]}),makeQuery(id+"F12.opExtrude","SWEPT_FACE",FACE,{"disambiguationData":[OSD([sQuery(id+"F11.wireOp",EDGE,"04f7a225-5764-4d5d-9f0d-af1fe46beb71")])]})]});
            var Q331;
            Q331=makeQuery(id+"F12.boolean.opBoolean","INTERSECT",EDGE,{"derivedFrom":[makeQuery(id+"F1.opExtrude","SWEPT_FACE",FACE,{"disambiguationData":[OSD([sQuery(id+"F0.wireOp",EDGE,"E0")])]}),makeQuery(id+"F12.opExtrude","SWEPT_FACE",FACE,{"disambiguationData":[OSD([sQuery(id+"F11.wireOp",EDGE,"874c3c57-a6bb-4400-9591-b6c49b54f0d5")])]})]});
            var Q332;
            Q332=makeQuery(id+"F12.boolean.opBoolean","INTERSECT",EDGE,{"derivedFrom":[makeQuery(id+"F1.opExtrude","SWEPT_FACE",FACE,{"disambiguationData":[OSD([sQuery(id+"F0.wireOp",EDGE,"E0")])]}),makeQuery(id+"F12.opExtrude","SWEPT_FACE",FACE,{"disambiguationData":[OSD([sQuery(id+"F11.wireOp",EDGE,"46c9ed28-b344-407f-a562-7c22284d55fe")])]})]});
            var Q333;
            Q333=makeQuery(id+"F12.boolean.opBoolean","INTERSECT",EDGE,{"derivedFrom":[makeQuery(id+"F1.opExtrude","SWEPT_FACE",FACE,{"disambiguationData":[OSD([sQuery(id+"F0.wireOp",EDGE,"E0")])]}),makeQuery(id+"F12.opExtrude","SWEPT_FACE",FACE,{"disambiguationData":[OSD([sQuery(id+"F11.wireOp",EDGE,"62da7513-9491-427f-938b-696b47152ffd")])]})]});
            var Q334;
            Q334=makeQuery(id+"F12.boolean.opBoolean","INTERSECT",EDGE,{"derivedFrom":[makeQuery(id+"F1.opExtrude","SWEPT_FACE",FACE,{"disambiguationData":[OSD([sQuery(id+"F0.wireOp",EDGE,"E0")])]}),makeQuery(id+"F12.opExtrude","SWEPT_FACE",FACE,{"disambiguationData":[OSD([sQuery(id+"F11.wireOp",EDGE,"aa06bcb9-a86b-4f86-a9b4-85c86a1af446")])]})]});
            var Q335;
            Q335=makeQuery(id+"F12.boolean.opBoolean","INTERSECT",EDGE,{"derivedFrom":[makeQuery(id+"F1.opExtrude","SWEPT_FACE",FACE,{"disambiguationData":[OSD([sQuery(id+"F0.wireOp",EDGE,"E0")])]}),makeQuery(id+"F12.opExtrude","SWEPT_FACE",FACE,{"disambiguationData":[OSD([sQuery(id+"F11.wireOp",EDGE,"39fdaf24-626d-4be9-ae9c-25e924fe0a02")])]})]});
            var Q336;
            Q336=makeQuery(id+"F12.boolean.opBoolean","INTERSECT",EDGE,{"derivedFrom":[makeQuery(id+"F1.opExtrude","SWEPT_FACE",FACE,{"disambiguationData":[OSD([sQuery(id+"F0.wireOp",EDGE,"E0")])]}),makeQuery(id+"F12.opExtrude","SWEPT_FACE",FACE,{"disambiguationData":[OSD([sQuery(id+"F11.wireOp",EDGE,"25193117-9b4b-42b4-a85a-958f9bb3fb66")])]})]});
            var Q337;
            Q337=makeQuery(id+"F12.boolean.opBoolean","INTERSECT",EDGE,{"derivedFrom":[makeQuery(id+"F1.opExtrude","SWEPT_FACE",FACE,{"disambiguationData":[OSD([sQuery(id+"F0.wireOp",EDGE,"E0")])]}),makeQuery(id+"F12.opExtrude","SWEPT_FACE",FACE,{"disambiguationData":[OSD([sQuery(id+"F11.wireOp",EDGE,"2c336ab2-bfc0-43d3-a329-a216c8d1b87b")])]})]});
            var Q338;
            Q338=makeQuery(id+"F12.boolean.opBoolean","INTERSECT",EDGE,{"derivedFrom":[makeQuery(id+"F1.opExtrude","SWEPT_FACE",FACE,{"disambiguationData":[OSD([sQuery(id+"F0.wireOp",EDGE,"E0")])]}),makeQuery(id+"F12.opExtrude","SWEPT_FACE",FACE,{"disambiguationData":[OSD([sQuery(id+"F11.wireOp",EDGE,"64d6da3b-8a0c-46ea-a12b-d14f425ae2f6")])]})]});
            var Q339;
            Q339=makeQuery(id+"F12.boolean.opBoolean","INTERSECT",EDGE,{"derivedFrom":[makeQuery(id+"F1.opExtrude","SWEPT_FACE",FACE,{"disambiguationData":[OSD([sQuery(id+"F0.wireOp",EDGE,"E0")])]}),makeQuery(id+"F12.opExtrude","SWEPT_FACE",FACE,{"disambiguationData":[OSD([sQuery(id+"F11.wireOp",EDGE,"d1064973-f400-4dc1-ab4f-e9b9d72f416c")])]})]});
            var Q340;
            Q340=makeQuery(id+"F12.boolean.opBoolean","INTERSECT",EDGE,{"derivedFrom":[makeQuery(id+"F1.opExtrude","SWEPT_FACE",FACE,{"disambiguationData":[OSD([sQuery(id+"F0.wireOp",EDGE,"E0")])]}),makeQuery(id+"F12.opExtrude","SWEPT_FACE",FACE,{"disambiguationData":[OSD([sQuery(id+"F11.wireOp",EDGE,"368e7495-1394-477b-bb01-d5cedc0a1b70")])]})]});
            var Q341;
            Q341=makeQuery(id+"F12.boolean.opBoolean","INTERSECT",EDGE,{"derivedFrom":[makeQuery(id+"F1.opExtrude","SWEPT_FACE",FACE,{"disambiguationData":[OSD([sQuery(id+"F0.wireOp",EDGE,"E0")])]}),makeQuery(id+"F12.opExtrude","SWEPT_FACE",FACE,{"disambiguationData":[OSD([sQuery(id+"F11.wireOp",EDGE,"50bbaaba-c4f5-4406-8380-98ff907eccc0")])]})]});
            var Q342;
            Q342=makeQuery(id+"F12.boolean.opBoolean","INTERSECT",EDGE,{"derivedFrom":[makeQuery(id+"F1.opExtrude","SWEPT_FACE",FACE,{"disambiguationData":[OSD([sQuery(id+"F0.wireOp",EDGE,"E0")])]}),makeQuery(id+"F12.opExtrude","SWEPT_FACE",FACE,{"disambiguationData":[OSD([sQuery(id+"F11.wireOp",EDGE,"252ab781-f89f-493a-a601-3851de4bca54")])]})]});
            var Q343;
            Q343=makeQuery(id+"F12.boolean.opBoolean","INTERSECT",EDGE,{"derivedFrom":[makeQuery(id+"F1.opExtrude","SWEPT_FACE",FACE,{"disambiguationData":[OSD([sQuery(id+"F0.wireOp",EDGE,"E0")])]}),makeQuery(id+"F12.opExtrude","SWEPT_FACE",FACE,{"disambiguationData":[OSD([sQuery(id+"F11.wireOp",EDGE,"077e507b-792a-4822-bd42-40c28a37b443")])]})]});
            var Q344;
            Q344=makeQuery(id+"F12.boolean.opBoolean","INTERSECT",EDGE,{"derivedFrom":[makeQuery(id+"F1.opExtrude","SWEPT_FACE",FACE,{"disambiguationData":[OSD([sQuery(id+"F0.wireOp",EDGE,"E0")])]}),makeQuery(id+"F12.opExtrude","SWEPT_FACE",FACE,{"disambiguationData":[OSD([sQuery(id+"F11.wireOp",EDGE,"041bb2eb-ae03-41b4-8679-2ee14c3b35eb")])]})]});
            var Q345;
            Q345=makeQuery(id+"F12.boolean.opBoolean","INTERSECT",EDGE,{"derivedFrom":[makeQuery(id+"F1.opExtrude","SWEPT_FACE",FACE,{"disambiguationData":[OSD([sQuery(id+"F0.wireOp",EDGE,"E0")])]}),makeQuery(id+"F12.opExtrude","SWEPT_FACE",FACE,{"disambiguationData":[OSD([sQuery(id+"F11.wireOp",EDGE,"e56254bb-4933-495c-a375-924da8ba2d97"),sQuery(id+"F11.wireOp",EDGE,"2da46073-95db-4ae7-83f6-e80e428f4fd1")])]})]});
            var Q346;
            Q346=makeQuery(id+"F12.boolean.opBoolean","INTERSECT",EDGE,{"derivedFrom":[makeQuery(id+"F1.opExtrude","SWEPT_FACE",FACE,{"disambiguationData":[OSD([sQuery(id+"F0.wireOp",EDGE,"E0")])]}),makeQuery(id+"F12.opExtrude","SWEPT_FACE",FACE,{"disambiguationData":[OSD([sQuery(id+"F11.wireOp",EDGE,"09fa856f-861a-4983-bd95-702295a2dd2e")])]})]});
            var Q347;
            Q347=makeQuery(id+"F10.boolean.opBoolean","INTERSECT",EDGE,{"disambiguationData":[OD(1.0)],"derivedFrom":[makeQuery(id+"F1.opExtrude","SWEPT_FACE",FACE,{"disambiguationData":[OSD([sQuery(id+"F0.wireOp",EDGE,"E0")])]}),makeQuery(id+"F10.opExtrude","SWEPT_FACE",FACE,{"disambiguationData":[OSD([sQuery(id+"F9.wireOp",EDGE,"2e52e4ba-a856-43cc-8b69-bc95ae584be1")])]})]});
            var Q348;
            Q348=makeQuery(id+"F10.boolean.opBoolean","INTERSECT",EDGE,{"disambiguationData":[OD(1.0)],"derivedFrom":[makeQuery(id+"F1.opExtrude","SWEPT_FACE",FACE,{"disambiguationData":[OSD([sQuery(id+"F0.wireOp",EDGE,"E0")])]}),makeQuery(id+"F10.opExtrude","SWEPT_FACE",FACE,{"disambiguationData":[OSD([sQuery(id+"F9.wireOp",EDGE,"d68f23c5-fa44-4f68-a5e1-914856eae846")])]})]});
            var Q349;
            Q349=makeQuery(id+"F10.boolean.opBoolean","INTERSECT",EDGE,{"disambiguationData":[OD(1.0)],"derivedFrom":[makeQuery(id+"F1.opExtrude","SWEPT_FACE",FACE,{"disambiguationData":[OSD([sQuery(id+"F0.wireOp",EDGE,"E0")])]}),makeQuery(id+"F10.opExtrude","SWEPT_FACE",FACE,{"disambiguationData":[OSD([sQuery(id+"F9.wireOp",EDGE,"3921cf77-2c7d-4081-b0dc-8dd1674662ff")])]})]});
            var Q350;
            Q350=makeQuery(id+"F7.boolean.opBoolean","INTERSECT",EDGE,{"disambiguationData":[OD(0.0)],"derivedFrom":[makeQuery(id+"F1.opExtrude","SWEPT_FACE",FACE,{"disambiguationData":[OSD([sQuery(id+"F0.wireOp",EDGE,"E0")])]}),makeQuery(id+"F7.opExtrude","SWEPT_FACE",FACE,{"disambiguationData":[OSD([sQuery(id+"F6.wireOp",EDGE,"E8.0")])]})]});
            var Q351;
            Q351=makeQuery(id+"F7.boolean.opBoolean","INTERSECT",EDGE,{"disambiguationData":[OD(0.0)],"derivedFrom":[makeQuery(id+"F1.opExtrude","SWEPT_FACE",FACE,{"disambiguationData":[OSD([sQuery(id+"F0.wireOp",EDGE,"E0")])]}),makeQuery(id+"F7.opExtrude","SWEPT_FACE",FACE,{"disambiguationData":[OSD([sQuery(id+"F6.wireOp",EDGE,"E8.5")])]})]});
            fillet(context, id + "F14", {"entities" : qUnion([Q0, Q1, Q2, Q3, Q4, Q5, Q6, Q7, Q8, Q9, Q10, Q11, Q12, Q13, Q14, Q15, Q16, Q17, Q18, Q19, Q20, Q21, Q22, Q23, Q24, Q25, Q26, Q27, Q28, Q29, Q30, Q31, Q32, Q33, Q34, Q35, Q36, Q37, Q38, Q39, Q40, Q41, Q42, Q43, Q44, Q45, Q46, Q47, Q48, Q49, Q50, Q51, Q52, Q53, Q54, Q55, Q56, Q57, Q58, Q59, Q60, Q61, Q62, Q63, Q64, Q65, Q66, Q67, Q68, Q69, Q70, Q71, Q72, Q73, Q74, Q75, Q76, Q77, Q78, Q79, Q80, Q81, Q82, Q83, Q84, Q85, Q86, Q87, Q88, Q89, Q90, Q91, Q92, Q93, Q94, Q95, Q96, Q97, Q98, Q99, Q100, Q101, Q102, Q103, Q104, Q105, Q106, Q107, Q108, Q109, Q110, Q111, Q112, Q113, Q114, Q115, Q116, Q117, Q118, Q119, Q120, Q121, Q122, Q123, Q124, Q125, Q126, Q127, Q128, Q129, Q130, Q131, Q132, Q133, Q134, Q135, Q136, Q137, Q138, Q139, Q140, Q141, Q142, Q143, Q144, Q145, Q146, Q147, Q148, Q149, Q150, Q151, Q152, Q153, Q154, Q155, Q156, Q157, Q158, Q159, Q160, Q161, Q162, Q163, Q164, Q165, Q166, Q167, Q168, Q169, Q170, Q171, Q172, Q173, Q174, Q175, Q176, Q177, Q178, Q179, Q180, Q181, Q182, Q183, Q184, Q185, Q186, Q187, Q188, Q189, Q190, Q191, Q192, Q193, Q194, Q195, Q196, Q197, Q198, Q199, Q200, Q201, Q202, Q203, Q204, Q205, Q206, Q207, Q208, Q209, Q210, Q211, Q212, Q213, Q214, Q215, Q216, Q217, Q218, Q219, Q220, Q221, Q222, Q223, Q224, Q225, Q226, Q227, Q228, Q229, Q230, Q231, Q232, Q233, Q234, Q235, Q236, Q237, Q238, Q239, Q240, Q241, Q242, Q243, Q244, Q245, Q246, Q247, Q248, Q249, Q250, Q251, Q252, Q253, Q254, Q255, Q256, Q257, Q258, Q259, Q260, Q261, Q262, Q263, Q264, Q265, Q266, Q267, Q268, Q269, Q270, Q271, Q272, Q273, Q274, Q275, Q276, Q277, Q278, Q279, Q280, Q281, Q282, Q283, Q284, Q285, Q286, Q287, Q288, Q289, Q290, Q291, Q292, Q293, Q294, Q295, Q296, Q297, Q298, Q299, Q300, Q301, Q302, Q303, Q304, Q305, Q306, Q307, Q308, Q309, Q310, Q311, Q312, Q313, Q314, Q315, Q316, Q317, Q318, Q319, Q320, Q321, Q322, Q323, Q324, Q325, Q326, Q327, Q328, Q329, Q330, Q331, Q332, Q333, Q334, Q335, Q336, Q337, Q338, Q339, Q340, Q341, Q342, Q343, Q344, Q345, Q346, Q347, Q348, Q349, Q350, Q351]), "radius" : 0.7 * mm, "tangentPropagation" : true, "defaultsChanged" : true, "vertexSettings" : [], "allowEdgeOverflow" : false});
        }
        {
            var Q0;
            Q0=makeQuery(id+"F10.boolean.opBoolean","INTERSECT",EDGE,{"disambiguationData":[OD(0.0)],"derivedFrom":[makeQuery(id+"F1.opExtrude","SWEPT_FACE",FACE,{"disambiguationData":[OSD([sQuery(id+"F0.wireOp",EDGE,"E0")])]}),makeQuery(id+"F10.opExtrude","SWEPT_FACE",FACE,{"disambiguationData":[OSD([sQuery(id+"F9.wireOp",EDGE,"SvTCUe0E-rdOP-nI53-K5Gz-17hXMqdQ46nj")])]})]});
            var Q1;
            Q1=makeQuery(id+"F10.boolean.opBoolean","INTERSECT",EDGE,{"disambiguationData":[OD(0.0)],"derivedFrom":[makeQuery(id+"F1.opExtrude","SWEPT_FACE",FACE,{"disambiguationData":[OSD([sQuery(id+"F0.wireOp",EDGE,"E0")])]}),makeQuery(id+"F10.opExtrude","SWEPT_FACE",FACE,{"disambiguationData":[OSD([sQuery(id+"F9.wireOp",EDGE,"FsT2MfZt-GKtl-NsVv-VaLI-5vvhgEFZWlKT"),sQuery(id+"F9.wireOp",EDGE,"dlvRKOJ7-262f-HahC-D8FB-32DCdauAgm7j")])]})]});
            var Q2;
            Q2=makeQuery(id+"F10.boolean.opBoolean","INTERSECT",EDGE,{"disambiguationData":[OD(0.0)],"derivedFrom":[makeQuery(id+"F1.opExtrude","SWEPT_FACE",FACE,{"disambiguationData":[OSD([sQuery(id+"F0.wireOp",EDGE,"E0")])]}),makeQuery(id+"F10.opExtrude","SWEPT_FACE",FACE,{"disambiguationData":[OSD([sQuery(id+"F9.wireOp",EDGE,"YyubDx5s-D2ZM-0LxB-2Yu1-2PsOQiUhUxUO")])]})]});
            var Q3;
            Q3=makeQuery(id+"F10.boolean.opBoolean","INTERSECT",EDGE,{"disambiguationData":[OD(0.0)],"derivedFrom":[makeQuery(id+"F1.opExtrude","SWEPT_FACE",FACE,{"disambiguationData":[OSD([sQuery(id+"F0.wireOp",EDGE,"E0")])]}),makeQuery(id+"F10.opExtrude","SWEPT_FACE",FACE,{"disambiguationData":[OSD([sQuery(id+"F9.wireOp",EDGE,"E14.3")])]})]});
            var Q4;
            Q4=makeQuery(id+"F10.boolean.opBoolean","INTERSECT",EDGE,{"disambiguationData":[OD(0.0)],"derivedFrom":[makeQuery(id+"F1.opExtrude","SWEPT_FACE",FACE,{"disambiguationData":[OSD([sQuery(id+"F0.wireOp",EDGE,"E0")])]}),makeQuery(id+"F10.opExtrude","SWEPT_FACE",FACE,{"disambiguationData":[OSD([sQuery(id+"F9.wireOp",EDGE,"E14.2")])]})]});
            var Q5;
            Q5=makeQuery(id+"F10.boolean.opBoolean","INTERSECT",EDGE,{"disambiguationData":[OD(0.0)],"derivedFrom":[makeQuery(id+"F1.opExtrude","SWEPT_FACE",FACE,{"disambiguationData":[OSD([sQuery(id+"F0.wireOp",EDGE,"E0")])]}),makeQuery(id+"F10.opExtrude","SWEPT_FACE",FACE,{"disambiguationData":[OSD([sQuery(id+"F9.wireOp",EDGE,"E14.1")])]})]});
            var Q6;
            Q6=makeQuery(id+"F10.boolean.opBoolean","INTERSECT",EDGE,{"disambiguationData":[OD(0.0)],"derivedFrom":[makeQuery(id+"F1.opExtrude","SWEPT_FACE",FACE,{"disambiguationData":[OSD([sQuery(id+"F0.wireOp",EDGE,"E0")])]}),makeQuery(id+"F10.opExtrude","SWEPT_FACE",FACE,{"disambiguationData":[OSD([sQuery(id+"F9.wireOp",EDGE,"E14.0")])]})]});
            var Q7;
            Q7=makeQuery(id+"F10.boolean.opBoolean","INTERSECT",EDGE,{"disambiguationData":[OD(0.0)],"derivedFrom":[makeQuery(id+"F1.opExtrude","SWEPT_FACE",FACE,{"disambiguationData":[OSD([sQuery(id+"F0.wireOp",EDGE,"E0")])]}),makeQuery(id+"F10.opExtrude","SWEPT_FACE",FACE,{"disambiguationData":[OSD([sQuery(id+"F9.wireOp",EDGE,"E14.5")])]})]});
            var Q8;
            Q8=makeQuery(id+"F10.boolean.opBoolean","INTERSECT",EDGE,{"disambiguationData":[OD(0.0)],"derivedFrom":[makeQuery(id+"F1.opExtrude","SWEPT_FACE",FACE,{"disambiguationData":[OSD([sQuery(id+"F0.wireOp",EDGE,"E0")])]}),makeQuery(id+"F10.opExtrude","SWEPT_FACE",FACE,{"disambiguationData":[OSD([sQuery(id+"F9.wireOp",EDGE,"E14.4")])]})]});
            var Q9;
            Q9=makeQuery(id+"F10.boolean.opBoolean","INTERSECT",EDGE,{"disambiguationData":[OD(0.0)],"derivedFrom":[makeQuery(id+"F1.opExtrude","SWEPT_FACE",FACE,{"disambiguationData":[OSD([sQuery(id+"F0.wireOp",EDGE,"E0")])]}),makeQuery(id+"F10.opExtrude","SWEPT_FACE",FACE,{"disambiguationData":[OSD([sQuery(id+"F9.wireOp",EDGE,"E15.0.1.4")])]})]});
            var Q10;
            Q10=makeQuery(id+"F10.boolean.opBoolean","INTERSECT",EDGE,{"disambiguationData":[OD(0.0)],"derivedFrom":[makeQuery(id+"F1.opExtrude","SWEPT_FACE",FACE,{"disambiguationData":[OSD([sQuery(id+"F0.wireOp",EDGE,"E0")])]}),makeQuery(id+"F10.opExtrude","SWEPT_FACE",FACE,{"disambiguationData":[OSD([sQuery(id+"F9.wireOp",EDGE,"E15.0.1.7")])]})]});
            var Q11;
            Q11=makeQuery(id+"F10.boolean.opBoolean","INTERSECT",EDGE,{"disambiguationData":[OD(0.0)],"derivedFrom":[makeQuery(id+"F1.opExtrude","SWEPT_FACE",FACE,{"disambiguationData":[OSD([sQuery(id+"F0.wireOp",EDGE,"E0")])]}),makeQuery(id+"F10.opExtrude","SWEPT_FACE",FACE,{"disambiguationData":[OSD([sQuery(id+"F9.wireOp",EDGE,"E15.0.1.3")])]})]});
            var Q12;
            Q12=makeQuery(id+"F10.boolean.opBoolean","INTERSECT",EDGE,{"disambiguationData":[OD(0.0)],"derivedFrom":[makeQuery(id+"F1.opExtrude","SWEPT_FACE",FACE,{"disambiguationData":[OSD([sQuery(id+"F0.wireOp",EDGE,"E0")])]}),makeQuery(id+"F10.opExtrude","SWEPT_FACE",FACE,{"disambiguationData":[OSD([sQuery(id+"F9.wireOp",EDGE,"E15.0.1.2")])]})]});
            var Q13;
            Q13=makeQuery(id+"F10.boolean.opBoolean","INTERSECT",EDGE,{"disambiguationData":[OD(0.0)],"derivedFrom":[makeQuery(id+"F1.opExtrude","SWEPT_FACE",FACE,{"disambiguationData":[OSD([sQuery(id+"F0.wireOp",EDGE,"E0")])]}),makeQuery(id+"F10.opExtrude","SWEPT_FACE",FACE,{"disambiguationData":[OSD([sQuery(id+"F9.wireOp",EDGE,"E15.0.1.6")])]})]});
            var Q14;
            Q14=makeQuery(id+"F10.boolean.opBoolean","INTERSECT",EDGE,{"disambiguationData":[OD(0.0)],"derivedFrom":[makeQuery(id+"F1.opExtrude","SWEPT_FACE",FACE,{"disambiguationData":[OSD([sQuery(id+"F0.wireOp",EDGE,"E0")])]}),makeQuery(id+"F10.opExtrude","SWEPT_FACE",FACE,{"disambiguationData":[OSD([sQuery(id+"F9.wireOp",EDGE,"E15.0.1.5")])]})]});
            var Q15;
            Q15=makeQuery(id+"F10.boolean.opBoolean","INTERSECT",EDGE,{"disambiguationData":[OD(0.0)],"derivedFrom":[makeQuery(id+"F1.opExtrude","SWEPT_FACE",FACE,{"disambiguationData":[OSD([sQuery(id+"F0.wireOp",EDGE,"E0")])]}),makeQuery(id+"F10.opExtrude","SWEPT_FACE",FACE,{"disambiguationData":[OSD([sQuery(id+"F9.wireOp",EDGE,"E15.0.2.2")])]})]});
            var Q16;
            Q16=makeQuery(id+"F10.boolean.opBoolean","INTERSECT",EDGE,{"disambiguationData":[OD(0.0)],"derivedFrom":[makeQuery(id+"F1.opExtrude","SWEPT_FACE",FACE,{"disambiguationData":[OSD([sQuery(id+"F0.wireOp",EDGE,"E0")])]}),makeQuery(id+"F10.opExtrude","SWEPT_FACE",FACE,{"disambiguationData":[OSD([sQuery(id+"F9.wireOp",EDGE,"E15.0.2.6")])]})]});
            var Q17;
            Q17=makeQuery(id+"F10.boolean.opBoolean","COPY",EDGE,{"disambiguationData":[OD(0.0)],"derivedFrom":makeQuery(id+"F10.opExtrude","SWEPT_EDGE",EDGE,{"disambiguationData":[OSD([sQuery(id+"F9.wireOp",EDGE,"E15.0.2.6"),sQuery(id+"F9.wireOp",EDGE,"E15.0.2.7")])]})});
            var Q18;
            Q18=makeQuery(id+"F10.boolean.opBoolean","INTERSECT",EDGE,{"disambiguationData":[OD(0.0)],"derivedFrom":[makeQuery(id+"F1.opExtrude","SWEPT_FACE",FACE,{"disambiguationData":[OSD([sQuery(id+"F0.wireOp",EDGE,"E0")])]}),makeQuery(id+"F10.opExtrude","SWEPT_FACE",FACE,{"disambiguationData":[OSD([sQuery(id+"F9.wireOp",EDGE,"E15.0.2.5")])]})]});
            var Q19;
            Q19=makeQuery(id+"F10.boolean.opBoolean","INTERSECT",EDGE,{"disambiguationData":[OD(0.0)],"derivedFrom":[makeQuery(id+"F1.opExtrude","SWEPT_FACE",FACE,{"disambiguationData":[OSD([sQuery(id+"F0.wireOp",EDGE,"E0")])]}),makeQuery(id+"F10.opExtrude","SWEPT_FACE",FACE,{"disambiguationData":[OSD([sQuery(id+"F9.wireOp",EDGE,"E15.0.2.4")])]})]});
            var Q20;
            Q20=makeQuery(id+"F10.boolean.opBoolean","INTERSECT",EDGE,{"disambiguationData":[OD(0.0)],"derivedFrom":[makeQuery(id+"F1.opExtrude","SWEPT_FACE",FACE,{"disambiguationData":[OSD([sQuery(id+"F0.wireOp",EDGE,"E0")])]}),makeQuery(id+"F10.opExtrude","SWEPT_FACE",FACE,{"disambiguationData":[OSD([sQuery(id+"F9.wireOp",EDGE,"E15.0.2.3")])]})]});
            var Q21;
            Q21=makeQuery(id+"F10.boolean.opBoolean","INTERSECT",EDGE,{"disambiguationData":[OD(0.0)],"derivedFrom":[makeQuery(id+"F1.opExtrude","SWEPT_FACE",FACE,{"disambiguationData":[OSD([sQuery(id+"F0.wireOp",EDGE,"E0")])]}),makeQuery(id+"F10.opExtrude","SWEPT_FACE",FACE,{"disambiguationData":[OSD([sQuery(id+"F9.wireOp",EDGE,"E15.0.3.2")])]})]});
            var Q22;
            Q22=makeQuery(id+"F10.boolean.opBoolean","INTERSECT",EDGE,{"disambiguationData":[OD(0.0)],"derivedFrom":[makeQuery(id+"F1.opExtrude","SWEPT_FACE",FACE,{"disambiguationData":[OSD([sQuery(id+"F0.wireOp",EDGE,"E0")])]}),makeQuery(id+"F10.opExtrude","SWEPT_FACE",FACE,{"disambiguationData":[OSD([sQuery(id+"F9.wireOp",EDGE,"E15.0.3.6")])]})]});
            var Q23;
            Q23=makeQuery(id+"F10.boolean.opBoolean","COPY",EDGE,{"disambiguationData":[OD(0.0)],"derivedFrom":makeQuery(id+"F10.opExtrude","SWEPT_EDGE",EDGE,{"disambiguationData":[OSD([sQuery(id+"F9.wireOp",EDGE,"E15.0.3.6"),sQuery(id+"F9.wireOp",EDGE,"E15.0.3.7")])]})});
            var Q24;
            Q24=makeQuery(id+"F10.boolean.opBoolean","INTERSECT",EDGE,{"disambiguationData":[OD(0.0)],"derivedFrom":[makeQuery(id+"F1.opExtrude","SWEPT_FACE",FACE,{"disambiguationData":[OSD([sQuery(id+"F0.wireOp",EDGE,"E0")])]}),makeQuery(id+"F10.opExtrude","SWEPT_FACE",FACE,{"disambiguationData":[OSD([sQuery(id+"F9.wireOp",EDGE,"E15.0.3.5")])]})]});
            var Q25;
            Q25=makeQuery(id+"F10.boolean.opBoolean","INTERSECT",EDGE,{"disambiguationData":[OD(0.0)],"derivedFrom":[makeQuery(id+"F1.opExtrude","SWEPT_FACE",FACE,{"disambiguationData":[OSD([sQuery(id+"F0.wireOp",EDGE,"E0")])]}),makeQuery(id+"F10.opExtrude","SWEPT_FACE",FACE,{"disambiguationData":[OSD([sQuery(id+"F9.wireOp",EDGE,"E15.0.3.4")])]})]});
            var Q26;
            Q26=makeQuery(id+"F10.boolean.opBoolean","INTERSECT",EDGE,{"disambiguationData":[OD(0.0)],"derivedFrom":[makeQuery(id+"F1.opExtrude","SWEPT_FACE",FACE,{"disambiguationData":[OSD([sQuery(id+"F0.wireOp",EDGE,"E0")])]}),makeQuery(id+"F10.opExtrude","SWEPT_FACE",FACE,{"disambiguationData":[OSD([sQuery(id+"F9.wireOp",EDGE,"E15.0.3.3")])]})]});
            var Q27;
            Q27=makeQuery(id+"F10.boolean.opBoolean","INTERSECT",EDGE,{"disambiguationData":[OD(0.0)],"derivedFrom":[makeQuery(id+"F1.opExtrude","SWEPT_FACE",FACE,{"disambiguationData":[OSD([sQuery(id+"F0.wireOp",EDGE,"E0")])]}),makeQuery(id+"F10.opExtrude","SWEPT_FACE",FACE,{"disambiguationData":[OSD([sQuery(id+"F9.wireOp",EDGE,"E15.0.4.2")])]})]});
            var Q28;
            Q28=makeQuery(id+"F10.boolean.opBoolean","INTERSECT",EDGE,{"disambiguationData":[OD(0.0)],"derivedFrom":[makeQuery(id+"F1.opExtrude","SWEPT_FACE",FACE,{"disambiguationData":[OSD([sQuery(id+"F0.wireOp",EDGE,"E0")])]}),makeQuery(id+"F10.opExtrude","SWEPT_FACE",FACE,{"disambiguationData":[OSD([sQuery(id+"F9.wireOp",EDGE,"E15.0.5.2")])]})]});
            var Q29;
            Q29=makeQuery(id+"F10.boolean.opBoolean","INTERSECT",EDGE,{"disambiguationData":[OD(0.0)],"derivedFrom":[makeQuery(id+"F1.opExtrude","SWEPT_FACE",FACE,{"disambiguationData":[OSD([sQuery(id+"F0.wireOp",EDGE,"E0")])]}),makeQuery(id+"F10.opExtrude","SWEPT_FACE",FACE,{"disambiguationData":[OSD([sQuery(id+"F9.wireOp",EDGE,"E15.0.6.2")])]})]});
            var Q30;
            Q30=makeQuery(id+"F10.boolean.opBoolean","INTERSECT",EDGE,{"disambiguationData":[OD(0.0)],"derivedFrom":[makeQuery(id+"F1.opExtrude","SWEPT_FACE",FACE,{"disambiguationData":[OSD([sQuery(id+"F0.wireOp",EDGE,"E0")])]}),makeQuery(id+"F10.opExtrude","SWEPT_FACE",FACE,{"disambiguationData":[OSD([sQuery(id+"F9.wireOp",EDGE,"E15.0.7.2")])]})]});
            var Q31;
            Q31=makeQuery(id+"F10.boolean.opBoolean","INTERSECT",EDGE,{"disambiguationData":[OD(0.0)],"derivedFrom":[makeQuery(id+"F1.opExtrude","SWEPT_FACE",FACE,{"disambiguationData":[OSD([sQuery(id+"F0.wireOp",EDGE,"E0")])]}),makeQuery(id+"F10.opExtrude","SWEPT_FACE",FACE,{"disambiguationData":[OSD([sQuery(id+"F9.wireOp",EDGE,"E15.0.4.3")])]})]});
            var Q32;
            Q32=makeQuery(id+"F10.boolean.opBoolean","INTERSECT",EDGE,{"disambiguationData":[OD(0.0)],"derivedFrom":[makeQuery(id+"F1.opExtrude","SWEPT_FACE",FACE,{"disambiguationData":[OSD([sQuery(id+"F0.wireOp",EDGE,"E0")])]}),makeQuery(id+"F10.opExtrude","SWEPT_FACE",FACE,{"disambiguationData":[OSD([sQuery(id+"F9.wireOp",EDGE,"E15.0.4.6")])]})]});
            var Q33;
            Q33=makeQuery(id+"F10.boolean.opBoolean","INTERSECT",EDGE,{"disambiguationData":[OD(0.0)],"derivedFrom":[makeQuery(id+"F1.opExtrude","SWEPT_FACE",FACE,{"disambiguationData":[OSD([sQuery(id+"F0.wireOp",EDGE,"E0")])]}),makeQuery(id+"F10.opExtrude","SWEPT_FACE",FACE,{"disambiguationData":[OSD([sQuery(id+"F9.wireOp",EDGE,"E15.0.4.7")])]})]});
            var Q34;
            Q34=makeQuery(id+"F10.boolean.opBoolean","INTERSECT",EDGE,{"disambiguationData":[OD(0.0)],"derivedFrom":[makeQuery(id+"F1.opExtrude","SWEPT_FACE",FACE,{"disambiguationData":[OSD([sQuery(id+"F0.wireOp",EDGE,"E0")])]}),makeQuery(id+"F10.opExtrude","SWEPT_FACE",FACE,{"disambiguationData":[OSD([sQuery(id+"F9.wireOp",EDGE,"E15.0.4.5")])]})]});
            var Q35;
            Q35=makeQuery(id+"F10.boolean.opBoolean","INTERSECT",EDGE,{"disambiguationData":[OD(0.0)],"derivedFrom":[makeQuery(id+"F1.opExtrude","SWEPT_FACE",FACE,{"disambiguationData":[OSD([sQuery(id+"F0.wireOp",EDGE,"E0")])]}),makeQuery(id+"F10.opExtrude","SWEPT_FACE",FACE,{"disambiguationData":[OSD([sQuery(id+"F9.wireOp",EDGE,"E15.0.4.4")])]})]});
            var Q36;
            Q36=makeQuery(id+"F10.boolean.opBoolean","INTERSECT",EDGE,{"disambiguationData":[OD(0.0)],"derivedFrom":[makeQuery(id+"F1.opExtrude","SWEPT_FACE",FACE,{"disambiguationData":[OSD([sQuery(id+"F0.wireOp",EDGE,"E0")])]}),makeQuery(id+"F10.opExtrude","SWEPT_FACE",FACE,{"disambiguationData":[OSD([sQuery(id+"F9.wireOp",EDGE,"E15.0.5.3")])]})]});
            var Q37;
            Q37=makeQuery(id+"F10.boolean.opBoolean","INTERSECT",EDGE,{"disambiguationData":[OD(0.0)],"derivedFrom":[makeQuery(id+"F1.opExtrude","SWEPT_FACE",FACE,{"disambiguationData":[OSD([sQuery(id+"F0.wireOp",EDGE,"E0")])]}),makeQuery(id+"F10.opExtrude","SWEPT_FACE",FACE,{"disambiguationData":[OSD([sQuery(id+"F9.wireOp",EDGE,"E15.0.5.6")])]})]});
            var Q38;
            Q38=makeQuery(id+"F10.boolean.opBoolean","COPY",EDGE,{"disambiguationData":[OD(0.0)],"derivedFrom":makeQuery(id+"F10.opExtrude","SWEPT_EDGE",EDGE,{"disambiguationData":[OSD([sQuery(id+"F9.wireOp",EDGE,"E15.0.5.6"),sQuery(id+"F9.wireOp",EDGE,"E15.0.5.7")])]})});
            var Q39;
            Q39=makeQuery(id+"F10.boolean.opBoolean","INTERSECT",EDGE,{"disambiguationData":[OD(0.0)],"derivedFrom":[makeQuery(id+"F1.opExtrude","SWEPT_FACE",FACE,{"disambiguationData":[OSD([sQuery(id+"F0.wireOp",EDGE,"E0")])]}),makeQuery(id+"F10.opExtrude","SWEPT_FACE",FACE,{"disambiguationData":[OSD([sQuery(id+"F9.wireOp",EDGE,"E15.0.5.5")])]})]});
            var Q40;
            Q40=makeQuery(id+"F10.boolean.opBoolean","INTERSECT",EDGE,{"disambiguationData":[OD(0.0)],"derivedFrom":[makeQuery(id+"F1.opExtrude","SWEPT_FACE",FACE,{"disambiguationData":[OSD([sQuery(id+"F0.wireOp",EDGE,"E0")])]}),makeQuery(id+"F10.opExtrude","SWEPT_FACE",FACE,{"disambiguationData":[OSD([sQuery(id+"F9.wireOp",EDGE,"E15.0.5.4")])]})]});
            var Q41;
            Q41=makeQuery(id+"F10.boolean.opBoolean","INTERSECT",EDGE,{"disambiguationData":[OD(0.0)],"derivedFrom":[makeQuery(id+"F1.opExtrude","SWEPT_FACE",FACE,{"disambiguationData":[OSD([sQuery(id+"F0.wireOp",EDGE,"E0")])]}),makeQuery(id+"F10.opExtrude","SWEPT_FACE",FACE,{"disambiguationData":[OSD([sQuery(id+"F9.wireOp",EDGE,"E15.0.6.6")])]})]});
            var Q42;
            Q42=makeQuery(id+"F7.boolean.opBoolean","INTERSECT",EDGE,{"disambiguationData":[OD(0.0)],"derivedFrom":[makeQuery(id+"F1.opExtrude","SWEPT_FACE",FACE,{"disambiguationData":[OSD([sQuery(id+"F0.wireOp",EDGE,"E0")])]}),makeQuery(id+"F7.opExtrude","SWEPT_FACE",FACE,{"disambiguationData":[OSD([sQuery(id+"F6.wireOp",EDGE,"cfdfa16a-de7a-4601-9022-5211aa514822.4")])]})]});
            var Q43;
            Q43=makeQuery(id+"F7.boolean.opBoolean","INTERSECT",EDGE,{"disambiguationData":[OD(0.0)],"derivedFrom":[makeQuery(id+"F1.opExtrude","SWEPT_FACE",FACE,{"disambiguationData":[OSD([sQuery(id+"F0.wireOp",EDGE,"E0")])]}),makeQuery(id+"F7.opExtrude","SWEPT_FACE",FACE,{"disambiguationData":[OSD([sQuery(id+"F6.wireOp",EDGE,"09c30c40-169e-4e38-bf91-241d7524808d.5")])]})]});
            var Q44;
            Q44=makeQuery(id+"F10.boolean.opBoolean","INTERSECT",EDGE,{"disambiguationData":[OD(0.0)],"derivedFrom":[makeQuery(id+"F1.opExtrude","SWEPT_FACE",FACE,{"disambiguationData":[OSD([sQuery(id+"F0.wireOp",EDGE,"E0")])]}),makeQuery(id+"F10.opExtrude","SWEPT_FACE",FACE,{"disambiguationData":[OSD([sQuery(id+"F9.wireOp",EDGE,"E15.0.6.5")])]})]});
            var Q45;
            Q45=makeQuery(id+"F10.boolean.opBoolean","INTERSECT",EDGE,{"disambiguationData":[OD(0.0)],"derivedFrom":[makeQuery(id+"F1.opExtrude","SWEPT_FACE",FACE,{"disambiguationData":[OSD([sQuery(id+"F0.wireOp",EDGE,"E0")])]}),makeQuery(id+"F10.opExtrude","SWEPT_FACE",FACE,{"disambiguationData":[OSD([sQuery(id+"F9.wireOp",EDGE,"E15.0.6.7")])]})]});
            var Q46;
            Q46=makeQuery(id+"F10.boolean.opBoolean","INTERSECT",EDGE,{"disambiguationData":[OD(0.0)],"derivedFrom":[makeQuery(id+"F1.opExtrude","SWEPT_FACE",FACE,{"disambiguationData":[OSD([sQuery(id+"F0.wireOp",EDGE,"E0")])]}),makeQuery(id+"F10.opExtrude","SWEPT_FACE",FACE,{"disambiguationData":[OSD([sQuery(id+"F9.wireOp",EDGE,"E15.0.6.4")])]})]});
            var Q47;
            Q47=makeQuery(id+"F10.boolean.opBoolean","INTERSECT",EDGE,{"disambiguationData":[OD(0.0)],"derivedFrom":[makeQuery(id+"F1.opExtrude","SWEPT_FACE",FACE,{"disambiguationData":[OSD([sQuery(id+"F0.wireOp",EDGE,"E0")])]}),makeQuery(id+"F10.opExtrude","SWEPT_FACE",FACE,{"disambiguationData":[OSD([sQuery(id+"F9.wireOp",EDGE,"E15.0.6.3")])]})]});
            var Q48;
            Q48=makeQuery(id+"F10.boolean.opBoolean","INTERSECT",EDGE,{"disambiguationData":[OD(0.0)],"derivedFrom":[makeQuery(id+"F1.opExtrude","SWEPT_FACE",FACE,{"disambiguationData":[OSD([sQuery(id+"F0.wireOp",EDGE,"E0")])]}),makeQuery(id+"F10.opExtrude","SWEPT_FACE",FACE,{"disambiguationData":[OSD([sQuery(id+"F9.wireOp",EDGE,"E15.0.7.3")])]})]});
            var Q49;
            Q49=makeQuery(id+"F10.boolean.opBoolean","INTERSECT",EDGE,{"disambiguationData":[OD(0.0)],"derivedFrom":[makeQuery(id+"F1.opExtrude","SWEPT_FACE",FACE,{"disambiguationData":[OSD([sQuery(id+"F0.wireOp",EDGE,"E0")])]}),makeQuery(id+"F10.opExtrude","SWEPT_FACE",FACE,{"disambiguationData":[OSD([sQuery(id+"F9.wireOp",EDGE,"E15.0.7.6")])]})]});
            var Q50;
            Q50=makeQuery(id+"F10.boolean.opBoolean","INTERSECT",EDGE,{"disambiguationData":[OD(0.0)],"derivedFrom":[makeQuery(id+"F1.opExtrude","SWEPT_FACE",FACE,{"disambiguationData":[OSD([sQuery(id+"F0.wireOp",EDGE,"E0")])]}),makeQuery(id+"F10.opExtrude","SWEPT_FACE",FACE,{"disambiguationData":[OSD([sQuery(id+"F9.wireOp",EDGE,"E15.0.7.7")])]})]});
            var Q51;
            Q51=makeQuery(id+"F10.boolean.opBoolean","INTERSECT",EDGE,{"disambiguationData":[OD(0.0)],"derivedFrom":[makeQuery(id+"F1.opExtrude","SWEPT_FACE",FACE,{"disambiguationData":[OSD([sQuery(id+"F0.wireOp",EDGE,"E0")])]}),makeQuery(id+"F10.opExtrude","SWEPT_FACE",FACE,{"disambiguationData":[OSD([sQuery(id+"F9.wireOp",EDGE,"E15.0.7.5")])]})]});
            var Q52;
            Q52=makeQuery(id+"F10.boolean.opBoolean","INTERSECT",EDGE,{"disambiguationData":[OD(0.0)],"derivedFrom":[makeQuery(id+"F1.opExtrude","SWEPT_FACE",FACE,{"disambiguationData":[OSD([sQuery(id+"F0.wireOp",EDGE,"E0")])]}),makeQuery(id+"F10.opExtrude","SWEPT_FACE",FACE,{"disambiguationData":[OSD([sQuery(id+"F9.wireOp",EDGE,"E15.0.7.4")])]})]});
            var Q53;
            Q53=makeQuery(id+"F10.boolean.opBoolean","INTERSECT",EDGE,{"disambiguationData":[OD(0.0)],"derivedFrom":[makeQuery(id+"F1.opExtrude","SWEPT_FACE",FACE,{"disambiguationData":[OSD([sQuery(id+"F0.wireOp",EDGE,"E0")])]}),makeQuery(id+"F10.opExtrude","SWEPT_FACE",FACE,{"disambiguationData":[OSD([sQuery(id+"F9.wireOp",EDGE,"E15.0.8.2")])]})]});
            var Q54;
            Q54=makeQuery(id+"F10.boolean.opBoolean","INTERSECT",EDGE,{"disambiguationData":[OD(0.0)],"derivedFrom":[makeQuery(id+"F1.opExtrude","SWEPT_FACE",FACE,{"disambiguationData":[OSD([sQuery(id+"F0.wireOp",EDGE,"E0")])]}),makeQuery(id+"F10.opExtrude","SWEPT_FACE",FACE,{"disambiguationData":[OSD([sQuery(id+"F9.wireOp",EDGE,"E15.0.8.6")])]})]});
            var Q55;
            Q55=makeQuery(id+"F10.boolean.opBoolean","INTERSECT",EDGE,{"disambiguationData":[OD(0.0)],"derivedFrom":[makeQuery(id+"F1.opExtrude","SWEPT_FACE",FACE,{"disambiguationData":[OSD([sQuery(id+"F0.wireOp",EDGE,"E0")])]}),makeQuery(id+"F10.opExtrude","SWEPT_FACE",FACE,{"disambiguationData":[OSD([sQuery(id+"F9.wireOp",EDGE,"E15.0.8.7")])]})]});
            var Q56;
            Q56=makeQuery(id+"F10.boolean.opBoolean","INTERSECT",EDGE,{"disambiguationData":[OD(0.0)],"derivedFrom":[makeQuery(id+"F1.opExtrude","SWEPT_FACE",FACE,{"disambiguationData":[OSD([sQuery(id+"F0.wireOp",EDGE,"E0")])]}),makeQuery(id+"F10.opExtrude","SWEPT_FACE",FACE,{"disambiguationData":[OSD([sQuery(id+"F9.wireOp",EDGE,"E15.0.8.5")])]})]});
            var Q57;
            Q57=makeQuery(id+"F10.boolean.opBoolean","INTERSECT",EDGE,{"disambiguationData":[OD(0.0)],"derivedFrom":[makeQuery(id+"F1.opExtrude","SWEPT_FACE",FACE,{"disambiguationData":[OSD([sQuery(id+"F0.wireOp",EDGE,"E0")])]}),makeQuery(id+"F10.opExtrude","SWEPT_FACE",FACE,{"disambiguationData":[OSD([sQuery(id+"F9.wireOp",EDGE,"E15.0.8.4")])]})]});
            var Q58;
            Q58=makeQuery(id+"F10.boolean.opBoolean","INTERSECT",EDGE,{"disambiguationData":[OD(0.0)],"derivedFrom":[makeQuery(id+"F1.opExtrude","SWEPT_FACE",FACE,{"disambiguationData":[OSD([sQuery(id+"F0.wireOp",EDGE,"E0")])]}),makeQuery(id+"F10.opExtrude","SWEPT_FACE",FACE,{"disambiguationData":[OSD([sQuery(id+"F9.wireOp",EDGE,"E15.0.8.3")])]})]});
            var Q59;
            Q59=makeQuery(id+"F10.boolean.opBoolean","INTERSECT",EDGE,{"disambiguationData":[OD(0.0)],"derivedFrom":[makeQuery(id+"F1.opExtrude","SWEPT_FACE",FACE,{"disambiguationData":[OSD([sQuery(id+"F0.wireOp",EDGE,"E0")])]}),makeQuery(id+"F10.opExtrude","SWEPT_FACE",FACE,{"disambiguationData":[OSD([sQuery(id+"F9.wireOp",EDGE,"E15.0.9.6")])]})]});
            var Q60;
            Q60=makeQuery(id+"F10.boolean.opBoolean","INTERSECT",EDGE,{"disambiguationData":[OD(0.0)],"derivedFrom":[makeQuery(id+"F1.opExtrude","SWEPT_FACE",FACE,{"disambiguationData":[OSD([sQuery(id+"F0.wireOp",EDGE,"E0")])]}),makeQuery(id+"F10.opExtrude","SWEPT_FACE",FACE,{"disambiguationData":[OSD([sQuery(id+"F9.wireOp",EDGE,"E15.0.9.2")])]})]});
            var Q61;
            Q61=makeQuery(id+"F10.boolean.opBoolean","INTERSECT",EDGE,{"disambiguationData":[OD(0.0)],"derivedFrom":[makeQuery(id+"F1.opExtrude","SWEPT_FACE",FACE,{"disambiguationData":[OSD([sQuery(id+"F0.wireOp",EDGE,"E0")])]}),makeQuery(id+"F10.opExtrude","SWEPT_FACE",FACE,{"disambiguationData":[OSD([sQuery(id+"F9.wireOp",EDGE,"E15.0.9.3")])]})]});
            var Q62;
            Q62=makeQuery(id+"F10.boolean.opBoolean","INTERSECT",EDGE,{"disambiguationData":[OD(0.0)],"derivedFrom":[makeQuery(id+"F1.opExtrude","SWEPT_FACE",FACE,{"disambiguationData":[OSD([sQuery(id+"F0.wireOp",EDGE,"E0")])]}),makeQuery(id+"F10.opExtrude","SWEPT_FACE",FACE,{"disambiguationData":[OSD([sQuery(id+"F9.wireOp",EDGE,"E15.0.9.4")])]})]});
            var Q63;
            Q63=makeQuery(id+"F10.boolean.opBoolean","INTERSECT",EDGE,{"disambiguationData":[OD(0.0)],"derivedFrom":[makeQuery(id+"F1.opExtrude","SWEPT_FACE",FACE,{"disambiguationData":[OSD([sQuery(id+"F0.wireOp",EDGE,"E0")])]}),makeQuery(id+"F10.opExtrude","SWEPT_FACE",FACE,{"disambiguationData":[OSD([sQuery(id+"F9.wireOp",EDGE,"E15.0.9.5")])]})]});
            var Q64;
            Q64=makeQuery(id+"F10.boolean.opBoolean","INTERSECT",EDGE,{"disambiguationData":[OD(0.0)],"derivedFrom":[makeQuery(id+"F1.opExtrude","SWEPT_FACE",FACE,{"disambiguationData":[OSD([sQuery(id+"F0.wireOp",EDGE,"E0")])]}),makeQuery(id+"F10.opExtrude","SWEPT_FACE",FACE,{"disambiguationData":[OSD([sQuery(id+"F9.wireOp",EDGE,"E15.0.9.7")])]})]});
            var Q65;
            Q65=makeQuery(id+"F10.boolean.opBoolean","INTERSECT",EDGE,{"disambiguationData":[OD(0.0)],"derivedFrom":[makeQuery(id+"F1.opExtrude","SWEPT_FACE",FACE,{"disambiguationData":[OSD([sQuery(id+"F0.wireOp",EDGE,"E0")])]}),makeQuery(id+"F10.opExtrude","SWEPT_FACE",FACE,{"disambiguationData":[OSD([sQuery(id+"F9.wireOp",EDGE,"E15.0.10.6")])]})]});
            var Q66;
            Q66=makeQuery(id+"F10.boolean.opBoolean","INTERSECT",EDGE,{"disambiguationData":[OD(0.0)],"derivedFrom":[makeQuery(id+"F1.opExtrude","SWEPT_FACE",FACE,{"disambiguationData":[OSD([sQuery(id+"F0.wireOp",EDGE,"E0")])]}),makeQuery(id+"F10.opExtrude","SWEPT_FACE",FACE,{"disambiguationData":[OSD([sQuery(id+"F9.wireOp",EDGE,"E15.0.10.2")])]})]});
            var Q67;
            Q67=makeQuery(id+"F10.boolean.opBoolean","INTERSECT",EDGE,{"disambiguationData":[OD(0.0)],"derivedFrom":[makeQuery(id+"F1.opExtrude","SWEPT_FACE",FACE,{"disambiguationData":[OSD([sQuery(id+"F0.wireOp",EDGE,"E0")])]}),makeQuery(id+"F10.opExtrude","SWEPT_FACE",FACE,{"disambiguationData":[OSD([sQuery(id+"F9.wireOp",EDGE,"E15.0.10.3")])]})]});
            var Q68;
            Q68=makeQuery(id+"F10.boolean.opBoolean","INTERSECT",EDGE,{"disambiguationData":[OD(0.0)],"derivedFrom":[makeQuery(id+"F1.opExtrude","SWEPT_FACE",FACE,{"disambiguationData":[OSD([sQuery(id+"F0.wireOp",EDGE,"E0")])]}),makeQuery(id+"F10.opExtrude","SWEPT_FACE",FACE,{"disambiguationData":[OSD([sQuery(id+"F9.wireOp",EDGE,"E15.0.10.4")])]})]});
            var Q69;
            Q69=makeQuery(id+"F10.boolean.opBoolean","INTERSECT",EDGE,{"disambiguationData":[OD(0.0)],"derivedFrom":[makeQuery(id+"F1.opExtrude","SWEPT_FACE",FACE,{"disambiguationData":[OSD([sQuery(id+"F0.wireOp",EDGE,"E0")])]}),makeQuery(id+"F10.opExtrude","SWEPT_FACE",FACE,{"disambiguationData":[OSD([sQuery(id+"F9.wireOp",EDGE,"E15.0.10.5")])]})]});
            var Q70;
            Q70=makeQuery(id+"F10.boolean.opBoolean","COPY",EDGE,{"disambiguationData":[OD(0.0)],"derivedFrom":makeQuery(id+"F10.opExtrude","SWEPT_EDGE",EDGE,{"disambiguationData":[OSD([sQuery(id+"F9.wireOp",EDGE,"E15.0.10.6"),sQuery(id+"F9.wireOp",EDGE,"E15.0.10.7")])]})});
            var Q71;
            Q71=makeQuery(id+"F10.boolean.opBoolean","INTERSECT",EDGE,{"disambiguationData":[OD(0.0)],"derivedFrom":[makeQuery(id+"F1.opExtrude","SWEPT_FACE",FACE,{"disambiguationData":[OSD([sQuery(id+"F0.wireOp",EDGE,"E0")])]}),makeQuery(id+"F10.opExtrude","SWEPT_FACE",FACE,{"disambiguationData":[OSD([sQuery(id+"F9.wireOp",EDGE,"E15.0.11.6")])]})]});
            var Q72;
            Q72=makeQuery(id+"F10.boolean.opBoolean","INTERSECT",EDGE,{"disambiguationData":[OD(0.0)],"derivedFrom":[makeQuery(id+"F1.opExtrude","SWEPT_FACE",FACE,{"disambiguationData":[OSD([sQuery(id+"F0.wireOp",EDGE,"E0")])]}),makeQuery(id+"F10.opExtrude","SWEPT_FACE",FACE,{"disambiguationData":[OSD([sQuery(id+"F9.wireOp",EDGE,"E15.0.11.2")])]})]});
            var Q73;
            Q73=makeQuery(id+"F10.boolean.opBoolean","INTERSECT",EDGE,{"disambiguationData":[OD(0.0)],"derivedFrom":[makeQuery(id+"F1.opExtrude","SWEPT_FACE",FACE,{"disambiguationData":[OSD([sQuery(id+"F0.wireOp",EDGE,"E0")])]}),makeQuery(id+"F10.opExtrude","SWEPT_FACE",FACE,{"disambiguationData":[OSD([sQuery(id+"F9.wireOp",EDGE,"E15.0.11.3")])]})]});
            var Q74;
            Q74=makeQuery(id+"F10.boolean.opBoolean","INTERSECT",EDGE,{"disambiguationData":[OD(0.0)],"derivedFrom":[makeQuery(id+"F1.opExtrude","SWEPT_FACE",FACE,{"disambiguationData":[OSD([sQuery(id+"F0.wireOp",EDGE,"E0")])]}),makeQuery(id+"F10.opExtrude","SWEPT_FACE",FACE,{"disambiguationData":[OSD([sQuery(id+"F9.wireOp",EDGE,"E15.0.11.4")])]})]});
            var Q75;
            Q75=makeQuery(id+"F10.boolean.opBoolean","INTERSECT",EDGE,{"disambiguationData":[OD(0.0)],"derivedFrom":[makeQuery(id+"F1.opExtrude","SWEPT_FACE",FACE,{"disambiguationData":[OSD([sQuery(id+"F0.wireOp",EDGE,"E0")])]}),makeQuery(id+"F10.opExtrude","SWEPT_FACE",FACE,{"disambiguationData":[OSD([sQuery(id+"F9.wireOp",EDGE,"E15.0.11.5")])]})]});
            var Q76;
            Q76=makeQuery(id+"F10.boolean.opBoolean","INTERSECT",EDGE,{"disambiguationData":[OD(0.0)],"derivedFrom":[makeQuery(id+"F1.opExtrude","SWEPT_FACE",FACE,{"disambiguationData":[OSD([sQuery(id+"F0.wireOp",EDGE,"E0")])]}),makeQuery(id+"F10.opExtrude","SWEPT_FACE",FACE,{"disambiguationData":[OSD([sQuery(id+"F9.wireOp",EDGE,"E15.0.11.7")])]})]});
            var Q77;
            Q77=makeQuery(id+"F10.boolean.opBoolean","INTERSECT",EDGE,{"disambiguationData":[OD(0.0)],"derivedFrom":[makeQuery(id+"F1.opExtrude","SWEPT_FACE",FACE,{"disambiguationData":[OSD([sQuery(id+"F0.wireOp",EDGE,"E0")])]}),makeQuery(id+"F10.opExtrude","SWEPT_FACE",FACE,{"disambiguationData":[OSD([sQuery(id+"F9.wireOp",EDGE,"E15.0.12.6")])]})]});
            var Q78;
            Q78=makeQuery(id+"F10.boolean.opBoolean","INTERSECT",EDGE,{"disambiguationData":[OD(0.0)],"derivedFrom":[makeQuery(id+"F1.opExtrude","SWEPT_FACE",FACE,{"disambiguationData":[OSD([sQuery(id+"F0.wireOp",EDGE,"E0")])]}),makeQuery(id+"F10.opExtrude","SWEPT_FACE",FACE,{"disambiguationData":[OSD([sQuery(id+"F9.wireOp",EDGE,"E15.0.12.2")])]})]});
            var Q79;
            Q79=makeQuery(id+"F10.boolean.opBoolean","INTERSECT",EDGE,{"disambiguationData":[OD(0.0)],"derivedFrom":[makeQuery(id+"F1.opExtrude","SWEPT_FACE",FACE,{"disambiguationData":[OSD([sQuery(id+"F0.wireOp",EDGE,"E0")])]}),makeQuery(id+"F10.opExtrude","SWEPT_FACE",FACE,{"disambiguationData":[OSD([sQuery(id+"F9.wireOp",EDGE,"E15.0.12.3")])]})]});
            var Q80;
            Q80=makeQuery(id+"F10.boolean.opBoolean","INTERSECT",EDGE,{"disambiguationData":[OD(0.0)],"derivedFrom":[makeQuery(id+"F1.opExtrude","SWEPT_FACE",FACE,{"disambiguationData":[OSD([sQuery(id+"F0.wireOp",EDGE,"E0")])]}),makeQuery(id+"F10.opExtrude","SWEPT_FACE",FACE,{"disambiguationData":[OSD([sQuery(id+"F9.wireOp",EDGE,"E15.0.12.4")])]})]});
            var Q81;
            Q81=makeQuery(id+"F10.boolean.opBoolean","INTERSECT",EDGE,{"disambiguationData":[OD(0.0)],"derivedFrom":[makeQuery(id+"F1.opExtrude","SWEPT_FACE",FACE,{"disambiguationData":[OSD([sQuery(id+"F0.wireOp",EDGE,"E0")])]}),makeQuery(id+"F10.opExtrude","SWEPT_FACE",FACE,{"disambiguationData":[OSD([sQuery(id+"F9.wireOp",EDGE,"E15.0.12.5")])]})]});
            var Q82;
            Q82=makeQuery(id+"F10.boolean.opBoolean","INTERSECT",EDGE,{"disambiguationData":[OD(0.0)],"derivedFrom":[makeQuery(id+"F1.opExtrude","SWEPT_FACE",FACE,{"disambiguationData":[OSD([sQuery(id+"F0.wireOp",EDGE,"E0")])]}),makeQuery(id+"F10.opExtrude","SWEPT_FACE",FACE,{"disambiguationData":[OSD([sQuery(id+"F9.wireOp",EDGE,"E15.0.12.7")])]})]});
            var Q83;
            Q83=makeQuery(id+"F10.boolean.opBoolean","INTERSECT",EDGE,{"disambiguationData":[OD(0.0)],"derivedFrom":[makeQuery(id+"F1.opExtrude","SWEPT_FACE",FACE,{"disambiguationData":[OSD([sQuery(id+"F0.wireOp",EDGE,"E0")])]}),makeQuery(id+"F10.opExtrude","SWEPT_FACE",FACE,{"disambiguationData":[OSD([sQuery(id+"F9.wireOp",EDGE,"E21")])]})]});
            var Q84;
            Q84=makeQuery(id+"F10.boolean.opBoolean","INTERSECT",EDGE,{"disambiguationData":[OD(0.0)],"derivedFrom":[makeQuery(id+"F1.opExtrude","SWEPT_FACE",FACE,{"disambiguationData":[OSD([sQuery(id+"F0.wireOp",EDGE,"E0")])]}),makeQuery(id+"F10.opExtrude","SWEPT_FACE",FACE,{"disambiguationData":[OSD([sQuery(id+"F9.wireOp",EDGE,"E17.3")])]})]});
            var Q85;
            Q85=makeQuery(id+"F10.boolean.opBoolean","INTERSECT",EDGE,{"disambiguationData":[OD(0.0)],"derivedFrom":[makeQuery(id+"F1.opExtrude","SWEPT_FACE",FACE,{"disambiguationData":[OSD([sQuery(id+"F0.wireOp",EDGE,"E0")])]}),makeQuery(id+"F10.opExtrude","SWEPT_FACE",FACE,{"disambiguationData":[OSD([sQuery(id+"F9.wireOp",EDGE,"E22")])]})]});
            var Q86;
            Q86=makeQuery(id+"F10.boolean.opBoolean","INTERSECT",EDGE,{"disambiguationData":[OD(0.0)],"derivedFrom":[makeQuery(id+"F1.opExtrude","SWEPT_FACE",FACE,{"disambiguationData":[OSD([sQuery(id+"F0.wireOp",EDGE,"E0")])]}),makeQuery(id+"F10.opExtrude","SWEPT_FACE",FACE,{"disambiguationData":[OSD([sQuery(id+"F9.wireOp",EDGE,"E19"),sQuery(id+"F9.wireOp",EDGE,"E20")])]})]});
            var Q87;
            Q87=makeQuery(id+"F5.boolean.opBoolean","INTERSECT",EDGE,{"disambiguationData":[OD(0.0)],"derivedFrom":[makeQuery(id+"F1.opExtrude","SWEPT_FACE",FACE,{"disambiguationData":[OSD([sQuery(id+"F0.wireOp",EDGE,"E0")])]}),makeQuery(id+"F5.opExtrude","SWEPT_FACE",FACE,{"disambiguationData":[OSD([sQuery(id+"F4.wireOp",EDGE,"E4.3")])]})]});
            var Q88;
            Q88=makeQuery(id+"F5.boolean.opBoolean","INTERSECT",EDGE,{"disambiguationData":[OD(0.0)],"derivedFrom":[makeQuery(id+"F1.opExtrude","SWEPT_FACE",FACE,{"disambiguationData":[OSD([sQuery(id+"F0.wireOp",EDGE,"E0")])]}),makeQuery(id+"F5.opExtrude","SWEPT_FACE",FACE,{"disambiguationData":[OSD([sQuery(id+"F4.wireOp",EDGE,"E4.2")])]})]});
            var Q89;
            Q89=makeQuery(id+"F5.boolean.opBoolean","INTERSECT",EDGE,{"disambiguationData":[OD(0.0)],"derivedFrom":[makeQuery(id+"F1.opExtrude","SWEPT_FACE",FACE,{"disambiguationData":[OSD([sQuery(id+"F0.wireOp",EDGE,"E0")])]}),makeQuery(id+"F5.opExtrude","SWEPT_FACE",FACE,{"disambiguationData":[OSD([sQuery(id+"F4.wireOp",EDGE,"E4.1")])]})]});
            var Q90;
            Q90=makeQuery(id+"F5.boolean.opBoolean","INTERSECT",EDGE,{"disambiguationData":[OD(0.0)],"derivedFrom":[makeQuery(id+"F1.opExtrude","SWEPT_FACE",FACE,{"disambiguationData":[OSD([sQuery(id+"F0.wireOp",EDGE,"E0")])]}),makeQuery(id+"F5.opExtrude","SWEPT_FACE",FACE,{"disambiguationData":[OSD([sQuery(id+"F4.wireOp",EDGE,"E4.0")])]})]});
            var Q91;
            Q91=makeQuery(id+"F5.boolean.opBoolean","INTERSECT",EDGE,{"disambiguationData":[OD(0.0)],"derivedFrom":[makeQuery(id+"F1.opExtrude","SWEPT_FACE",FACE,{"disambiguationData":[OSD([sQuery(id+"F0.wireOp",EDGE,"E0")])]}),makeQuery(id+"F5.opExtrude","SWEPT_FACE",FACE,{"disambiguationData":[OSD([sQuery(id+"F4.wireOp",EDGE,"E4.5")])]})]});
            var Q92;
            Q92=makeQuery(id+"F5.boolean.opBoolean","INTERSECT",EDGE,{"disambiguationData":[OD(0.0)],"derivedFrom":[makeQuery(id+"F1.opExtrude","SWEPT_FACE",FACE,{"disambiguationData":[OSD([sQuery(id+"F0.wireOp",EDGE,"E0")])]}),makeQuery(id+"F5.opExtrude","SWEPT_FACE",FACE,{"disambiguationData":[OSD([sQuery(id+"F4.wireOp",EDGE,"E4.4")])]})]});
            var Q93;
            Q93=makeQuery(id+"F5.boolean.opBoolean","INTERSECT",EDGE,{"disambiguationData":[OD(0.0)],"derivedFrom":[makeQuery(id+"F1.opExtrude","SWEPT_FACE",FACE,{"disambiguationData":[OSD([sQuery(id+"F0.wireOp",EDGE,"E0")])]}),makeQuery(id+"F5.opExtrude","SWEPT_FACE",FACE,{"disambiguationData":[OSD([sQuery(id+"F4.wireOp",EDGE,"E5.0.1.1")])]})]});
            var Q94;
            Q94=makeQuery(id+"F5.boolean.opBoolean","INTERSECT",EDGE,{"disambiguationData":[OD(0.0)],"derivedFrom":[makeQuery(id+"F1.opExtrude","SWEPT_FACE",FACE,{"disambiguationData":[OSD([sQuery(id+"F0.wireOp",EDGE,"E0")])]}),makeQuery(id+"F5.opExtrude","SWEPT_FACE",FACE,{"disambiguationData":[OSD([sQuery(id+"F4.wireOp",EDGE,"E5.0.1.2")])]})]});
            var Q95;
            Q95=makeQuery(id+"F5.boolean.opBoolean","INTERSECT",EDGE,{"disambiguationData":[OD(0.0)],"derivedFrom":[makeQuery(id+"F1.opExtrude","SWEPT_FACE",FACE,{"disambiguationData":[OSD([sQuery(id+"F0.wireOp",EDGE,"E0")])]}),makeQuery(id+"F5.opExtrude","SWEPT_FACE",FACE,{"disambiguationData":[OSD([sQuery(id+"F4.wireOp",EDGE,"E5.0.1.3")])]})]});
            var Q96;
            Q96=makeQuery(id+"F5.boolean.opBoolean","INTERSECT",EDGE,{"disambiguationData":[OD(0.0)],"derivedFrom":[makeQuery(id+"F1.opExtrude","SWEPT_FACE",FACE,{"disambiguationData":[OSD([sQuery(id+"F0.wireOp",EDGE,"E0")])]}),makeQuery(id+"F5.opExtrude","SWEPT_FACE",FACE,{"disambiguationData":[OSD([sQuery(id+"F4.wireOp",EDGE,"E5.0.1.4")])]})]});
            var Q97;
            Q97=makeQuery(id+"F5.boolean.opBoolean","INTERSECT",EDGE,{"disambiguationData":[OD(0.0)],"derivedFrom":[makeQuery(id+"F1.opExtrude","SWEPT_FACE",FACE,{"disambiguationData":[OSD([sQuery(id+"F0.wireOp",EDGE,"E0")])]}),makeQuery(id+"F5.opExtrude","SWEPT_FACE",FACE,{"disambiguationData":[OSD([sQuery(id+"F4.wireOp",EDGE,"E5.0.1.0")])]})]});
            var Q98;
            Q98=makeQuery(id+"F5.boolean.opBoolean","INTERSECT",EDGE,{"disambiguationData":[OD(0.0)],"derivedFrom":[makeQuery(id+"F1.opExtrude","SWEPT_FACE",FACE,{"disambiguationData":[OSD([sQuery(id+"F0.wireOp",EDGE,"E0")])]}),makeQuery(id+"F5.opExtrude","SWEPT_FACE",FACE,{"disambiguationData":[OSD([sQuery(id+"F4.wireOp",EDGE,"E5.0.1.7")])]})]});
            var Q99;
            Q99=makeQuery(id+"F5.boolean.opBoolean","INTERSECT",EDGE,{"disambiguationData":[OD(0.0)],"derivedFrom":[makeQuery(id+"F1.opExtrude","SWEPT_FACE",FACE,{"disambiguationData":[OSD([sQuery(id+"F0.wireOp",EDGE,"E0")])]}),makeQuery(id+"F5.opExtrude","SWEPT_FACE",FACE,{"disambiguationData":[OSD([sQuery(id+"F4.wireOp",EDGE,"E5.0.2.1")])]})]});
            var Q100;
            Q100=makeQuery(id+"F5.boolean.opBoolean","INTERSECT",EDGE,{"disambiguationData":[OD(0.0)],"derivedFrom":[makeQuery(id+"F1.opExtrude","SWEPT_FACE",FACE,{"disambiguationData":[OSD([sQuery(id+"F0.wireOp",EDGE,"E0")])]}),makeQuery(id+"F5.opExtrude","SWEPT_FACE",FACE,{"disambiguationData":[OSD([sQuery(id+"F4.wireOp",EDGE,"E5.0.2.2")])]})]});
            var Q101;
            Q101=makeQuery(id+"F5.boolean.opBoolean","INTERSECT",EDGE,{"disambiguationData":[OD(0.0)],"derivedFrom":[makeQuery(id+"F1.opExtrude","SWEPT_FACE",FACE,{"disambiguationData":[OSD([sQuery(id+"F0.wireOp",EDGE,"E0")])]}),makeQuery(id+"F5.opExtrude","SWEPT_FACE",FACE,{"disambiguationData":[OSD([sQuery(id+"F4.wireOp",EDGE,"E5.0.2.3")])]})]});
            var Q102;
            Q102=makeQuery(id+"F5.boolean.opBoolean","INTERSECT",EDGE,{"disambiguationData":[OD(0.0)],"derivedFrom":[makeQuery(id+"F1.opExtrude","SWEPT_FACE",FACE,{"disambiguationData":[OSD([sQuery(id+"F0.wireOp",EDGE,"E0")])]}),makeQuery(id+"F5.opExtrude","SWEPT_FACE",FACE,{"disambiguationData":[OSD([sQuery(id+"F4.wireOp",EDGE,"E5.0.2.4")])]})]});
            var Q103;
            Q103=makeQuery(id+"F5.boolean.opBoolean","INTERSECT",EDGE,{"disambiguationData":[OD(0.0)],"derivedFrom":[makeQuery(id+"F1.opExtrude","SWEPT_FACE",FACE,{"disambiguationData":[OSD([sQuery(id+"F0.wireOp",EDGE,"E0")])]}),makeQuery(id+"F5.opExtrude","SWEPT_FACE",FACE,{"disambiguationData":[OSD([sQuery(id+"F4.wireOp",EDGE,"E5.0.2.0")])]})]});
            var Q104;
            Q104=makeQuery(id+"F5.boolean.opBoolean","INTERSECT",EDGE,{"disambiguationData":[OD(0.0)],"derivedFrom":[makeQuery(id+"F1.opExtrude","SWEPT_FACE",FACE,{"disambiguationData":[OSD([sQuery(id+"F0.wireOp",EDGE,"E0")])]}),makeQuery(id+"F5.opExtrude","SWEPT_FACE",FACE,{"disambiguationData":[OSD([sQuery(id+"F4.wireOp",EDGE,"E5.0.2.7")])]})]});
            var Q105;
            Q105=makeQuery(id+"F5.boolean.opBoolean","INTERSECT",EDGE,{"disambiguationData":[OD(0.0)],"derivedFrom":[makeQuery(id+"F1.opExtrude","SWEPT_FACE",FACE,{"disambiguationData":[OSD([sQuery(id+"F0.wireOp",EDGE,"E0")])]}),makeQuery(id+"F5.opExtrude","SWEPT_FACE",FACE,{"disambiguationData":[OSD([sQuery(id+"F4.wireOp",EDGE,"E5.0.3.1")])]})]});
            var Q106;
            Q106=makeQuery(id+"F5.boolean.opBoolean","INTERSECT",EDGE,{"disambiguationData":[OD(0.0)],"derivedFrom":[makeQuery(id+"F1.opExtrude","SWEPT_FACE",FACE,{"disambiguationData":[OSD([sQuery(id+"F0.wireOp",EDGE,"E0")])]}),makeQuery(id+"F5.opExtrude","SWEPT_FACE",FACE,{"disambiguationData":[OSD([sQuery(id+"F4.wireOp",EDGE,"E5.0.3.2")])]})]});
            var Q107;
            Q107=makeQuery(id+"F5.boolean.opBoolean","INTERSECT",EDGE,{"disambiguationData":[OD(0.0)],"derivedFrom":[makeQuery(id+"F1.opExtrude","SWEPT_FACE",FACE,{"disambiguationData":[OSD([sQuery(id+"F0.wireOp",EDGE,"E0")])]}),makeQuery(id+"F5.opExtrude","SWEPT_FACE",FACE,{"disambiguationData":[OSD([sQuery(id+"F4.wireOp",EDGE,"E5.0.3.3")])]})]});
            var Q108;
            Q108=makeQuery(id+"F5.boolean.opBoolean","INTERSECT",EDGE,{"disambiguationData":[OD(0.0)],"derivedFrom":[makeQuery(id+"F1.opExtrude","SWEPT_FACE",FACE,{"disambiguationData":[OSD([sQuery(id+"F0.wireOp",EDGE,"E0")])]}),makeQuery(id+"F5.opExtrude","SWEPT_FACE",FACE,{"disambiguationData":[OSD([sQuery(id+"F4.wireOp",EDGE,"E5.0.3.4")])]})]});
            var Q109;
            Q109=makeQuery(id+"F5.boolean.opBoolean","INTERSECT",EDGE,{"disambiguationData":[OD(0.0)],"derivedFrom":[makeQuery(id+"F1.opExtrude","SWEPT_FACE",FACE,{"disambiguationData":[OSD([sQuery(id+"F0.wireOp",EDGE,"E0")])]}),makeQuery(id+"F5.opExtrude","SWEPT_FACE",FACE,{"disambiguationData":[OSD([sQuery(id+"F4.wireOp",EDGE,"E5.0.3.0")])]})]});
            var Q110;
            Q110=makeQuery(id+"F5.boolean.opBoolean","INTERSECT",EDGE,{"disambiguationData":[OD(0.0)],"derivedFrom":[makeQuery(id+"F1.opExtrude","SWEPT_FACE",FACE,{"disambiguationData":[OSD([sQuery(id+"F0.wireOp",EDGE,"E0")])]}),makeQuery(id+"F5.opExtrude","SWEPT_FACE",FACE,{"disambiguationData":[OSD([sQuery(id+"F4.wireOp",EDGE,"E5.0.3.7")])]})]});
            var Q111;
            Q111=makeQuery(id+"F7.boolean.opBoolean","INTERSECT",EDGE,{"disambiguationData":[OD(0.0)],"derivedFrom":[makeQuery(id+"F1.opExtrude","SWEPT_FACE",FACE,{"disambiguationData":[OSD([sQuery(id+"F0.wireOp",EDGE,"E0")])]}),makeQuery(id+"F7.opExtrude","SWEPT_FACE",FACE,{"disambiguationData":[OSD([sQuery(id+"F6.wireOp",EDGE,"cfdfa16a-de7a-4601-9022-5211aa514822.1")])]})]});
            var Q112;
            Q112=makeQuery(id+"F7.boolean.opBoolean","INTERSECT",EDGE,{"disambiguationData":[OD(0.0)],"derivedFrom":[makeQuery(id+"F1.opExtrude","SWEPT_FACE",FACE,{"disambiguationData":[OSD([sQuery(id+"F0.wireOp",EDGE,"E0")])]}),makeQuery(id+"F7.opExtrude","SWEPT_FACE",FACE,{"disambiguationData":[OSD([sQuery(id+"F6.wireOp",EDGE,"cfdfa16a-de7a-4601-9022-5211aa514822.2")])]})]});
            var Q113;
            Q113=makeQuery(id+"F7.boolean.opBoolean","INTERSECT",EDGE,{"disambiguationData":[OD(0.0)],"derivedFrom":[makeQuery(id+"F1.opExtrude","SWEPT_FACE",FACE,{"disambiguationData":[OSD([sQuery(id+"F0.wireOp",EDGE,"E0")])]}),makeQuery(id+"F7.opExtrude","SWEPT_FACE",FACE,{"disambiguationData":[OSD([sQuery(id+"F6.wireOp",EDGE,"cfdfa16a-de7a-4601-9022-5211aa514822.3")])]})]});
            var Q114;
            Q114=makeQuery(id+"F7.boolean.opBoolean","INTERSECT",EDGE,{"disambiguationData":[OD(0.0)],"derivedFrom":[makeQuery(id+"F1.opExtrude","SWEPT_FACE",FACE,{"disambiguationData":[OSD([sQuery(id+"F0.wireOp",EDGE,"E0")])]}),makeQuery(id+"F7.opExtrude","SWEPT_FACE",FACE,{"disambiguationData":[OSD([sQuery(id+"F6.wireOp",EDGE,"cfdfa16a-de7a-4601-9022-5211aa514822.5")])]})]});
            var Q115;
            Q115=makeQuery(id+"F7.boolean.opBoolean","INTERSECT",EDGE,{"disambiguationData":[OD(0.0)],"derivedFrom":[makeQuery(id+"F1.opExtrude","SWEPT_FACE",FACE,{"disambiguationData":[OSD([sQuery(id+"F0.wireOp",EDGE,"E0")])]}),makeQuery(id+"F7.opExtrude","SWEPT_FACE",FACE,{"disambiguationData":[OSD([sQuery(id+"F6.wireOp",EDGE,"cfdfa16a-de7a-4601-9022-5211aa514822.0")])]})]});
            var Q116;
            Q116=makeQuery(id+"F7.boolean.opBoolean","INTERSECT",EDGE,{"disambiguationData":[OD(0.0)],"derivedFrom":[makeQuery(id+"F1.opExtrude","SWEPT_FACE",FACE,{"disambiguationData":[OSD([sQuery(id+"F0.wireOp",EDGE,"E0")])]}),makeQuery(id+"F7.opExtrude","SWEPT_FACE",FACE,{"disambiguationData":[OSD([sQuery(id+"F6.wireOp",EDGE,"6fecd9f8-48d6-48ad-88a1-144c9b17d822.3")])]})]});
            var Q117;
            Q117=makeQuery(id+"F7.boolean.opBoolean","INTERSECT",EDGE,{"disambiguationData":[OD(0.0)],"derivedFrom":[makeQuery(id+"F1.opExtrude","SWEPT_FACE",FACE,{"disambiguationData":[OSD([sQuery(id+"F0.wireOp",EDGE,"E0")])]}),makeQuery(id+"F7.opExtrude","SWEPT_FACE",FACE,{"disambiguationData":[OSD([sQuery(id+"F6.wireOp",EDGE,"6fecd9f8-48d6-48ad-88a1-144c9b17d822.2")])]})]});
            var Q118;
            Q118=makeQuery(id+"F7.boolean.opBoolean","INTERSECT",EDGE,{"disambiguationData":[OD(0.0)],"derivedFrom":[makeQuery(id+"F1.opExtrude","SWEPT_FACE",FACE,{"disambiguationData":[OSD([sQuery(id+"F0.wireOp",EDGE,"E0")])]}),makeQuery(id+"F7.opExtrude","SWEPT_FACE",FACE,{"disambiguationData":[OSD([sQuery(id+"F6.wireOp",EDGE,"6fecd9f8-48d6-48ad-88a1-144c9b17d822.1")])]})]});
            var Q119;
            Q119=makeQuery(id+"F7.boolean.opBoolean","INTERSECT",EDGE,{"disambiguationData":[OD(0.0)],"derivedFrom":[makeQuery(id+"F1.opExtrude","SWEPT_FACE",FACE,{"disambiguationData":[OSD([sQuery(id+"F0.wireOp",EDGE,"E0")])]}),makeQuery(id+"F7.opExtrude","SWEPT_FACE",FACE,{"disambiguationData":[OSD([sQuery(id+"F6.wireOp",EDGE,"6fecd9f8-48d6-48ad-88a1-144c9b17d822.0")])]})]});
            var Q120;
            Q120=makeQuery(id+"F7.boolean.opBoolean","INTERSECT",EDGE,{"disambiguationData":[OD(0.0)],"derivedFrom":[makeQuery(id+"F1.opExtrude","SWEPT_FACE",FACE,{"disambiguationData":[OSD([sQuery(id+"F0.wireOp",EDGE,"E0")])]}),makeQuery(id+"F7.opExtrude","SWEPT_FACE",FACE,{"disambiguationData":[OSD([sQuery(id+"F6.wireOp",EDGE,"6fecd9f8-48d6-48ad-88a1-144c9b17d822.5")])]})]});
            var Q121;
            Q121=makeQuery(id+"F7.boolean.opBoolean","INTERSECT",EDGE,{"disambiguationData":[OD(0.0)],"derivedFrom":[makeQuery(id+"F1.opExtrude","SWEPT_FACE",FACE,{"disambiguationData":[OSD([sQuery(id+"F0.wireOp",EDGE,"E0")])]}),makeQuery(id+"F7.opExtrude","SWEPT_FACE",FACE,{"disambiguationData":[OSD([sQuery(id+"F6.wireOp",EDGE,"6fecd9f8-48d6-48ad-88a1-144c9b17d822.4")])]})]});
            fillet(context, id + "F15", {"entities" : qUnion([Q0, Q1, Q2, Q3, Q4, Q5, Q6, Q7, Q8, Q9, Q10, Q11, Q12, Q13, Q14, Q15, Q16, Q17, Q18, Q19, Q20, Q21, Q22, Q23, Q24, Q25, Q26, Q27, Q28, Q29, Q30, Q31, Q32, Q33, Q34, Q35, Q36, Q37, Q38, Q39, Q40, Q41, Q42, Q43, Q44, Q45, Q46, Q47, Q48, Q49, Q50, Q51, Q52, Q53, Q54, Q55, Q56, Q57, Q58, Q59, Q60, Q61, Q62, Q63, Q64, Q65, Q66, Q67, Q68, Q69, Q70, Q71, Q72, Q73, Q74, Q75, Q76, Q77, Q78, Q79, Q80, Q81, Q82, Q83, Q84, Q85, Q86, Q87, Q88, Q89, Q90, Q91, Q92, Q93, Q94, Q95, Q96, Q97, Q98, Q99, Q100, Q101, Q102, Q103, Q104, Q105, Q106, Q107, Q108, Q109, Q110, Q111, Q112, Q113, Q114, Q115, Q116, Q117, Q118, Q119, Q120, Q121]), "radius" : 0.7 * mm, "tangentPropagation" : true, "defaultsChanged" : true, "vertexSettings" : [], "allowEdgeOverflow" : false});
        }
        {
            var Q0;
            Q0=makeQuery(id+"F7.boolean.opBoolean","INTERSECT",EDGE,{"disambiguationData":[OD(0.0)],"derivedFrom":[makeQuery(id+"F1.opExtrude","SWEPT_FACE",FACE,{"disambiguationData":[OSD([sQuery(id+"F0.wireOp",EDGE,"E0")])]}),makeQuery(id+"F7.opExtrude","SWEPT_FACE",FACE,{"disambiguationData":[OSD([sQuery(id+"F6.wireOp",EDGE,"57ad66dd-c389-404c-b97b-3d1c940e2ac9.0")])]})]});
            var Q1;
            Q1=makeQuery(id+"F7.boolean.opBoolean","INTERSECT",EDGE,{"disambiguationData":[OD(0.0)],"derivedFrom":[makeQuery(id+"F1.opExtrude","SWEPT_FACE",FACE,{"disambiguationData":[OSD([sQuery(id+"F0.wireOp",EDGE,"E0")])]}),makeQuery(id+"F7.opExtrude","SWEPT_FACE",FACE,{"disambiguationData":[OSD([sQuery(id+"F6.wireOp",EDGE,"57ad66dd-c389-404c-b97b-3d1c940e2ac9.5")])]})]});
            var Q2;
            Q2=makeQuery(id+"F7.boolean.opBoolean","INTERSECT",EDGE,{"disambiguationData":[OD(0.0)],"derivedFrom":[makeQuery(id+"F1.opExtrude","SWEPT_FACE",FACE,{"disambiguationData":[OSD([sQuery(id+"F0.wireOp",EDGE,"E0")])]}),makeQuery(id+"F7.opExtrude","SWEPT_FACE",FACE,{"disambiguationData":[OSD([sQuery(id+"F6.wireOp",EDGE,"57ad66dd-c389-404c-b97b-3d1c940e2ac9.4")])]})]});
            var Q3;
            Q3=makeQuery(id+"F7.boolean.opBoolean","INTERSECT",EDGE,{"disambiguationData":[OD(0.0)],"derivedFrom":[makeQuery(id+"F1.opExtrude","SWEPT_FACE",FACE,{"disambiguationData":[OSD([sQuery(id+"F0.wireOp",EDGE,"E0")])]}),makeQuery(id+"F7.opExtrude","SWEPT_FACE",FACE,{"disambiguationData":[OSD([sQuery(id+"F6.wireOp",EDGE,"57ad66dd-c389-404c-b97b-3d1c940e2ac9.3")])]})]});
            var Q4;
            Q4=makeQuery(id+"F7.boolean.opBoolean","INTERSECT",EDGE,{"disambiguationData":[OD(0.0)],"derivedFrom":[makeQuery(id+"F1.opExtrude","SWEPT_FACE",FACE,{"disambiguationData":[OSD([sQuery(id+"F0.wireOp",EDGE,"E0")])]}),makeQuery(id+"F7.opExtrude","SWEPT_FACE",FACE,{"disambiguationData":[OSD([sQuery(id+"F6.wireOp",EDGE,"57ad66dd-c389-404c-b97b-3d1c940e2ac9.2")])]})]});
            var Q5;
            Q5=makeQuery(id+"F7.boolean.opBoolean","INTERSECT",EDGE,{"disambiguationData":[OD(0.0)],"derivedFrom":[makeQuery(id+"F1.opExtrude","SWEPT_FACE",FACE,{"disambiguationData":[OSD([sQuery(id+"F0.wireOp",EDGE,"E0")])]}),makeQuery(id+"F7.opExtrude","SWEPT_FACE",FACE,{"disambiguationData":[OSD([sQuery(id+"F6.wireOp",EDGE,"57ad66dd-c389-404c-b97b-3d1c940e2ac9.1")])]})]});
            var Q6;
            Q6=makeQuery(id+"F7.boolean.opBoolean","INTERSECT",EDGE,{"disambiguationData":[OD(0.0)],"derivedFrom":[makeQuery(id+"F1.opExtrude","SWEPT_FACE",FACE,{"disambiguationData":[OSD([sQuery(id+"F0.wireOp",EDGE,"E0")])]}),makeQuery(id+"F7.opExtrude","SWEPT_FACE",FACE,{"disambiguationData":[OSD([sQuery(id+"F6.wireOp",EDGE,"b8bbc581-4b7c-4f09-85fb-0bc221e83278.2")])]})]});
            var Q7;
            Q7=makeQuery(id+"F7.boolean.opBoolean","INTERSECT",EDGE,{"disambiguationData":[OD(0.0)],"derivedFrom":[makeQuery(id+"F1.opExtrude","SWEPT_FACE",FACE,{"disambiguationData":[OSD([sQuery(id+"F0.wireOp",EDGE,"E0")])]}),makeQuery(id+"F7.opExtrude","SWEPT_FACE",FACE,{"disambiguationData":[OSD([sQuery(id+"F6.wireOp",EDGE,"b8bbc581-4b7c-4f09-85fb-0bc221e83278.1")])]})]});
            var Q8;
            Q8=makeQuery(id+"F7.boolean.opBoolean","INTERSECT",EDGE,{"disambiguationData":[OD(0.0)],"derivedFrom":[makeQuery(id+"F1.opExtrude","SWEPT_FACE",FACE,{"disambiguationData":[OSD([sQuery(id+"F0.wireOp",EDGE,"E0")])]}),makeQuery(id+"F7.opExtrude","SWEPT_FACE",FACE,{"disambiguationData":[OSD([sQuery(id+"F6.wireOp",EDGE,"b8bbc581-4b7c-4f09-85fb-0bc221e83278.0")])]})]});
            var Q9;
            Q9=makeQuery(id+"F7.boolean.opBoolean","INTERSECT",EDGE,{"disambiguationData":[OD(0.0)],"derivedFrom":[makeQuery(id+"F1.opExtrude","SWEPT_FACE",FACE,{"disambiguationData":[OSD([sQuery(id+"F0.wireOp",EDGE,"E0")])]}),makeQuery(id+"F7.opExtrude","SWEPT_FACE",FACE,{"disambiguationData":[OSD([sQuery(id+"F6.wireOp",EDGE,"b8bbc581-4b7c-4f09-85fb-0bc221e83278.5")])]})]});
            var Q10;
            Q10=makeQuery(id+"F7.boolean.opBoolean","INTERSECT",EDGE,{"disambiguationData":[OD(0.0)],"derivedFrom":[makeQuery(id+"F1.opExtrude","SWEPT_FACE",FACE,{"disambiguationData":[OSD([sQuery(id+"F0.wireOp",EDGE,"E0")])]}),makeQuery(id+"F7.opExtrude","SWEPT_FACE",FACE,{"disambiguationData":[OSD([sQuery(id+"F6.wireOp",EDGE,"b8bbc581-4b7c-4f09-85fb-0bc221e83278.4")])]})]});
            var Q11;
            Q11=makeQuery(id+"F7.boolean.opBoolean","INTERSECT",EDGE,{"disambiguationData":[OD(0.0)],"derivedFrom":[makeQuery(id+"F1.opExtrude","SWEPT_FACE",FACE,{"disambiguationData":[OSD([sQuery(id+"F0.wireOp",EDGE,"E0")])]}),makeQuery(id+"F7.opExtrude","SWEPT_FACE",FACE,{"disambiguationData":[OSD([sQuery(id+"F6.wireOp",EDGE,"b8bbc581-4b7c-4f09-85fb-0bc221e83278.3")])]})]});
            var Q12;
            Q12=makeQuery(id+"F7.boolean.opBoolean","INTERSECT",EDGE,{"disambiguationData":[OD(0.0)],"derivedFrom":[makeQuery(id+"F1.opExtrude","SWEPT_FACE",FACE,{"disambiguationData":[OSD([sQuery(id+"F0.wireOp",EDGE,"E0")])]}),makeQuery(id+"F7.opExtrude","SWEPT_FACE",FACE,{"disambiguationData":[OSD([sQuery(id+"F6.wireOp",EDGE,"3989a008-e829-4c74-847c-c0cff927c4a6.0")])]})]});
            var Q13;
            Q13=makeQuery(id+"F7.boolean.opBoolean","INTERSECT",EDGE,{"disambiguationData":[OD(0.0)],"derivedFrom":[makeQuery(id+"F1.opExtrude","SWEPT_FACE",FACE,{"disambiguationData":[OSD([sQuery(id+"F0.wireOp",EDGE,"E0")])]}),makeQuery(id+"F7.opExtrude","SWEPT_FACE",FACE,{"disambiguationData":[OSD([sQuery(id+"F6.wireOp",EDGE,"3989a008-e829-4c74-847c-c0cff927c4a6.5")])]})]});
            var Q14;
            Q14=makeQuery(id+"F7.boolean.opBoolean","INTERSECT",EDGE,{"disambiguationData":[OD(0.0)],"derivedFrom":[makeQuery(id+"F1.opExtrude","SWEPT_FACE",FACE,{"disambiguationData":[OSD([sQuery(id+"F0.wireOp",EDGE,"E0")])]}),makeQuery(id+"F7.opExtrude","SWEPT_FACE",FACE,{"disambiguationData":[OSD([sQuery(id+"F6.wireOp",EDGE,"3989a008-e829-4c74-847c-c0cff927c4a6.4")])]})]});
            var Q15;
            Q15=makeQuery(id+"F7.boolean.opBoolean","INTERSECT",EDGE,{"disambiguationData":[OD(0.0)],"derivedFrom":[makeQuery(id+"F1.opExtrude","SWEPT_FACE",FACE,{"disambiguationData":[OSD([sQuery(id+"F0.wireOp",EDGE,"E0")])]}),makeQuery(id+"F7.opExtrude","SWEPT_FACE",FACE,{"disambiguationData":[OSD([sQuery(id+"F6.wireOp",EDGE,"3989a008-e829-4c74-847c-c0cff927c4a6.3")])]})]});
            var Q16;
            Q16=makeQuery(id+"F7.boolean.opBoolean","INTERSECT",EDGE,{"disambiguationData":[OD(0.0)],"derivedFrom":[makeQuery(id+"F1.opExtrude","SWEPT_FACE",FACE,{"disambiguationData":[OSD([sQuery(id+"F0.wireOp",EDGE,"E0")])]}),makeQuery(id+"F7.opExtrude","SWEPT_FACE",FACE,{"disambiguationData":[OSD([sQuery(id+"F6.wireOp",EDGE,"3989a008-e829-4c74-847c-c0cff927c4a6.2")])]})]});
            var Q17;
            Q17=makeQuery(id+"F7.boolean.opBoolean","INTERSECT",EDGE,{"disambiguationData":[OD(0.0)],"derivedFrom":[makeQuery(id+"F1.opExtrude","SWEPT_FACE",FACE,{"disambiguationData":[OSD([sQuery(id+"F0.wireOp",EDGE,"E0")])]}),makeQuery(id+"F7.opExtrude","SWEPT_FACE",FACE,{"disambiguationData":[OSD([sQuery(id+"F6.wireOp",EDGE,"3989a008-e829-4c74-847c-c0cff927c4a6.1")])]})]});
            var Q18;
            Q18=makeQuery(id+"F7.boolean.opBoolean","INTERSECT",EDGE,{"disambiguationData":[OD(0.0)],"derivedFrom":[makeQuery(id+"F1.opExtrude","SWEPT_FACE",FACE,{"disambiguationData":[OSD([sQuery(id+"F0.wireOp",EDGE,"E0")])]}),makeQuery(id+"F7.opExtrude","SWEPT_FACE",FACE,{"disambiguationData":[OSD([sQuery(id+"F6.wireOp",EDGE,"86e64e75-ce93-4209-b98e-9b8fc518f516.2")])]})]});
            var Q19;
            Q19=makeQuery(id+"F7.boolean.opBoolean","INTERSECT",EDGE,{"disambiguationData":[OD(0.0)],"derivedFrom":[makeQuery(id+"F1.opExtrude","SWEPT_FACE",FACE,{"disambiguationData":[OSD([sQuery(id+"F0.wireOp",EDGE,"E0")])]}),makeQuery(id+"F7.opExtrude","SWEPT_FACE",FACE,{"disambiguationData":[OSD([sQuery(id+"F6.wireOp",EDGE,"86e64e75-ce93-4209-b98e-9b8fc518f516.1")])]})]});
            var Q20;
            Q20=makeQuery(id+"F7.boolean.opBoolean","INTERSECT",EDGE,{"disambiguationData":[OD(0.0)],"derivedFrom":[makeQuery(id+"F1.opExtrude","SWEPT_FACE",FACE,{"disambiguationData":[OSD([sQuery(id+"F0.wireOp",EDGE,"E0")])]}),makeQuery(id+"F7.opExtrude","SWEPT_FACE",FACE,{"disambiguationData":[OSD([sQuery(id+"F6.wireOp",EDGE,"86e64e75-ce93-4209-b98e-9b8fc518f516.0")])]})]});
            var Q21;
            Q21=makeQuery(id+"F7.boolean.opBoolean","INTERSECT",EDGE,{"disambiguationData":[OD(0.0)],"derivedFrom":[makeQuery(id+"F1.opExtrude","SWEPT_FACE",FACE,{"disambiguationData":[OSD([sQuery(id+"F0.wireOp",EDGE,"E0")])]}),makeQuery(id+"F7.opExtrude","SWEPT_FACE",FACE,{"disambiguationData":[OSD([sQuery(id+"F6.wireOp",EDGE,"86e64e75-ce93-4209-b98e-9b8fc518f516.5")])]})]});
            var Q22;
            Q22=makeQuery(id+"F7.boolean.opBoolean","INTERSECT",EDGE,{"disambiguationData":[OD(0.0)],"derivedFrom":[makeQuery(id+"F1.opExtrude","SWEPT_FACE",FACE,{"disambiguationData":[OSD([sQuery(id+"F0.wireOp",EDGE,"E0")])]}),makeQuery(id+"F7.opExtrude","SWEPT_FACE",FACE,{"disambiguationData":[OSD([sQuery(id+"F6.wireOp",EDGE,"86e64e75-ce93-4209-b98e-9b8fc518f516.4")])]})]});
            var Q23;
            Q23=makeQuery(id+"F7.boolean.opBoolean","INTERSECT",EDGE,{"disambiguationData":[OD(0.0)],"derivedFrom":[makeQuery(id+"F1.opExtrude","SWEPT_FACE",FACE,{"disambiguationData":[OSD([sQuery(id+"F0.wireOp",EDGE,"E0")])]}),makeQuery(id+"F7.opExtrude","SWEPT_FACE",FACE,{"disambiguationData":[OSD([sQuery(id+"F6.wireOp",EDGE,"86e64e75-ce93-4209-b98e-9b8fc518f516.3")])]})]});
            var Q24;
            Q24=makeQuery(id+"F7.boolean.opBoolean","INTERSECT",EDGE,{"disambiguationData":[OD(0.0)],"derivedFrom":[makeQuery(id+"F1.opExtrude","SWEPT_FACE",FACE,{"disambiguationData":[OSD([sQuery(id+"F0.wireOp",EDGE,"E0")])]}),makeQuery(id+"F7.opExtrude","SWEPT_FACE",FACE,{"disambiguationData":[OSD([sQuery(id+"F6.wireOp",EDGE,"09c30c40-169e-4e38-bf91-241d7524808d.0")])]})]});
            var Q25;
            Q25=makeQuery(id+"F7.boolean.opBoolean","INTERSECT",EDGE,{"disambiguationData":[OD(0.0)],"derivedFrom":[makeQuery(id+"F1.opExtrude","SWEPT_FACE",FACE,{"disambiguationData":[OSD([sQuery(id+"F0.wireOp",EDGE,"E0")])]}),makeQuery(id+"F7.opExtrude","SWEPT_FACE",FACE,{"disambiguationData":[OSD([sQuery(id+"F6.wireOp",EDGE,"09c30c40-169e-4e38-bf91-241d7524808d.4")])]})]});
            var Q26;
            Q26=makeQuery(id+"F7.boolean.opBoolean","INTERSECT",EDGE,{"disambiguationData":[OD(0.0)],"derivedFrom":[makeQuery(id+"F1.opExtrude","SWEPT_FACE",FACE,{"disambiguationData":[OSD([sQuery(id+"F0.wireOp",EDGE,"E0")])]}),makeQuery(id+"F7.opExtrude","SWEPT_FACE",FACE,{"disambiguationData":[OSD([sQuery(id+"F6.wireOp",EDGE,"09c30c40-169e-4e38-bf91-241d7524808d.3")])]})]});
            var Q27;
            Q27=makeQuery(id+"F7.boolean.opBoolean","INTERSECT",EDGE,{"disambiguationData":[OD(0.0)],"derivedFrom":[makeQuery(id+"F1.opExtrude","SWEPT_FACE",FACE,{"disambiguationData":[OSD([sQuery(id+"F0.wireOp",EDGE,"E0")])]}),makeQuery(id+"F7.opExtrude","SWEPT_FACE",FACE,{"disambiguationData":[OSD([sQuery(id+"F6.wireOp",EDGE,"09c30c40-169e-4e38-bf91-241d7524808d.2")])]})]});
            var Q28;
            Q28=makeQuery(id+"F7.boolean.opBoolean","INTERSECT",EDGE,{"disambiguationData":[OD(0.0)],"derivedFrom":[makeQuery(id+"F1.opExtrude","SWEPT_FACE",FACE,{"disambiguationData":[OSD([sQuery(id+"F0.wireOp",EDGE,"E0")])]}),makeQuery(id+"F7.opExtrude","SWEPT_FACE",FACE,{"disambiguationData":[OSD([sQuery(id+"F6.wireOp",EDGE,"09c30c40-169e-4e38-bf91-241d7524808d.1")])]})]});
            var Q29;
            Q29=makeQuery(id+"F7.boolean.opBoolean","INTERSECT",EDGE,{"disambiguationData":[OD(0.0)],"derivedFrom":[makeQuery(id+"F1.opExtrude","SWEPT_FACE",FACE,{"disambiguationData":[OSD([sQuery(id+"F0.wireOp",EDGE,"E0")])]}),makeQuery(id+"F7.opExtrude","SWEPT_FACE",FACE,{"disambiguationData":[OSD([sQuery(id+"F6.wireOp",EDGE,"cfdfa16a-de7a-4601-9022-5211aa514822.2")])]})]});
            var Q30;
            Q30=makeQuery(id+"F7.boolean.opBoolean","INTERSECT",EDGE,{"disambiguationData":[OD(0.0)],"derivedFrom":[makeQuery(id+"F1.opExtrude","SWEPT_FACE",FACE,{"disambiguationData":[OSD([sQuery(id+"F0.wireOp",EDGE,"E0")])]}),makeQuery(id+"F7.opExtrude","SWEPT_FACE",FACE,{"disambiguationData":[OSD([sQuery(id+"F6.wireOp",EDGE,"cfdfa16a-de7a-4601-9022-5211aa514822.1")])]})]});
            var Q31;
            Q31=makeQuery(id+"F7.boolean.opBoolean","INTERSECT",EDGE,{"disambiguationData":[OD(0.0)],"derivedFrom":[makeQuery(id+"F1.opExtrude","SWEPT_FACE",FACE,{"disambiguationData":[OSD([sQuery(id+"F0.wireOp",EDGE,"E0")])]}),makeQuery(id+"F7.opExtrude","SWEPT_FACE",FACE,{"disambiguationData":[OSD([sQuery(id+"F6.wireOp",EDGE,"cfdfa16a-de7a-4601-9022-5211aa514822.0")])]})]});
            var Q32;
            Q32=makeQuery(id+"F7.boolean.opBoolean","INTERSECT",EDGE,{"disambiguationData":[OD(0.0)],"derivedFrom":[makeQuery(id+"F1.opExtrude","SWEPT_FACE",FACE,{"disambiguationData":[OSD([sQuery(id+"F0.wireOp",EDGE,"E0")])]}),makeQuery(id+"F7.opExtrude","SWEPT_FACE",FACE,{"disambiguationData":[OSD([sQuery(id+"F6.wireOp",EDGE,"cfdfa16a-de7a-4601-9022-5211aa514822.5")])]})]});
            var Q33;
            Q33=makeQuery(id+"F7.boolean.opBoolean","INTERSECT",EDGE,{"disambiguationData":[OD(0.0)],"derivedFrom":[makeQuery(id+"F1.opExtrude","SWEPT_FACE",FACE,{"disambiguationData":[OSD([sQuery(id+"F0.wireOp",EDGE,"E0")])]}),makeQuery(id+"F7.opExtrude","SWEPT_FACE",FACE,{"disambiguationData":[OSD([sQuery(id+"F6.wireOp",EDGE,"cfdfa16a-de7a-4601-9022-5211aa514822.3")])]})]});
            var Q34;
            Q34=makeQuery(id+"F5.boolean.opBoolean","INTERSECT",EDGE,{"disambiguationData":[OD(1.0)],"derivedFrom":[makeQuery(id+"F1.opExtrude","SWEPT_FACE",FACE,{"disambiguationData":[OSD([sQuery(id+"F0.wireOp",EDGE,"E0")])]}),makeQuery(id+"F5.opExtrude","SWEPT_FACE",FACE,{"disambiguationData":[OSD([sQuery(id+"F4.wireOp",EDGE,"E4.3")])]})]});
            var Q35;
            Q35=makeQuery(id+"F5.boolean.opBoolean","INTERSECT",EDGE,{"disambiguationData":[OD(1.0)],"derivedFrom":[makeQuery(id+"F1.opExtrude","SWEPT_FACE",FACE,{"disambiguationData":[OSD([sQuery(id+"F0.wireOp",EDGE,"E0")])]}),makeQuery(id+"F5.opExtrude","SWEPT_FACE",FACE,{"disambiguationData":[OSD([sQuery(id+"F4.wireOp",EDGE,"E4.4")])]})]});
            var Q36;
            Q36=makeQuery(id+"F5.boolean.opBoolean","INTERSECT",EDGE,{"disambiguationData":[OD(1.0)],"derivedFrom":[makeQuery(id+"F1.opExtrude","SWEPT_FACE",FACE,{"disambiguationData":[OSD([sQuery(id+"F0.wireOp",EDGE,"E0")])]}),makeQuery(id+"F5.opExtrude","SWEPT_FACE",FACE,{"disambiguationData":[OSD([sQuery(id+"F4.wireOp",EDGE,"E4.5")])]})]});
            var Q37;
            Q37=makeQuery(id+"F5.boolean.opBoolean","INTERSECT",EDGE,{"disambiguationData":[OD(1.0)],"derivedFrom":[makeQuery(id+"F1.opExtrude","SWEPT_FACE",FACE,{"disambiguationData":[OSD([sQuery(id+"F0.wireOp",EDGE,"E0")])]}),makeQuery(id+"F5.opExtrude","SWEPT_FACE",FACE,{"disambiguationData":[OSD([sQuery(id+"F4.wireOp",EDGE,"E4.0")])]})]});
            var Q38;
            Q38=makeQuery(id+"F5.boolean.opBoolean","INTERSECT",EDGE,{"disambiguationData":[OD(1.0)],"derivedFrom":[makeQuery(id+"F1.opExtrude","SWEPT_FACE",FACE,{"disambiguationData":[OSD([sQuery(id+"F0.wireOp",EDGE,"E0")])]}),makeQuery(id+"F5.opExtrude","SWEPT_FACE",FACE,{"disambiguationData":[OSD([sQuery(id+"F4.wireOp",EDGE,"E4.1")])]})]});
            var Q39;
            Q39=makeQuery(id+"F5.boolean.opBoolean","INTERSECT",EDGE,{"disambiguationData":[OD(1.0)],"derivedFrom":[makeQuery(id+"F1.opExtrude","SWEPT_FACE",FACE,{"disambiguationData":[OSD([sQuery(id+"F0.wireOp",EDGE,"E0")])]}),makeQuery(id+"F5.opExtrude","SWEPT_FACE",FACE,{"disambiguationData":[OSD([sQuery(id+"F4.wireOp",EDGE,"E4.2")])]})]});
            var Q40;
            Q40=makeQuery(id+"F5.boolean.opBoolean","INTERSECT",EDGE,{"disambiguationData":[OD(1.0)],"derivedFrom":[makeQuery(id+"F1.opExtrude","SWEPT_FACE",FACE,{"disambiguationData":[OSD([sQuery(id+"F0.wireOp",EDGE,"E0")])]}),makeQuery(id+"F5.opExtrude","SWEPT_FACE",FACE,{"disambiguationData":[OSD([sQuery(id+"F4.wireOp",EDGE,"E5.0.1.1")])]})]});
            var Q41;
            Q41=makeQuery(id+"F5.boolean.opBoolean","INTERSECT",EDGE,{"disambiguationData":[OD(1.0)],"derivedFrom":[makeQuery(id+"F1.opExtrude","SWEPT_FACE",FACE,{"disambiguationData":[OSD([sQuery(id+"F0.wireOp",EDGE,"E0")])]}),makeQuery(id+"F5.opExtrude","SWEPT_FACE",FACE,{"disambiguationData":[OSD([sQuery(id+"F4.wireOp",EDGE,"E5.0.1.7")])]})]});
            var Q42;
            Q42=makeQuery(id+"F5.boolean.opBoolean","INTERSECT",EDGE,{"disambiguationData":[OD(1.0)],"derivedFrom":[makeQuery(id+"F1.opExtrude","SWEPT_FACE",FACE,{"disambiguationData":[OSD([sQuery(id+"F0.wireOp",EDGE,"E0")])]}),makeQuery(id+"F5.opExtrude","SWEPT_FACE",FACE,{"disambiguationData":[OSD([sQuery(id+"F4.wireOp",EDGE,"E5.0.1.0")])]})]});
            var Q43;
            Q43=makeQuery(id+"F5.boolean.opBoolean","INTERSECT",EDGE,{"disambiguationData":[OD(1.0)],"derivedFrom":[makeQuery(id+"F1.opExtrude","SWEPT_FACE",FACE,{"disambiguationData":[OSD([sQuery(id+"F0.wireOp",EDGE,"E0")])]}),makeQuery(id+"F5.opExtrude","SWEPT_FACE",FACE,{"disambiguationData":[OSD([sQuery(id+"F4.wireOp",EDGE,"E5.0.1.4")])]})]});
            var Q44;
            Q44=makeQuery(id+"F5.boolean.opBoolean","INTERSECT",EDGE,{"disambiguationData":[OD(1.0)],"derivedFrom":[makeQuery(id+"F1.opExtrude","SWEPT_FACE",FACE,{"disambiguationData":[OSD([sQuery(id+"F0.wireOp",EDGE,"E0")])]}),makeQuery(id+"F5.opExtrude","SWEPT_FACE",FACE,{"disambiguationData":[OSD([sQuery(id+"F4.wireOp",EDGE,"E5.0.1.3")])]})]});
            var Q45;
            Q45=makeQuery(id+"F5.boolean.opBoolean","INTERSECT",EDGE,{"disambiguationData":[OD(1.0)],"derivedFrom":[makeQuery(id+"F1.opExtrude","SWEPT_FACE",FACE,{"disambiguationData":[OSD([sQuery(id+"F0.wireOp",EDGE,"E0")])]}),makeQuery(id+"F5.opExtrude","SWEPT_FACE",FACE,{"disambiguationData":[OSD([sQuery(id+"F4.wireOp",EDGE,"E5.0.1.2")])]})]});
            var Q46;
            Q46=makeQuery(id+"F5.boolean.opBoolean","INTERSECT",EDGE,{"disambiguationData":[OD(1.0)],"derivedFrom":[makeQuery(id+"F1.opExtrude","SWEPT_FACE",FACE,{"disambiguationData":[OSD([sQuery(id+"F0.wireOp",EDGE,"E0")])]}),makeQuery(id+"F5.opExtrude","SWEPT_FACE",FACE,{"disambiguationData":[OSD([sQuery(id+"F4.wireOp",EDGE,"E5.0.2.1")])]})]});
            var Q47;
            Q47=makeQuery(id+"F5.boolean.opBoolean","INTERSECT",EDGE,{"disambiguationData":[OD(1.0)],"derivedFrom":[makeQuery(id+"F1.opExtrude","SWEPT_FACE",FACE,{"disambiguationData":[OSD([sQuery(id+"F0.wireOp",EDGE,"E0")])]}),makeQuery(id+"F5.opExtrude","SWEPT_FACE",FACE,{"disambiguationData":[OSD([sQuery(id+"F4.wireOp",EDGE,"E5.0.2.7")])]})]});
            var Q48;
            Q48=makeQuery(id+"F5.boolean.opBoolean","INTERSECT",EDGE,{"disambiguationData":[OD(1.0)],"derivedFrom":[makeQuery(id+"F1.opExtrude","SWEPT_FACE",FACE,{"disambiguationData":[OSD([sQuery(id+"F0.wireOp",EDGE,"E0")])]}),makeQuery(id+"F5.opExtrude","SWEPT_FACE",FACE,{"disambiguationData":[OSD([sQuery(id+"F4.wireOp",EDGE,"E5.0.2.0")])]})]});
            var Q49;
            Q49=makeQuery(id+"F5.boolean.opBoolean","INTERSECT",EDGE,{"disambiguationData":[OD(1.0)],"derivedFrom":[makeQuery(id+"F1.opExtrude","SWEPT_FACE",FACE,{"disambiguationData":[OSD([sQuery(id+"F0.wireOp",EDGE,"E0")])]}),makeQuery(id+"F5.opExtrude","SWEPT_FACE",FACE,{"disambiguationData":[OSD([sQuery(id+"F4.wireOp",EDGE,"E5.0.2.4")])]})]});
            var Q50;
            Q50=makeQuery(id+"F5.boolean.opBoolean","INTERSECT",EDGE,{"disambiguationData":[OD(1.0)],"derivedFrom":[makeQuery(id+"F1.opExtrude","SWEPT_FACE",FACE,{"disambiguationData":[OSD([sQuery(id+"F0.wireOp",EDGE,"E0")])]}),makeQuery(id+"F5.opExtrude","SWEPT_FACE",FACE,{"disambiguationData":[OSD([sQuery(id+"F4.wireOp",EDGE,"E5.0.2.3")])]})]});
            var Q51;
            Q51=makeQuery(id+"F5.boolean.opBoolean","INTERSECT",EDGE,{"disambiguationData":[OD(1.0)],"derivedFrom":[makeQuery(id+"F1.opExtrude","SWEPT_FACE",FACE,{"disambiguationData":[OSD([sQuery(id+"F0.wireOp",EDGE,"E0")])]}),makeQuery(id+"F5.opExtrude","SWEPT_FACE",FACE,{"disambiguationData":[OSD([sQuery(id+"F4.wireOp",EDGE,"E5.0.2.2")])]})]});
            var Q52;
            Q52=makeQuery(id+"F5.boolean.opBoolean","INTERSECT",EDGE,{"disambiguationData":[OD(1.0)],"derivedFrom":[makeQuery(id+"F1.opExtrude","SWEPT_FACE",FACE,{"disambiguationData":[OSD([sQuery(id+"F0.wireOp",EDGE,"E0")])]}),makeQuery(id+"F5.opExtrude","SWEPT_FACE",FACE,{"disambiguationData":[OSD([sQuery(id+"F4.wireOp",EDGE,"E5.0.3.1")])]})]});
            var Q53;
            Q53=makeQuery(id+"F5.boolean.opBoolean","INTERSECT",EDGE,{"disambiguationData":[OD(1.0)],"derivedFrom":[makeQuery(id+"F1.opExtrude","SWEPT_FACE",FACE,{"disambiguationData":[OSD([sQuery(id+"F0.wireOp",EDGE,"E0")])]}),makeQuery(id+"F5.opExtrude","SWEPT_FACE",FACE,{"disambiguationData":[OSD([sQuery(id+"F4.wireOp",EDGE,"E5.0.3.7")])]})]});
            var Q54;
            Q54=makeQuery(id+"F5.boolean.opBoolean","INTERSECT",EDGE,{"disambiguationData":[OD(1.0)],"derivedFrom":[makeQuery(id+"F1.opExtrude","SWEPT_FACE",FACE,{"disambiguationData":[OSD([sQuery(id+"F0.wireOp",EDGE,"E0")])]}),makeQuery(id+"F5.opExtrude","SWEPT_FACE",FACE,{"disambiguationData":[OSD([sQuery(id+"F4.wireOp",EDGE,"E5.0.3.0")])]})]});
            var Q55;
            Q55=makeQuery(id+"F5.boolean.opBoolean","INTERSECT",EDGE,{"disambiguationData":[OD(1.0)],"derivedFrom":[makeQuery(id+"F1.opExtrude","SWEPT_FACE",FACE,{"disambiguationData":[OSD([sQuery(id+"F0.wireOp",EDGE,"E0")])]}),makeQuery(id+"F5.opExtrude","SWEPT_FACE",FACE,{"disambiguationData":[OSD([sQuery(id+"F4.wireOp",EDGE,"E5.0.3.4")])]})]});
            var Q56;
            Q56=makeQuery(id+"F5.boolean.opBoolean","INTERSECT",EDGE,{"disambiguationData":[OD(1.0)],"derivedFrom":[makeQuery(id+"F1.opExtrude","SWEPT_FACE",FACE,{"disambiguationData":[OSD([sQuery(id+"F0.wireOp",EDGE,"E0")])]}),makeQuery(id+"F5.opExtrude","SWEPT_FACE",FACE,{"disambiguationData":[OSD([sQuery(id+"F4.wireOp",EDGE,"E5.0.3.3")])]})]});
            var Q57;
            Q57=makeQuery(id+"F5.boolean.opBoolean","INTERSECT",EDGE,{"disambiguationData":[OD(1.0)],"derivedFrom":[makeQuery(id+"F1.opExtrude","SWEPT_FACE",FACE,{"disambiguationData":[OSD([sQuery(id+"F0.wireOp",EDGE,"E0")])]}),makeQuery(id+"F5.opExtrude","SWEPT_FACE",FACE,{"disambiguationData":[OSD([sQuery(id+"F4.wireOp",EDGE,"E5.0.3.2")])]})]});
            var Q58;
            Q58=makeQuery(id+"F5.boolean.opBoolean","INTERSECT",EDGE,{"disambiguationData":[OD(1.0)],"derivedFrom":[makeQuery(id+"F1.opExtrude","SWEPT_FACE",FACE,{"disambiguationData":[OSD([sQuery(id+"F0.wireOp",EDGE,"E0")])]}),makeQuery(id+"F5.opExtrude","SWEPT_FACE",FACE,{"disambiguationData":[OSD([sQuery(id+"F4.wireOp",EDGE,"E5.0.4.1")])]})]});
            var Q59;
            Q59=makeQuery(id+"F5.boolean.opBoolean","INTERSECT",EDGE,{"disambiguationData":[OD(1.0)],"derivedFrom":[makeQuery(id+"F1.opExtrude","SWEPT_FACE",FACE,{"disambiguationData":[OSD([sQuery(id+"F0.wireOp",EDGE,"E0")])]}),makeQuery(id+"F5.opExtrude","SWEPT_FACE",FACE,{"disambiguationData":[OSD([sQuery(id+"F4.wireOp",EDGE,"E5.0.4.7")])]})]});
            var Q60;
            Q60=makeQuery(id+"F5.boolean.opBoolean","INTERSECT",EDGE,{"disambiguationData":[OD(1.0)],"derivedFrom":[makeQuery(id+"F1.opExtrude","SWEPT_FACE",FACE,{"disambiguationData":[OSD([sQuery(id+"F0.wireOp",EDGE,"E0")])]}),makeQuery(id+"F5.opExtrude","SWEPT_FACE",FACE,{"disambiguationData":[OSD([sQuery(id+"F4.wireOp",EDGE,"E5.0.4.0")])]})]});
            var Q61;
            Q61=makeQuery(id+"F5.boolean.opBoolean","INTERSECT",EDGE,{"disambiguationData":[OD(1.0)],"derivedFrom":[makeQuery(id+"F1.opExtrude","SWEPT_FACE",FACE,{"disambiguationData":[OSD([sQuery(id+"F0.wireOp",EDGE,"E0")])]}),makeQuery(id+"F5.opExtrude","SWEPT_FACE",FACE,{"disambiguationData":[OSD([sQuery(id+"F4.wireOp",EDGE,"E5.0.4.4")])]})]});
            var Q62;
            Q62=makeQuery(id+"F5.boolean.opBoolean","INTERSECT",EDGE,{"disambiguationData":[OD(1.0)],"derivedFrom":[makeQuery(id+"F1.opExtrude","SWEPT_FACE",FACE,{"disambiguationData":[OSD([sQuery(id+"F0.wireOp",EDGE,"E0")])]}),makeQuery(id+"F5.opExtrude","SWEPT_FACE",FACE,{"disambiguationData":[OSD([sQuery(id+"F4.wireOp",EDGE,"E5.0.4.3")])]})]});
            var Q63;
            Q63=makeQuery(id+"F5.boolean.opBoolean","INTERSECT",EDGE,{"disambiguationData":[OD(1.0)],"derivedFrom":[makeQuery(id+"F1.opExtrude","SWEPT_FACE",FACE,{"disambiguationData":[OSD([sQuery(id+"F0.wireOp",EDGE,"E0")])]}),makeQuery(id+"F5.opExtrude","SWEPT_FACE",FACE,{"disambiguationData":[OSD([sQuery(id+"F4.wireOp",EDGE,"E5.0.4.2")])]})]});
            var Q64;
            Q64=makeQuery(id+"F5.boolean.opBoolean","INTERSECT",EDGE,{"disambiguationData":[OD(1.0)],"derivedFrom":[makeQuery(id+"F1.opExtrude","SWEPT_FACE",FACE,{"disambiguationData":[OSD([sQuery(id+"F0.wireOp",EDGE,"E0")])]}),makeQuery(id+"F5.opExtrude","SWEPT_FACE",FACE,{"disambiguationData":[OSD([sQuery(id+"F4.wireOp",EDGE,"E5.0.5.1")])]})]});
            var Q65;
            Q65=makeQuery(id+"F5.boolean.opBoolean","INTERSECT",EDGE,{"disambiguationData":[OD(1.0)],"derivedFrom":[makeQuery(id+"F1.opExtrude","SWEPT_FACE",FACE,{"disambiguationData":[OSD([sQuery(id+"F0.wireOp",EDGE,"E0")])]}),makeQuery(id+"F5.opExtrude","SWEPT_FACE",FACE,{"disambiguationData":[OSD([sQuery(id+"F4.wireOp",EDGE,"E5.0.5.7")])]})]});
            var Q66;
            Q66=makeQuery(id+"F5.boolean.opBoolean","INTERSECT",EDGE,{"disambiguationData":[OD(1.0)],"derivedFrom":[makeQuery(id+"F1.opExtrude","SWEPT_FACE",FACE,{"disambiguationData":[OSD([sQuery(id+"F0.wireOp",EDGE,"E0")])]}),makeQuery(id+"F5.opExtrude","SWEPT_FACE",FACE,{"disambiguationData":[OSD([sQuery(id+"F4.wireOp",EDGE,"E5.0.5.0")])]})]});
            var Q67;
            Q67=makeQuery(id+"F5.boolean.opBoolean","INTERSECT",EDGE,{"disambiguationData":[OD(1.0)],"derivedFrom":[makeQuery(id+"F1.opExtrude","SWEPT_FACE",FACE,{"disambiguationData":[OSD([sQuery(id+"F0.wireOp",EDGE,"E0")])]}),makeQuery(id+"F5.opExtrude","SWEPT_FACE",FACE,{"disambiguationData":[OSD([sQuery(id+"F4.wireOp",EDGE,"E5.0.5.4")])]})]});
            var Q68;
            Q68=makeQuery(id+"F5.boolean.opBoolean","INTERSECT",EDGE,{"disambiguationData":[OD(1.0)],"derivedFrom":[makeQuery(id+"F1.opExtrude","SWEPT_FACE",FACE,{"disambiguationData":[OSD([sQuery(id+"F0.wireOp",EDGE,"E0")])]}),makeQuery(id+"F5.opExtrude","SWEPT_FACE",FACE,{"disambiguationData":[OSD([sQuery(id+"F4.wireOp",EDGE,"E5.0.5.3")])]})]});
            var Q69;
            Q69=makeQuery(id+"F5.boolean.opBoolean","INTERSECT",EDGE,{"disambiguationData":[OD(1.0)],"derivedFrom":[makeQuery(id+"F1.opExtrude","SWEPT_FACE",FACE,{"disambiguationData":[OSD([sQuery(id+"F0.wireOp",EDGE,"E0")])]}),makeQuery(id+"F5.opExtrude","SWEPT_FACE",FACE,{"disambiguationData":[OSD([sQuery(id+"F4.wireOp",EDGE,"E5.0.5.2")])]})]});
            var Q70;
            Q70=makeQuery(id+"F5.boolean.opBoolean","INTERSECT",EDGE,{"disambiguationData":[OD(1.0)],"derivedFrom":[makeQuery(id+"F1.opExtrude","SWEPT_FACE",FACE,{"disambiguationData":[OSD([sQuery(id+"F0.wireOp",EDGE,"E0")])]}),makeQuery(id+"F5.opExtrude","SWEPT_FACE",FACE,{"disambiguationData":[OSD([sQuery(id+"F4.wireOp",EDGE,"E5.0.6.1")])]})]});
            var Q71;
            Q71=makeQuery(id+"F5.boolean.opBoolean","INTERSECT",EDGE,{"disambiguationData":[OD(1.0)],"derivedFrom":[makeQuery(id+"F1.opExtrude","SWEPT_FACE",FACE,{"disambiguationData":[OSD([sQuery(id+"F0.wireOp",EDGE,"E0")])]}),makeQuery(id+"F5.opExtrude","SWEPT_FACE",FACE,{"disambiguationData":[OSD([sQuery(id+"F4.wireOp",EDGE,"E5.0.6.7")])]})]});
            var Q72;
            Q72=makeQuery(id+"F5.boolean.opBoolean","INTERSECT",EDGE,{"disambiguationData":[OD(1.0)],"derivedFrom":[makeQuery(id+"F1.opExtrude","SWEPT_FACE",FACE,{"disambiguationData":[OSD([sQuery(id+"F0.wireOp",EDGE,"E0")])]}),makeQuery(id+"F5.opExtrude","SWEPT_FACE",FACE,{"disambiguationData":[OSD([sQuery(id+"F4.wireOp",EDGE,"E5.0.6.0")])]})]});
            var Q73;
            Q73=makeQuery(id+"F5.boolean.opBoolean","INTERSECT",EDGE,{"disambiguationData":[OD(1.0)],"derivedFrom":[makeQuery(id+"F1.opExtrude","SWEPT_FACE",FACE,{"disambiguationData":[OSD([sQuery(id+"F0.wireOp",EDGE,"E0")])]}),makeQuery(id+"F5.opExtrude","SWEPT_FACE",FACE,{"disambiguationData":[OSD([sQuery(id+"F4.wireOp",EDGE,"E5.0.6.4")])]})]});
            var Q74;
            Q74=makeQuery(id+"F5.boolean.opBoolean","INTERSECT",EDGE,{"disambiguationData":[OD(1.0)],"derivedFrom":[makeQuery(id+"F1.opExtrude","SWEPT_FACE",FACE,{"disambiguationData":[OSD([sQuery(id+"F0.wireOp",EDGE,"E0")])]}),makeQuery(id+"F5.opExtrude","SWEPT_FACE",FACE,{"disambiguationData":[OSD([sQuery(id+"F4.wireOp",EDGE,"E5.0.6.3")])]})]});
            var Q75;
            Q75=makeQuery(id+"F5.boolean.opBoolean","INTERSECT",EDGE,{"disambiguationData":[OD(1.0)],"derivedFrom":[makeQuery(id+"F1.opExtrude","SWEPT_FACE",FACE,{"disambiguationData":[OSD([sQuery(id+"F0.wireOp",EDGE,"E0")])]}),makeQuery(id+"F5.opExtrude","SWEPT_FACE",FACE,{"disambiguationData":[OSD([sQuery(id+"F4.wireOp",EDGE,"E5.0.6.2")])]})]});
            fillet(context, id + "F16", {"entities" : qUnion([Q0, Q1, Q2, Q3, Q4, Q5, Q6, Q7, Q8, Q9, Q10, Q11, Q12, Q13, Q14, Q15, Q16, Q17, Q18, Q19, Q20, Q21, Q22, Q23, Q24, Q25, Q26, Q27, Q28, Q29, Q30, Q31, Q32, Q33, Q34, Q35, Q36, Q37, Q38, Q39, Q40, Q41, Q42, Q43, Q44, Q45, Q46, Q47, Q48, Q49, Q50, Q51, Q52, Q53, Q54, Q55, Q56, Q57, Q58, Q59, Q60, Q61, Q62, Q63, Q64, Q65, Q66, Q67, Q68, Q69, Q70, Q71, Q72, Q73, Q74, Q75]), "radius" : 0.7 * mm, "tangentPropagation" : true, "defaultsChanged" : true, "vertexSettings" : [], "allowEdgeOverflow" : false});
        }
        {
            var Q0;
            Q0=makeQuery(id+"F7.boolean.opBoolean","INTERSECT",EDGE,{"disambiguationData":[OD(0.0)],"derivedFrom":[makeQuery(id+"F1.opExtrude","SWEPT_FACE",FACE,{"disambiguationData":[OSD([sQuery(id+"F0.wireOp",EDGE,"E0")])]}),makeQuery(id+"F7.opExtrude","SWEPT_FACE",FACE,{"disambiguationData":[OSD([sQuery(id+"F6.wireOp",EDGE,"E11.2")])]})]});
            var Q1;
            Q1=makeQuery(id+"F7.boolean.opBoolean","INTERSECT",EDGE,{"disambiguationData":[OD(0.0)],"derivedFrom":[makeQuery(id+"F1.opExtrude","SWEPT_FACE",FACE,{"disambiguationData":[OSD([sQuery(id+"F0.wireOp",EDGE,"E0")])]}),makeQuery(id+"F7.opExtrude","SWEPT_FACE",FACE,{"disambiguationData":[OSD([sQuery(id+"F6.wireOp",EDGE,"E11.1")])]})]});
            var Q2;
            Q2=makeQuery(id+"F7.boolean.opBoolean","INTERSECT",EDGE,{"disambiguationData":[OD(0.0)],"derivedFrom":[makeQuery(id+"F1.opExtrude","SWEPT_FACE",FACE,{"disambiguationData":[OSD([sQuery(id+"F0.wireOp",EDGE,"E0")])]}),makeQuery(id+"F7.opExtrude","SWEPT_FACE",FACE,{"disambiguationData":[OSD([sQuery(id+"F6.wireOp",EDGE,"E11.0")])]})]});
            var Q3;
            Q3=makeQuery(id+"F7.boolean.opBoolean","INTERSECT",EDGE,{"disambiguationData":[OD(0.0)],"derivedFrom":[makeQuery(id+"F1.opExtrude","SWEPT_FACE",FACE,{"disambiguationData":[OSD([sQuery(id+"F0.wireOp",EDGE,"E0")])]}),makeQuery(id+"F7.opExtrude","SWEPT_FACE",FACE,{"disambiguationData":[OSD([sQuery(id+"F6.wireOp",EDGE,"E8.4")])]})]});
            var Q4;
            Q4=makeQuery(id+"F7.boolean.opBoolean","INTERSECT",EDGE,{"disambiguationData":[OD(0.0)],"derivedFrom":[makeQuery(id+"F1.opExtrude","SWEPT_FACE",FACE,{"disambiguationData":[OSD([sQuery(id+"F0.wireOp",EDGE,"E0")])]}),makeQuery(id+"F7.opExtrude","SWEPT_FACE",FACE,{"disambiguationData":[OSD([sQuery(id+"F6.wireOp",EDGE,"E8.3")])]})]});
            var Q5;
            Q5=makeQuery(id+"F7.boolean.opBoolean","INTERSECT",EDGE,{"disambiguationData":[OD(0.0)],"derivedFrom":[makeQuery(id+"F1.opExtrude","SWEPT_FACE",FACE,{"disambiguationData":[OSD([sQuery(id+"F0.wireOp",EDGE,"E0")])]}),makeQuery(id+"F7.opExtrude","SWEPT_FACE",FACE,{"disambiguationData":[OSD([sQuery(id+"F6.wireOp",EDGE,"E8.2")])]})]});
            var Q6;
            Q6=makeQuery(id+"F10.boolean.opBoolean","INTERSECT",EDGE,{"disambiguationData":[OD(0.0)],"derivedFrom":[makeQuery(id+"F1.opExtrude","SWEPT_FACE",FACE,{"disambiguationData":[OSD([sQuery(id+"F0.wireOp",EDGE,"E0")])]}),makeQuery(id+"F10.opExtrude","SWEPT_FACE",FACE,{"disambiguationData":[OSD([sQuery(id+"F9.wireOp",EDGE,"E25")])]})]});
            var Q7;
            Q7=makeQuery(id+"F10.boolean.opBoolean","INTERSECT",EDGE,{"disambiguationData":[OD(1.0)],"derivedFrom":[makeQuery(id+"F1.opExtrude","SWEPT_FACE",FACE,{"disambiguationData":[OSD([sQuery(id+"F0.wireOp",EDGE,"E0")])]}),makeQuery(id+"F10.opExtrude","SWEPT_FACE",FACE,{"disambiguationData":[OSD([sQuery(id+"F9.wireOp",EDGE,"E24.3")])]})]});
            var Q8;
            Q8=makeQuery(id+"F10.boolean.opBoolean","INTERSECT",EDGE,{"disambiguationData":[OD(1.0)],"derivedFrom":[makeQuery(id+"F1.opExtrude","SWEPT_FACE",FACE,{"disambiguationData":[OSD([sQuery(id+"F0.wireOp",EDGE,"E0")])]}),makeQuery(id+"F10.opExtrude","SWEPT_FACE",FACE,{"disambiguationData":[OSD([sQuery(id+"F9.wireOp",EDGE,"YyubDx5s-D2ZM-0LxB-2Yu1-2PsOQiUhUxUO")])]})]});
            var Q9;
            Q9=makeQuery(id+"F10.boolean.opBoolean","INTERSECT",EDGE,{"disambiguationData":[OD(1.0)],"derivedFrom":[makeQuery(id+"F1.opExtrude","SWEPT_FACE",FACE,{"disambiguationData":[OSD([sQuery(id+"F0.wireOp",EDGE,"E0")])]}),makeQuery(id+"F10.opExtrude","SWEPT_FACE",FACE,{"disambiguationData":[OSD([sQuery(id+"F9.wireOp",EDGE,"FsT2MfZt-GKtl-NsVv-VaLI-5vvhgEFZWlKT"),sQuery(id+"F9.wireOp",EDGE,"dlvRKOJ7-262f-HahC-D8FB-32DCdauAgm7j")])]})]});
            var Q10;
            Q10=makeQuery(id+"F10.boolean.opBoolean","INTERSECT",EDGE,{"disambiguationData":[OD(1.0)],"derivedFrom":[makeQuery(id+"F1.opExtrude","SWEPT_FACE",FACE,{"disambiguationData":[OSD([sQuery(id+"F0.wireOp",EDGE,"E0")])]}),makeQuery(id+"F10.opExtrude","SWEPT_FACE",FACE,{"disambiguationData":[OSD([sQuery(id+"F9.wireOp",EDGE,"SvTCUe0E-rdOP-nI53-K5Gz-17hXMqdQ46nj")])]})]});
            var Q11;
            Q11=makeQuery(id+"F10.boolean.opBoolean","INTERSECT",EDGE,{"disambiguationData":[OD(1.0)],"derivedFrom":[makeQuery(id+"F1.opExtrude","SWEPT_FACE",FACE,{"disambiguationData":[OSD([sQuery(id+"F0.wireOp",EDGE,"E0")])]}),makeQuery(id+"F10.opExtrude","SWEPT_FACE",FACE,{"disambiguationData":[OSD([sQuery(id+"F9.wireOp",EDGE,"E14.3")])]})]});
            var Q12;
            Q12=makeQuery(id+"F10.boolean.opBoolean","INTERSECT",EDGE,{"disambiguationData":[OD(1.0)],"derivedFrom":[makeQuery(id+"F1.opExtrude","SWEPT_FACE",FACE,{"disambiguationData":[OSD([sQuery(id+"F0.wireOp",EDGE,"E0")])]}),makeQuery(id+"F10.opExtrude","SWEPT_FACE",FACE,{"disambiguationData":[OSD([sQuery(id+"F9.wireOp",EDGE,"E14.2")])]})]});
            var Q13;
            Q13=makeQuery(id+"F10.boolean.opBoolean","INTERSECT",EDGE,{"disambiguationData":[OD(1.0)],"derivedFrom":[makeQuery(id+"F1.opExtrude","SWEPT_FACE",FACE,{"disambiguationData":[OSD([sQuery(id+"F0.wireOp",EDGE,"E0")])]}),makeQuery(id+"F10.opExtrude","SWEPT_FACE",FACE,{"disambiguationData":[OSD([sQuery(id+"F9.wireOp",EDGE,"E14.1")])]})]});
            var Q14;
            Q14=makeQuery(id+"F10.boolean.opBoolean","INTERSECT",EDGE,{"disambiguationData":[OD(1.0)],"derivedFrom":[makeQuery(id+"F1.opExtrude","SWEPT_FACE",FACE,{"disambiguationData":[OSD([sQuery(id+"F0.wireOp",EDGE,"E0")])]}),makeQuery(id+"F10.opExtrude","SWEPT_FACE",FACE,{"disambiguationData":[OSD([sQuery(id+"F9.wireOp",EDGE,"E14.0")])]})]});
            var Q15;
            Q15=makeQuery(id+"F10.boolean.opBoolean","INTERSECT",EDGE,{"disambiguationData":[OD(1.0)],"derivedFrom":[makeQuery(id+"F1.opExtrude","SWEPT_FACE",FACE,{"disambiguationData":[OSD([sQuery(id+"F0.wireOp",EDGE,"E0")])]}),makeQuery(id+"F10.opExtrude","SWEPT_FACE",FACE,{"disambiguationData":[OSD([sQuery(id+"F9.wireOp",EDGE,"E14.5")])]})]});
            var Q16;
            Q16=makeQuery(id+"F10.boolean.opBoolean","INTERSECT",EDGE,{"disambiguationData":[OD(1.0)],"derivedFrom":[makeQuery(id+"F1.opExtrude","SWEPT_FACE",FACE,{"disambiguationData":[OSD([sQuery(id+"F0.wireOp",EDGE,"E0")])]}),makeQuery(id+"F10.opExtrude","SWEPT_FACE",FACE,{"disambiguationData":[OSD([sQuery(id+"F9.wireOp",EDGE,"E14.4")])]})]});
            var Q17;
            Q17=makeQuery(id+"F10.boolean.opBoolean","INTERSECT",EDGE,{"disambiguationData":[OD(1.0)],"derivedFrom":[makeQuery(id+"F1.opExtrude","SWEPT_FACE",FACE,{"disambiguationData":[OSD([sQuery(id+"F0.wireOp",EDGE,"E0")])]}),makeQuery(id+"F10.opExtrude","SWEPT_FACE",FACE,{"disambiguationData":[OSD([sQuery(id+"F9.wireOp",EDGE,"E15.0.1.6")])]})]});
            var Q18;
            Q18=makeQuery(id+"F10.boolean.opBoolean","INTERSECT",EDGE,{"disambiguationData":[OD(1.0)],"derivedFrom":[makeQuery(id+"F1.opExtrude","SWEPT_FACE",FACE,{"disambiguationData":[OSD([sQuery(id+"F0.wireOp",EDGE,"E0")])]}),makeQuery(id+"F10.opExtrude","SWEPT_FACE",FACE,{"disambiguationData":[OSD([sQuery(id+"F9.wireOp",EDGE,"E15.0.1.2")])]})]});
            var Q19;
            Q19=makeQuery(id+"F10.boolean.opBoolean","INTERSECT",EDGE,{"disambiguationData":[OD(1.0)],"derivedFrom":[makeQuery(id+"F1.opExtrude","SWEPT_FACE",FACE,{"disambiguationData":[OSD([sQuery(id+"F0.wireOp",EDGE,"E0")])]}),makeQuery(id+"F10.opExtrude","SWEPT_FACE",FACE,{"disambiguationData":[OSD([sQuery(id+"F9.wireOp",EDGE,"E15.0.1.3")])]})]});
            var Q20;
            Q20=makeQuery(id+"F10.boolean.opBoolean","INTERSECT",EDGE,{"disambiguationData":[OD(1.0)],"derivedFrom":[makeQuery(id+"F1.opExtrude","SWEPT_FACE",FACE,{"disambiguationData":[OSD([sQuery(id+"F0.wireOp",EDGE,"E0")])]}),makeQuery(id+"F10.opExtrude","SWEPT_FACE",FACE,{"disambiguationData":[OSD([sQuery(id+"F9.wireOp",EDGE,"E25")])]})]});
            var Q21;
            Q21=makeQuery(id+"F7.boolean.opBoolean","INTERSECT",EDGE,{"disambiguationData":[OD(1.0)],"derivedFrom":[makeQuery(id+"F1.opExtrude","SWEPT_FACE",FACE,{"disambiguationData":[OSD([sQuery(id+"F0.wireOp",EDGE,"E0")])]}),makeQuery(id+"F7.opExtrude","SWEPT_FACE",FACE,{"disambiguationData":[OSD([sQuery(id+"F6.wireOp",EDGE,"E11.0")])]})]});
            var Q22;
            Q22=makeQuery(id+"F7.boolean.opBoolean","INTERSECT",EDGE,{"disambiguationData":[OD(1.0)],"derivedFrom":[makeQuery(id+"F1.opExtrude","SWEPT_FACE",FACE,{"disambiguationData":[OSD([sQuery(id+"F0.wireOp",EDGE,"E0")])]}),makeQuery(id+"F7.opExtrude","SWEPT_FACE",FACE,{"disambiguationData":[OSD([sQuery(id+"F6.wireOp",EDGE,"E11.5")])]})]});
            var Q23;
            Q23=makeQuery(id+"F7.boolean.opBoolean","INTERSECT",EDGE,{"disambiguationData":[OD(1.0)],"derivedFrom":[makeQuery(id+"F1.opExtrude","SWEPT_FACE",FACE,{"disambiguationData":[OSD([sQuery(id+"F0.wireOp",EDGE,"E0")])]}),makeQuery(id+"F7.opExtrude","SWEPT_FACE",FACE,{"disambiguationData":[OSD([sQuery(id+"F6.wireOp",EDGE,"E11.4")])]})]});
            var Q24;
            Q24=makeQuery(id+"F7.boolean.opBoolean","INTERSECT",EDGE,{"disambiguationData":[OD(1.0)],"derivedFrom":[makeQuery(id+"F1.opExtrude","SWEPT_FACE",FACE,{"disambiguationData":[OSD([sQuery(id+"F0.wireOp",EDGE,"E0")])]}),makeQuery(id+"F7.opExtrude","SWEPT_FACE",FACE,{"disambiguationData":[OSD([sQuery(id+"F6.wireOp",EDGE,"E11.3")])]})]});
            var Q25;
            Q25=makeQuery(id+"F7.boolean.opBoolean","INTERSECT",EDGE,{"disambiguationData":[OD(1.0)],"derivedFrom":[makeQuery(id+"F1.opExtrude","SWEPT_FACE",FACE,{"disambiguationData":[OSD([sQuery(id+"F0.wireOp",EDGE,"E0")])]}),makeQuery(id+"F7.opExtrude","SWEPT_FACE",FACE,{"disambiguationData":[OSD([sQuery(id+"F6.wireOp",EDGE,"E11.2")])]})]});
            var Q26;
            Q26=makeQuery(id+"F7.boolean.opBoolean","INTERSECT",EDGE,{"disambiguationData":[OD(1.0)],"derivedFrom":[makeQuery(id+"F1.opExtrude","SWEPT_FACE",FACE,{"disambiguationData":[OSD([sQuery(id+"F0.wireOp",EDGE,"E0")])]}),makeQuery(id+"F7.opExtrude","SWEPT_FACE",FACE,{"disambiguationData":[OSD([sQuery(id+"F6.wireOp",EDGE,"E11.1")])]})]});
            var Q27;
            Q27=makeQuery(id+"F7.boolean.opBoolean","INTERSECT",EDGE,{"disambiguationData":[OD(1.0)],"derivedFrom":[makeQuery(id+"F1.opExtrude","SWEPT_FACE",FACE,{"disambiguationData":[OSD([sQuery(id+"F0.wireOp",EDGE,"E0")])]}),makeQuery(id+"F7.opExtrude","SWEPT_FACE",FACE,{"disambiguationData":[OSD([sQuery(id+"F6.wireOp",EDGE,"E8.1")])]})]});
            var Q28;
            Q28=makeQuery(id+"F7.boolean.opBoolean","INTERSECT",EDGE,{"disambiguationData":[OD(1.0)],"derivedFrom":[makeQuery(id+"F1.opExtrude","SWEPT_FACE",FACE,{"disambiguationData":[OSD([sQuery(id+"F0.wireOp",EDGE,"E0")])]}),makeQuery(id+"F7.opExtrude","SWEPT_FACE",FACE,{"disambiguationData":[OSD([sQuery(id+"F6.wireOp",EDGE,"E8.2")])]})]});
            var Q29;
            Q29=makeQuery(id+"F7.boolean.opBoolean","INTERSECT",EDGE,{"disambiguationData":[OD(1.0)],"derivedFrom":[makeQuery(id+"F1.opExtrude","SWEPT_FACE",FACE,{"disambiguationData":[OSD([sQuery(id+"F0.wireOp",EDGE,"E0")])]}),makeQuery(id+"F7.opExtrude","SWEPT_FACE",FACE,{"disambiguationData":[OSD([sQuery(id+"F6.wireOp",EDGE,"E8.3")])]})]});
            var Q30;
            Q30=makeQuery(id+"F7.boolean.opBoolean","INTERSECT",EDGE,{"disambiguationData":[OD(1.0)],"derivedFrom":[makeQuery(id+"F1.opExtrude","SWEPT_FACE",FACE,{"disambiguationData":[OSD([sQuery(id+"F0.wireOp",EDGE,"E0")])]}),makeQuery(id+"F7.opExtrude","SWEPT_FACE",FACE,{"disambiguationData":[OSD([sQuery(id+"F6.wireOp",EDGE,"E8.4")])]})]});
            var Q31;
            Q31=makeQuery(id+"F7.boolean.opBoolean","INTERSECT",EDGE,{"disambiguationData":[OD(1.0)],"derivedFrom":[makeQuery(id+"F1.opExtrude","SWEPT_FACE",FACE,{"disambiguationData":[OSD([sQuery(id+"F0.wireOp",EDGE,"E0")])]}),makeQuery(id+"F7.opExtrude","SWEPT_FACE",FACE,{"disambiguationData":[OSD([sQuery(id+"F6.wireOp",EDGE,"E8.5")])]})]});
            var Q32;
            Q32=makeQuery(id+"F7.boolean.opBoolean","INTERSECT",EDGE,{"disambiguationData":[OD(1.0)],"derivedFrom":[makeQuery(id+"F1.opExtrude","SWEPT_FACE",FACE,{"disambiguationData":[OSD([sQuery(id+"F0.wireOp",EDGE,"E0")])]}),makeQuery(id+"F7.opExtrude","SWEPT_FACE",FACE,{"disambiguationData":[OSD([sQuery(id+"F6.wireOp",EDGE,"E8.0")])]})]});
            var Q33;
            Q33=makeQuery(id+"F7.boolean.opBoolean","INTERSECT",EDGE,{"disambiguationData":[OD(0.0)],"derivedFrom":[makeQuery(id+"F1.opExtrude","SWEPT_FACE",FACE,{"disambiguationData":[OSD([sQuery(id+"F0.wireOp",EDGE,"E0")])]}),makeQuery(id+"F7.opExtrude","SWEPT_FACE",FACE,{"disambiguationData":[OSD([sQuery(id+"F6.wireOp",EDGE,"E8.1")])]})]});
            var Q34;
            Q34=makeQuery(id+"F7.boolean.opBoolean","INTERSECT",EDGE,{"disambiguationData":[OD(0.0)],"derivedFrom":[makeQuery(id+"F1.opExtrude","SWEPT_FACE",FACE,{"disambiguationData":[OSD([sQuery(id+"F0.wireOp",EDGE,"E0")])]}),makeQuery(id+"F7.opExtrude","SWEPT_FACE",FACE,{"disambiguationData":[OSD([sQuery(id+"F6.wireOp",EDGE,"E11.5")])]})]});
            var Q35;
            Q35=makeQuery(id+"F7.boolean.opBoolean","INTERSECT",EDGE,{"disambiguationData":[OD(0.0)],"derivedFrom":[makeQuery(id+"F1.opExtrude","SWEPT_FACE",FACE,{"disambiguationData":[OSD([sQuery(id+"F0.wireOp",EDGE,"E0")])]}),makeQuery(id+"F7.opExtrude","SWEPT_FACE",FACE,{"disambiguationData":[OSD([sQuery(id+"F6.wireOp",EDGE,"E11.4")])]})]});
            var Q36;
            Q36=makeQuery(id+"F7.boolean.opBoolean","INTERSECT",EDGE,{"disambiguationData":[OD(0.0)],"derivedFrom":[makeQuery(id+"F1.opExtrude","SWEPT_FACE",FACE,{"disambiguationData":[OSD([sQuery(id+"F0.wireOp",EDGE,"E0")])]}),makeQuery(id+"F7.opExtrude","SWEPT_FACE",FACE,{"disambiguationData":[OSD([sQuery(id+"F6.wireOp",EDGE,"E11.3")])]})]});
            fillet(context, id + "F17", {"entities" : qUnion([Q0, Q1, Q2, Q3, Q4, Q5, Q6, Q7, Q8, Q9, Q10, Q11, Q12, Q13, Q14, Q15, Q16, Q17, Q18, Q19, Q20, Q21, Q22, Q23, Q24, Q25, Q26, Q27, Q28, Q29, Q30, Q31, Q32, Q33, Q34, Q35, Q36]), "tangentPropagation" : true, "radius" : 0.7 * mm, "defaultsChanged" : true, "vertexSettings" : [], "allowEdgeOverflow" : false});
        }
    });
